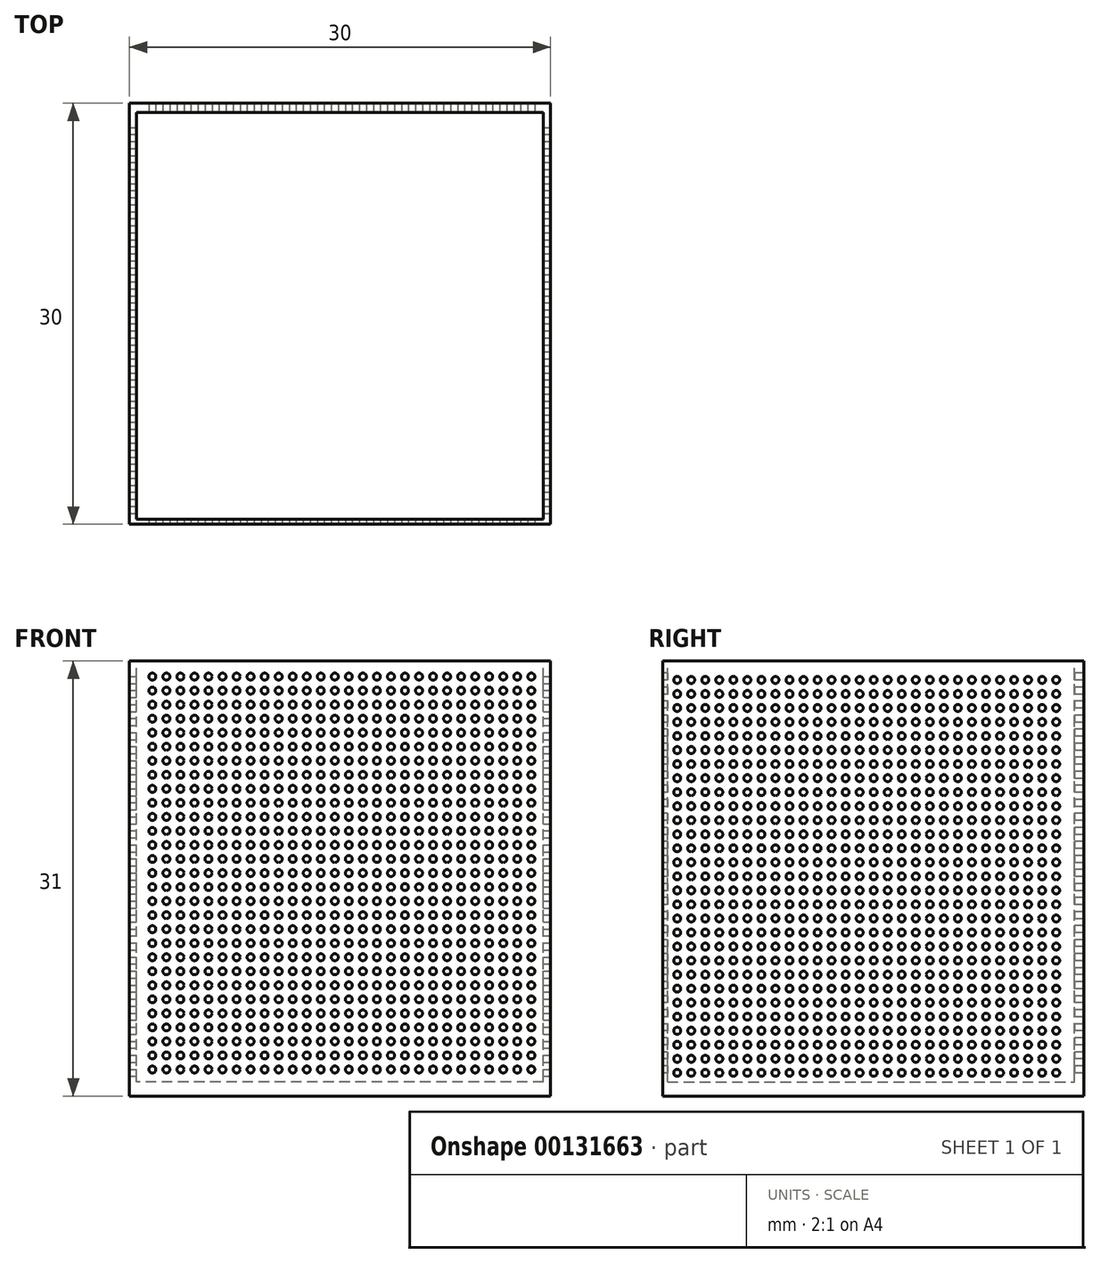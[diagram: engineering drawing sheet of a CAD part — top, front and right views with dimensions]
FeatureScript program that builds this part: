
annotation { "Feature Type Name" : "Feature", "Feature Type Description" : "" }
export const myFeature = defineFeature(function(context is Context, id is Id, definition is map)
    precondition{}
    {
        {
            var Q0;
            Q0=qCreatedBy(makeId("Top.planeOp"),FACE);
            var sketch = newSketch(context, id + "F0", { "sketchPlane" : qUnion([Q0])});
            skLineSegment(sketch, "E0.bottom", {"start": v(15, -14.84) * mm, "end": v(-15, -14.84) * mm});
            skLineSegment(sketch, "E0.top", {"start": v(15, 15.16) * mm, "end": v(-15, 15.16) * mm});
            skLineSegment(sketch, "E0.left", {"start": v(15, -14.84) * mm, "end": v(15, 15.16) * mm});
            skLineSegment(sketch, "E0.right", {"start": v(-15, -14.84) * mm, "end": v(-15, 15.16) * mm});
            skPoint(sketch, "E0.middle", {"position": v(0, 0.16) * mm});
            skSolve(sketch);
        }
        {
            var Q0;
            Q0 = qSketchRegion(id + "F0", true);
            extrude(context, id + "F1", {"entities" : qUnion([Q0]), "depth" : 31 * mm});
        }
        {
            var Q0;
            Q0=makeQuery(id+"F1.opExtrude","CAP_FACE",FACE,{"disambiguationData":[OSD([sQuery(id+"F0.wireOp",EDGE,"E0.bottom"),sQuery(id+"F0.wireOp",EDGE,"E0.top"),sQuery(id+"F0.wireOp",EDGE,"E0.left"),sQuery(id+"F0.wireOp",EDGE,"E0.right")])],"isStart":false});
            var sketch = newSketch(context, id + "F2", { "sketchPlane" : qUnion([Q0])});
            skLineSegment(sketch, "E1.bottom", {"start": v(14.5, -14.5) * mm, "end": v(-14.5, -14.5) * mm});
            skLineSegment(sketch, "E1.top", {"start": v(14.5, 14.5) * mm, "end": v(-14.5, 14.5) * mm});
            skLineSegment(sketch, "E1.left", {"start": v(14.5, -14.5) * mm, "end": v(14.5, 14.5) * mm});
            skLineSegment(sketch, "E1.right", {"start": v(-14.5, -14.5) * mm, "end": v(-14.5, 14.5) * mm});
            skPoint(sketch, "E1.middle", {"position": v(0, 0) * mm});
            skSolve(sketch);
        }
        {
            var Q0;
            Q0 = qSketchRegion(id + "F2", true);
            extrude(context, id + "F3", {"entities" : qUnion([Q0]), "operationType" : NewBodyOperationType.REMOVE, "oppositeDirection" : true, "depth" : 30 * mm});
        }
        {
            var Q0;
            Q0=makeQuery(id+"F1.opExtrude","SWEPT_FACE",FACE,{"disambiguationData":[OSD([sQuery(id+"F0.wireOp",EDGE,"E0.bottom")])]});
            var sketch = newSketch(context, id + "F4", { "sketchPlane" : qUnion([Q0])});
            skCircle(sketch, "E2", {"center": v(-13.37, 1.9) * mm, "radius": 0.25 * mm});
            skCircle(sketch, "E3.0.1.0", {"center": v(-13.37, 2.9) * mm, "radius": 0.25 * mm});
            skCircle(sketch, "E3.0.2.0", {"center": v(-13.37, 3.9) * mm, "radius": 0.25 * mm});
            skCircle(sketch, "E3.0.3.0", {"center": v(-13.37, 4.9) * mm, "radius": 0.25 * mm});
            skCircle(sketch, "E3.0.4.0", {"center": v(-13.37, 5.9) * mm, "radius": 0.25 * mm});
            skCircle(sketch, "E3.0.5.0", {"center": v(-13.37, 6.9) * mm, "radius": 0.25 * mm});
            skCircle(sketch, "E3.0.6.0", {"center": v(-13.37, 7.9) * mm, "radius": 0.25 * mm});
            skCircle(sketch, "E3.0.7.0", {"center": v(-13.37, 8.9) * mm, "radius": 0.25 * mm});
            skCircle(sketch, "E3.0.8.0", {"center": v(-13.37, 9.9) * mm, "radius": 0.25 * mm});
            skCircle(sketch, "E3.0.9.0", {"center": v(-13.37, 10.9) * mm, "radius": 0.25 * mm});
            skCircle(sketch, "E3.0.10.0", {"center": v(-13.37, 11.9) * mm, "radius": 0.25 * mm});
            skCircle(sketch, "E3.0.11.0", {"center": v(-13.37, 12.9) * mm, "radius": 0.25 * mm});
            skCircle(sketch, "E3.0.12.0", {"center": v(-13.37, 13.9) * mm, "radius": 0.25 * mm});
            skCircle(sketch, "E3.0.13.0", {"center": v(-13.37, 14.9) * mm, "radius": 0.25 * mm});
            skCircle(sketch, "E3.0.14.0", {"center": v(-13.37, 15.9) * mm, "radius": 0.25 * mm});
            skCircle(sketch, "E3.0.15.0", {"center": v(-13.37, 16.9) * mm, "radius": 0.25 * mm});
            skCircle(sketch, "E3.0.16.0", {"center": v(-13.37, 17.9) * mm, "radius": 0.25 * mm});
            skCircle(sketch, "E3.0.17.0", {"center": v(-13.37, 18.9) * mm, "radius": 0.25 * mm});
            skCircle(sketch, "E3.0.18.0", {"center": v(-13.37, 19.9) * mm, "radius": 0.25 * mm});
            skCircle(sketch, "E3.0.19.0", {"center": v(-13.37, 20.9) * mm, "radius": 0.25 * mm});
            skCircle(sketch, "E3.0.20.0", {"center": v(-13.37, 21.9) * mm, "radius": 0.25 * mm});
            skCircle(sketch, "E3.0.21.0", {"center": v(-13.37, 22.9) * mm, "radius": 0.25 * mm});
            skCircle(sketch, "E3.0.22.0", {"center": v(-13.37, 23.9) * mm, "radius": 0.25 * mm});
            skCircle(sketch, "E3.0.23.0", {"center": v(-13.37, 24.9) * mm, "radius": 0.25 * mm});
            skCircle(sketch, "E3.0.24.0", {"center": v(-13.37, 25.9) * mm, "radius": 0.25 * mm});
            skCircle(sketch, "E3.0.25.0", {"center": v(-13.37, 26.9) * mm, "radius": 0.25 * mm});
            skCircle(sketch, "E3.0.26.0", {"center": v(-13.37, 27.9) * mm, "radius": 0.25 * mm});
            skCircle(sketch, "E3.0.27.0", {"center": v(-13.37, 28.9) * mm, "radius": 0.25 * mm});
            skCircle(sketch, "E3.0.28.0", {"center": v(-13.37, 29.9) * mm, "radius": 0.25 * mm});
            skCircle(sketch, "E3.1.0.0", {"center": v(-12.37, 1.9) * mm, "radius": 0.25 * mm});
            skCircle(sketch, "E3.1.1.0", {"center": v(-12.37, 2.9) * mm, "radius": 0.25 * mm});
            skCircle(sketch, "E3.1.2.0", {"center": v(-12.37, 3.9) * mm, "radius": 0.25 * mm});
            skCircle(sketch, "E3.1.3.0", {"center": v(-12.37, 4.9) * mm, "radius": 0.25 * mm});
            skCircle(sketch, "E3.1.4.0", {"center": v(-12.37, 5.9) * mm, "radius": 0.25 * mm});
            skCircle(sketch, "E3.1.5.0", {"center": v(-12.37, 6.9) * mm, "radius": 0.25 * mm});
            skCircle(sketch, "E3.1.6.0", {"center": v(-12.37, 7.9) * mm, "radius": 0.25 * mm});
            skCircle(sketch, "E3.1.7.0", {"center": v(-12.37, 8.9) * mm, "radius": 0.25 * mm});
            skCircle(sketch, "E3.1.8.0", {"center": v(-12.37, 9.9) * mm, "radius": 0.25 * mm});
            skCircle(sketch, "E3.1.9.0", {"center": v(-12.37, 10.9) * mm, "radius": 0.25 * mm});
            skCircle(sketch, "E3.1.10.0", {"center": v(-12.37, 11.9) * mm, "radius": 0.25 * mm});
            skCircle(sketch, "E3.1.11.0", {"center": v(-12.37, 12.9) * mm, "radius": 0.25 * mm});
            skCircle(sketch, "E3.1.12.0", {"center": v(-12.37, 13.9) * mm, "radius": 0.25 * mm});
            skCircle(sketch, "E3.1.13.0", {"center": v(-12.37, 14.9) * mm, "radius": 0.25 * mm});
            skCircle(sketch, "E3.1.14.0", {"center": v(-12.37, 15.9) * mm, "radius": 0.25 * mm});
            skCircle(sketch, "E3.1.15.0", {"center": v(-12.37, 16.9) * mm, "radius": 0.25 * mm});
            skCircle(sketch, "E3.1.16.0", {"center": v(-12.37, 17.9) * mm, "radius": 0.25 * mm});
            skCircle(sketch, "E3.1.17.0", {"center": v(-12.37, 18.9) * mm, "radius": 0.25 * mm});
            skCircle(sketch, "E3.1.18.0", {"center": v(-12.37, 19.9) * mm, "radius": 0.25 * mm});
            skCircle(sketch, "E3.1.19.0", {"center": v(-12.37, 20.9) * mm, "radius": 0.25 * mm});
            skCircle(sketch, "E3.1.20.0", {"center": v(-12.37, 21.9) * mm, "radius": 0.25 * mm});
            skCircle(sketch, "E3.1.21.0", {"center": v(-12.37, 22.9) * mm, "radius": 0.25 * mm});
            skCircle(sketch, "E3.1.22.0", {"center": v(-12.37, 23.9) * mm, "radius": 0.25 * mm});
            skCircle(sketch, "E3.1.23.0", {"center": v(-12.37, 24.9) * mm, "radius": 0.25 * mm});
            skCircle(sketch, "E3.1.24.0", {"center": v(-12.37, 25.9) * mm, "radius": 0.25 * mm});
            skCircle(sketch, "E3.1.25.0", {"center": v(-12.37, 26.9) * mm, "radius": 0.25 * mm});
            skCircle(sketch, "E3.1.26.0", {"center": v(-12.37, 27.9) * mm, "radius": 0.25 * mm});
            skCircle(sketch, "E3.1.27.0", {"center": v(-12.37, 28.9) * mm, "radius": 0.25 * mm});
            skCircle(sketch, "E3.1.28.0", {"center": v(-12.37, 29.9) * mm, "radius": 0.25 * mm});
            skCircle(sketch, "E3.2.0.0", {"center": v(-11.37, 1.9) * mm, "radius": 0.25 * mm});
            skCircle(sketch, "E3.2.1.0", {"center": v(-11.37, 2.9) * mm, "radius": 0.25 * mm});
            skCircle(sketch, "E3.2.2.0", {"center": v(-11.37, 3.9) * mm, "radius": 0.25 * mm});
            skCircle(sketch, "E3.2.3.0", {"center": v(-11.37, 4.9) * mm, "radius": 0.25 * mm});
            skCircle(sketch, "E3.2.4.0", {"center": v(-11.37, 5.9) * mm, "radius": 0.25 * mm});
            skCircle(sketch, "E3.2.5.0", {"center": v(-11.37, 6.9) * mm, "radius": 0.25 * mm});
            skCircle(sketch, "E3.2.6.0", {"center": v(-11.37, 7.9) * mm, "radius": 0.25 * mm});
            skCircle(sketch, "E3.2.7.0", {"center": v(-11.37, 8.9) * mm, "radius": 0.25 * mm});
            skCircle(sketch, "E3.2.8.0", {"center": v(-11.37, 9.9) * mm, "radius": 0.25 * mm});
            skCircle(sketch, "E3.2.9.0", {"center": v(-11.37, 10.9) * mm, "radius": 0.25 * mm});
            skCircle(sketch, "E3.2.10.0", {"center": v(-11.37, 11.9) * mm, "radius": 0.25 * mm});
            skCircle(sketch, "E3.2.11.0", {"center": v(-11.37, 12.9) * mm, "radius": 0.25 * mm});
            skCircle(sketch, "E3.2.12.0", {"center": v(-11.37, 13.9) * mm, "radius": 0.25 * mm});
            skCircle(sketch, "E3.2.13.0", {"center": v(-11.37, 14.9) * mm, "radius": 0.25 * mm});
            skCircle(sketch, "E3.2.14.0", {"center": v(-11.37, 15.9) * mm, "radius": 0.25 * mm});
            skCircle(sketch, "E3.2.15.0", {"center": v(-11.37, 16.9) * mm, "radius": 0.25 * mm});
            skCircle(sketch, "E3.2.16.0", {"center": v(-11.37, 17.9) * mm, "radius": 0.25 * mm});
            skCircle(sketch, "E3.2.17.0", {"center": v(-11.37, 18.9) * mm, "radius": 0.25 * mm});
            skCircle(sketch, "E3.2.18.0", {"center": v(-11.37, 19.9) * mm, "radius": 0.25 * mm});
            skCircle(sketch, "E3.2.19.0", {"center": v(-11.37, 20.9) * mm, "radius": 0.25 * mm});
            skCircle(sketch, "E3.2.20.0", {"center": v(-11.37, 21.9) * mm, "radius": 0.25 * mm});
            skCircle(sketch, "E3.2.21.0", {"center": v(-11.37, 22.9) * mm, "radius": 0.25 * mm});
            skCircle(sketch, "E3.2.22.0", {"center": v(-11.37, 23.9) * mm, "radius": 0.25 * mm});
            skCircle(sketch, "E3.2.23.0", {"center": v(-11.37, 24.9) * mm, "radius": 0.25 * mm});
            skCircle(sketch, "E3.2.24.0", {"center": v(-11.37, 25.9) * mm, "radius": 0.25 * mm});
            skCircle(sketch, "E3.2.25.0", {"center": v(-11.37, 26.9) * mm, "radius": 0.25 * mm});
            skCircle(sketch, "E3.2.26.0", {"center": v(-11.37, 27.9) * mm, "radius": 0.25 * mm});
            skCircle(sketch, "E3.2.27.0", {"center": v(-11.37, 28.9) * mm, "radius": 0.25 * mm});
            skCircle(sketch, "E3.2.28.0", {"center": v(-11.37, 29.9) * mm, "radius": 0.25 * mm});
            skCircle(sketch, "E3.3.0.0", {"center": v(-10.37, 1.9) * mm, "radius": 0.25 * mm});
            skCircle(sketch, "E3.3.1.0", {"center": v(-10.37, 2.9) * mm, "radius": 0.25 * mm});
            skCircle(sketch, "E3.3.2.0", {"center": v(-10.37, 3.9) * mm, "radius": 0.25 * mm});
            skCircle(sketch, "E3.3.3.0", {"center": v(-10.37, 4.9) * mm, "radius": 0.25 * mm});
            skCircle(sketch, "E3.3.4.0", {"center": v(-10.37, 5.9) * mm, "radius": 0.25 * mm});
            skCircle(sketch, "E3.3.5.0", {"center": v(-10.37, 6.9) * mm, "radius": 0.25 * mm});
            skCircle(sketch, "E3.3.6.0", {"center": v(-10.37, 7.9) * mm, "radius": 0.25 * mm});
            skCircle(sketch, "E3.3.7.0", {"center": v(-10.37, 8.9) * mm, "radius": 0.25 * mm});
            skCircle(sketch, "E3.3.8.0", {"center": v(-10.37, 9.9) * mm, "radius": 0.25 * mm});
            skCircle(sketch, "E3.3.9.0", {"center": v(-10.37, 10.9) * mm, "radius": 0.25 * mm});
            skCircle(sketch, "E3.3.10.0", {"center": v(-10.37, 11.9) * mm, "radius": 0.25 * mm});
            skCircle(sketch, "E3.3.11.0", {"center": v(-10.37, 12.9) * mm, "radius": 0.25 * mm});
            skCircle(sketch, "E3.3.12.0", {"center": v(-10.37, 13.9) * mm, "radius": 0.25 * mm});
            skCircle(sketch, "E3.3.13.0", {"center": v(-10.37, 14.9) * mm, "radius": 0.25 * mm});
            skCircle(sketch, "E3.3.14.0", {"center": v(-10.37, 15.9) * mm, "radius": 0.25 * mm});
            skCircle(sketch, "E3.3.15.0", {"center": v(-10.37, 16.9) * mm, "radius": 0.25 * mm});
            skCircle(sketch, "E3.3.16.0", {"center": v(-10.37, 17.9) * mm, "radius": 0.25 * mm});
            skCircle(sketch, "E3.3.17.0", {"center": v(-10.37, 18.9) * mm, "radius": 0.25 * mm});
            skCircle(sketch, "E3.3.18.0", {"center": v(-10.37, 19.9) * mm, "radius": 0.25 * mm});
            skCircle(sketch, "E3.3.19.0", {"center": v(-10.37, 20.9) * mm, "radius": 0.25 * mm});
            skCircle(sketch, "E3.3.20.0", {"center": v(-10.37, 21.9) * mm, "radius": 0.25 * mm});
            skCircle(sketch, "E3.3.21.0", {"center": v(-10.37, 22.9) * mm, "radius": 0.25 * mm});
            skCircle(sketch, "E3.3.22.0", {"center": v(-10.37, 23.9) * mm, "radius": 0.25 * mm});
            skCircle(sketch, "E3.3.23.0", {"center": v(-10.37, 24.9) * mm, "radius": 0.25 * mm});
            skCircle(sketch, "E3.3.24.0", {"center": v(-10.37, 25.9) * mm, "radius": 0.25 * mm});
            skCircle(sketch, "E3.3.25.0", {"center": v(-10.37, 26.9) * mm, "radius": 0.25 * mm});
            skCircle(sketch, "E3.3.26.0", {"center": v(-10.37, 27.9) * mm, "radius": 0.25 * mm});
            skCircle(sketch, "E3.3.27.0", {"center": v(-10.37, 28.9) * mm, "radius": 0.25 * mm});
            skCircle(sketch, "E3.3.28.0", {"center": v(-10.37, 29.9) * mm, "radius": 0.25 * mm});
            skCircle(sketch, "E3.4.0.0", {"center": v(-9.37, 1.9) * mm, "radius": 0.25 * mm});
            skCircle(sketch, "E3.4.1.0", {"center": v(-9.37, 2.9) * mm, "radius": 0.25 * mm});
            skCircle(sketch, "E3.4.2.0", {"center": v(-9.37, 3.9) * mm, "radius": 0.25 * mm});
            skCircle(sketch, "E3.4.3.0", {"center": v(-9.37, 4.9) * mm, "radius": 0.25 * mm});
            skCircle(sketch, "E3.4.4.0", {"center": v(-9.37, 5.9) * mm, "radius": 0.25 * mm});
            skCircle(sketch, "E3.4.5.0", {"center": v(-9.37, 6.9) * mm, "radius": 0.25 * mm});
            skCircle(sketch, "E3.4.6.0", {"center": v(-9.37, 7.9) * mm, "radius": 0.25 * mm});
            skCircle(sketch, "E3.4.7.0", {"center": v(-9.37, 8.9) * mm, "radius": 0.25 * mm});
            skCircle(sketch, "E3.4.8.0", {"center": v(-9.37, 9.9) * mm, "radius": 0.25 * mm});
            skCircle(sketch, "E3.4.9.0", {"center": v(-9.37, 10.9) * mm, "radius": 0.25 * mm});
            skCircle(sketch, "E3.4.10.0", {"center": v(-9.37, 11.9) * mm, "radius": 0.25 * mm});
            skCircle(sketch, "E3.4.11.0", {"center": v(-9.37, 12.9) * mm, "radius": 0.25 * mm});
            skCircle(sketch, "E3.4.12.0", {"center": v(-9.37, 13.9) * mm, "radius": 0.25 * mm});
            skCircle(sketch, "E3.4.13.0", {"center": v(-9.37, 14.9) * mm, "radius": 0.25 * mm});
            skCircle(sketch, "E3.4.14.0", {"center": v(-9.37, 15.9) * mm, "radius": 0.25 * mm});
            skCircle(sketch, "E3.4.15.0", {"center": v(-9.37, 16.9) * mm, "radius": 0.25 * mm});
            skCircle(sketch, "E3.4.16.0", {"center": v(-9.37, 17.9) * mm, "radius": 0.25 * mm});
            skCircle(sketch, "E3.4.17.0", {"center": v(-9.37, 18.9) * mm, "radius": 0.25 * mm});
            skCircle(sketch, "E3.4.18.0", {"center": v(-9.37, 19.9) * mm, "radius": 0.25 * mm});
            skCircle(sketch, "E3.4.19.0", {"center": v(-9.37, 20.9) * mm, "radius": 0.25 * mm});
            skCircle(sketch, "E3.4.20.0", {"center": v(-9.37, 21.9) * mm, "radius": 0.25 * mm});
            skCircle(sketch, "E3.4.21.0", {"center": v(-9.37, 22.9) * mm, "radius": 0.25 * mm});
            skCircle(sketch, "E3.4.22.0", {"center": v(-9.37, 23.9) * mm, "radius": 0.25 * mm});
            skCircle(sketch, "E3.4.23.0", {"center": v(-9.37, 24.9) * mm, "radius": 0.25 * mm});
            skCircle(sketch, "E3.4.24.0", {"center": v(-9.37, 25.9) * mm, "radius": 0.25 * mm});
            skCircle(sketch, "E3.4.25.0", {"center": v(-9.37, 26.9) * mm, "radius": 0.25 * mm});
            skCircle(sketch, "E3.4.26.0", {"center": v(-9.37, 27.9) * mm, "radius": 0.25 * mm});
            skCircle(sketch, "E3.4.27.0", {"center": v(-9.37, 28.9) * mm, "radius": 0.25 * mm});
            skCircle(sketch, "E3.4.28.0", {"center": v(-9.37, 29.9) * mm, "radius": 0.25 * mm});
            skCircle(sketch, "E3.5.0.0", {"center": v(-8.37, 1.9) * mm, "radius": 0.25 * mm});
            skCircle(sketch, "E3.5.1.0", {"center": v(-8.37, 2.9) * mm, "radius": 0.25 * mm});
            skCircle(sketch, "E3.5.2.0", {"center": v(-8.37, 3.9) * mm, "radius": 0.25 * mm});
            skCircle(sketch, "E3.5.3.0", {"center": v(-8.37, 4.9) * mm, "radius": 0.25 * mm});
            skCircle(sketch, "E3.5.4.0", {"center": v(-8.37, 5.9) * mm, "radius": 0.25 * mm});
            skCircle(sketch, "E3.5.5.0", {"center": v(-8.37, 6.9) * mm, "radius": 0.25 * mm});
            skCircle(sketch, "E3.5.6.0", {"center": v(-8.37, 7.9) * mm, "radius": 0.25 * mm});
            skCircle(sketch, "E3.5.7.0", {"center": v(-8.37, 8.9) * mm, "radius": 0.25 * mm});
            skCircle(sketch, "E3.5.8.0", {"center": v(-8.37, 9.9) * mm, "radius": 0.25 * mm});
            skCircle(sketch, "E3.5.9.0", {"center": v(-8.37, 10.9) * mm, "radius": 0.25 * mm});
            skCircle(sketch, "E3.5.10.0", {"center": v(-8.37, 11.9) * mm, "radius": 0.25 * mm});
            skCircle(sketch, "E3.5.11.0", {"center": v(-8.37, 12.9) * mm, "radius": 0.25 * mm});
            skCircle(sketch, "E3.5.12.0", {"center": v(-8.37, 13.9) * mm, "radius": 0.25 * mm});
            skCircle(sketch, "E3.5.13.0", {"center": v(-8.37, 14.9) * mm, "radius": 0.25 * mm});
            skCircle(sketch, "E3.5.14.0", {"center": v(-8.37, 15.9) * mm, "radius": 0.25 * mm});
            skCircle(sketch, "E3.5.15.0", {"center": v(-8.37, 16.9) * mm, "radius": 0.25 * mm});
            skCircle(sketch, "E3.5.16.0", {"center": v(-8.37, 17.9) * mm, "radius": 0.25 * mm});
            skCircle(sketch, "E3.5.17.0", {"center": v(-8.37, 18.9) * mm, "radius": 0.25 * mm});
            skCircle(sketch, "E3.5.18.0", {"center": v(-8.37, 19.9) * mm, "radius": 0.25 * mm});
            skCircle(sketch, "E3.5.19.0", {"center": v(-8.37, 20.9) * mm, "radius": 0.25 * mm});
            skCircle(sketch, "E3.5.20.0", {"center": v(-8.37, 21.9) * mm, "radius": 0.25 * mm});
            skCircle(sketch, "E3.5.21.0", {"center": v(-8.37, 22.9) * mm, "radius": 0.25 * mm});
            skCircle(sketch, "E3.5.22.0", {"center": v(-8.37, 23.9) * mm, "radius": 0.25 * mm});
            skCircle(sketch, "E3.5.23.0", {"center": v(-8.37, 24.9) * mm, "radius": 0.25 * mm});
            skCircle(sketch, "E3.5.24.0", {"center": v(-8.37, 25.9) * mm, "radius": 0.25 * mm});
            skCircle(sketch, "E3.5.25.0", {"center": v(-8.37, 26.9) * mm, "radius": 0.25 * mm});
            skCircle(sketch, "E3.5.26.0", {"center": v(-8.37, 27.9) * mm, "radius": 0.25 * mm});
            skCircle(sketch, "E3.5.27.0", {"center": v(-8.37, 28.9) * mm, "radius": 0.25 * mm});
            skCircle(sketch, "E3.5.28.0", {"center": v(-8.37, 29.9) * mm, "radius": 0.25 * mm});
            skCircle(sketch, "E3.6.0.0", {"center": v(-7.37, 1.9) * mm, "radius": 0.25 * mm});
            skCircle(sketch, "E3.6.1.0", {"center": v(-7.37, 2.9) * mm, "radius": 0.25 * mm});
            skCircle(sketch, "E3.6.2.0", {"center": v(-7.37, 3.9) * mm, "radius": 0.25 * mm});
            skCircle(sketch, "E3.6.3.0", {"center": v(-7.37, 4.9) * mm, "radius": 0.25 * mm});
            skCircle(sketch, "E3.6.4.0", {"center": v(-7.37, 5.9) * mm, "radius": 0.25 * mm});
            skCircle(sketch, "E3.6.5.0", {"center": v(-7.37, 6.9) * mm, "radius": 0.25 * mm});
            skCircle(sketch, "E3.6.6.0", {"center": v(-7.37, 7.9) * mm, "radius": 0.25 * mm});
            skCircle(sketch, "E3.6.7.0", {"center": v(-7.37, 8.9) * mm, "radius": 0.25 * mm});
            skCircle(sketch, "E3.6.8.0", {"center": v(-7.37, 9.9) * mm, "radius": 0.25 * mm});
            skCircle(sketch, "E3.6.9.0", {"center": v(-7.37, 10.9) * mm, "radius": 0.25 * mm});
            skCircle(sketch, "E3.6.10.0", {"center": v(-7.37, 11.9) * mm, "radius": 0.25 * mm});
            skCircle(sketch, "E3.6.11.0", {"center": v(-7.37, 12.9) * mm, "radius": 0.25 * mm});
            skCircle(sketch, "E3.6.12.0", {"center": v(-7.37, 13.9) * mm, "radius": 0.25 * mm});
            skCircle(sketch, "E3.6.13.0", {"center": v(-7.37, 14.9) * mm, "radius": 0.25 * mm});
            skCircle(sketch, "E3.6.14.0", {"center": v(-7.37, 15.9) * mm, "radius": 0.25 * mm});
            skCircle(sketch, "E3.6.15.0", {"center": v(-7.37, 16.9) * mm, "radius": 0.25 * mm});
            skCircle(sketch, "E3.6.16.0", {"center": v(-7.37, 17.9) * mm, "radius": 0.25 * mm});
            skCircle(sketch, "E3.6.17.0", {"center": v(-7.37, 18.9) * mm, "radius": 0.25 * mm});
            skCircle(sketch, "E3.6.18.0", {"center": v(-7.37, 19.9) * mm, "radius": 0.25 * mm});
            skCircle(sketch, "E3.6.19.0", {"center": v(-7.37, 20.9) * mm, "radius": 0.25 * mm});
            skCircle(sketch, "E3.6.20.0", {"center": v(-7.37, 21.9) * mm, "radius": 0.25 * mm});
            skCircle(sketch, "E3.6.21.0", {"center": v(-7.37, 22.9) * mm, "radius": 0.25 * mm});
            skCircle(sketch, "E3.6.22.0", {"center": v(-7.37, 23.9) * mm, "radius": 0.25 * mm});
            skCircle(sketch, "E3.6.23.0", {"center": v(-7.37, 24.9) * mm, "radius": 0.25 * mm});
            skCircle(sketch, "E3.6.24.0", {"center": v(-7.37, 25.9) * mm, "radius": 0.25 * mm});
            skCircle(sketch, "E3.6.25.0", {"center": v(-7.37, 26.9) * mm, "radius": 0.25 * mm});
            skCircle(sketch, "E3.6.26.0", {"center": v(-7.37, 27.9) * mm, "radius": 0.25 * mm});
            skCircle(sketch, "E3.6.27.0", {"center": v(-7.37, 28.9) * mm, "radius": 0.25 * mm});
            skCircle(sketch, "E3.6.28.0", {"center": v(-7.37, 29.9) * mm, "radius": 0.25 * mm});
            skCircle(sketch, "E3.7.0.0", {"center": v(-6.37, 1.9) * mm, "radius": 0.25 * mm});
            skCircle(sketch, "E3.7.1.0", {"center": v(-6.37, 2.9) * mm, "radius": 0.25 * mm});
            skCircle(sketch, "E3.7.2.0", {"center": v(-6.37, 3.9) * mm, "radius": 0.25 * mm});
            skCircle(sketch, "E3.7.3.0", {"center": v(-6.37, 4.9) * mm, "radius": 0.25 * mm});
            skCircle(sketch, "E3.7.4.0", {"center": v(-6.37, 5.9) * mm, "radius": 0.25 * mm});
            skCircle(sketch, "E3.7.5.0", {"center": v(-6.37, 6.9) * mm, "radius": 0.25 * mm});
            skCircle(sketch, "E3.7.6.0", {"center": v(-6.37, 7.9) * mm, "radius": 0.25 * mm});
            skCircle(sketch, "E3.7.7.0", {"center": v(-6.37, 8.9) * mm, "radius": 0.25 * mm});
            skCircle(sketch, "E3.7.8.0", {"center": v(-6.37, 9.9) * mm, "radius": 0.25 * mm});
            skCircle(sketch, "E3.7.9.0", {"center": v(-6.37, 10.9) * mm, "radius": 0.25 * mm});
            skCircle(sketch, "E3.7.10.0", {"center": v(-6.37, 11.9) * mm, "radius": 0.25 * mm});
            skCircle(sketch, "E3.7.11.0", {"center": v(-6.37, 12.9) * mm, "radius": 0.25 * mm});
            skCircle(sketch, "E3.7.12.0", {"center": v(-6.37, 13.9) * mm, "radius": 0.25 * mm});
            skCircle(sketch, "E3.7.13.0", {"center": v(-6.37, 14.9) * mm, "radius": 0.25 * mm});
            skCircle(sketch, "E3.7.14.0", {"center": v(-6.37, 15.9) * mm, "radius": 0.25 * mm});
            skCircle(sketch, "E3.7.15.0", {"center": v(-6.37, 16.9) * mm, "radius": 0.25 * mm});
            skCircle(sketch, "E3.7.16.0", {"center": v(-6.37, 17.9) * mm, "radius": 0.25 * mm});
            skCircle(sketch, "E3.7.17.0", {"center": v(-6.37, 18.9) * mm, "radius": 0.25 * mm});
            skCircle(sketch, "E3.7.18.0", {"center": v(-6.37, 19.9) * mm, "radius": 0.25 * mm});
            skCircle(sketch, "E3.7.19.0", {"center": v(-6.37, 20.9) * mm, "radius": 0.25 * mm});
            skCircle(sketch, "E3.7.20.0", {"center": v(-6.37, 21.9) * mm, "radius": 0.25 * mm});
            skCircle(sketch, "E3.7.21.0", {"center": v(-6.37, 22.9) * mm, "radius": 0.25 * mm});
            skCircle(sketch, "E3.7.22.0", {"center": v(-6.37, 23.9) * mm, "radius": 0.25 * mm});
            skCircle(sketch, "E3.7.23.0", {"center": v(-6.37, 24.9) * mm, "radius": 0.25 * mm});
            skCircle(sketch, "E3.7.24.0", {"center": v(-6.37, 25.9) * mm, "radius": 0.25 * mm});
            skCircle(sketch, "E3.7.25.0", {"center": v(-6.37, 26.9) * mm, "radius": 0.25 * mm});
            skCircle(sketch, "E3.7.26.0", {"center": v(-6.37, 27.9) * mm, "radius": 0.25 * mm});
            skCircle(sketch, "E3.7.27.0", {"center": v(-6.37, 28.9) * mm, "radius": 0.25 * mm});
            skCircle(sketch, "E3.7.28.0", {"center": v(-6.37, 29.9) * mm, "radius": 0.25 * mm});
            skCircle(sketch, "E3.8.0.0", {"center": v(-5.37, 1.9) * mm, "radius": 0.25 * mm});
            skCircle(sketch, "E3.8.1.0", {"center": v(-5.37, 2.9) * mm, "radius": 0.25 * mm});
            skCircle(sketch, "E3.8.2.0", {"center": v(-5.37, 3.9) * mm, "radius": 0.25 * mm});
            skCircle(sketch, "E3.8.3.0", {"center": v(-5.37, 4.9) * mm, "radius": 0.25 * mm});
            skCircle(sketch, "E3.8.4.0", {"center": v(-5.37, 5.9) * mm, "radius": 0.25 * mm});
            skCircle(sketch, "E3.8.5.0", {"center": v(-5.37, 6.9) * mm, "radius": 0.25 * mm});
            skCircle(sketch, "E3.8.6.0", {"center": v(-5.37, 7.9) * mm, "radius": 0.25 * mm});
            skCircle(sketch, "E3.8.7.0", {"center": v(-5.37, 8.9) * mm, "radius": 0.25 * mm});
            skCircle(sketch, "E3.8.8.0", {"center": v(-5.37, 9.9) * mm, "radius": 0.25 * mm});
            skCircle(sketch, "E3.8.9.0", {"center": v(-5.37, 10.9) * mm, "radius": 0.25 * mm});
            skCircle(sketch, "E3.8.10.0", {"center": v(-5.37, 11.9) * mm, "radius": 0.25 * mm});
            skCircle(sketch, "E3.8.11.0", {"center": v(-5.37, 12.9) * mm, "radius": 0.25 * mm});
            skCircle(sketch, "E3.8.12.0", {"center": v(-5.37, 13.9) * mm, "radius": 0.25 * mm});
            skCircle(sketch, "E3.8.13.0", {"center": v(-5.37, 14.9) * mm, "radius": 0.25 * mm});
            skCircle(sketch, "E3.8.14.0", {"center": v(-5.37, 15.9) * mm, "radius": 0.25 * mm});
            skCircle(sketch, "E3.8.15.0", {"center": v(-5.37, 16.9) * mm, "radius": 0.25 * mm});
            skCircle(sketch, "E3.8.16.0", {"center": v(-5.37, 17.9) * mm, "radius": 0.25 * mm});
            skCircle(sketch, "E3.8.17.0", {"center": v(-5.37, 18.9) * mm, "radius": 0.25 * mm});
            skCircle(sketch, "E3.8.18.0", {"center": v(-5.37, 19.9) * mm, "radius": 0.25 * mm});
            skCircle(sketch, "E3.8.19.0", {"center": v(-5.37, 20.9) * mm, "radius": 0.25 * mm});
            skCircle(sketch, "E3.8.20.0", {"center": v(-5.37, 21.9) * mm, "radius": 0.25 * mm});
            skCircle(sketch, "E3.8.21.0", {"center": v(-5.37, 22.9) * mm, "radius": 0.25 * mm});
            skCircle(sketch, "E3.8.22.0", {"center": v(-5.37, 23.9) * mm, "radius": 0.25 * mm});
            skCircle(sketch, "E3.8.23.0", {"center": v(-5.37, 24.9) * mm, "radius": 0.25 * mm});
            skCircle(sketch, "E3.8.24.0", {"center": v(-5.37, 25.9) * mm, "radius": 0.25 * mm});
            skCircle(sketch, "E3.8.25.0", {"center": v(-5.37, 26.9) * mm, "radius": 0.25 * mm});
            skCircle(sketch, "E3.8.26.0", {"center": v(-5.37, 27.9) * mm, "radius": 0.25 * mm});
            skCircle(sketch, "E3.8.27.0", {"center": v(-5.37, 28.9) * mm, "radius": 0.25 * mm});
            skCircle(sketch, "E3.8.28.0", {"center": v(-5.37, 29.9) * mm, "radius": 0.25 * mm});
            skCircle(sketch, "E3.9.0.0", {"center": v(-4.37, 1.9) * mm, "radius": 0.25 * mm});
            skCircle(sketch, "E3.9.1.0", {"center": v(-4.37, 2.9) * mm, "radius": 0.25 * mm});
            skCircle(sketch, "E3.9.2.0", {"center": v(-4.37, 3.9) * mm, "radius": 0.25 * mm});
            skCircle(sketch, "E3.9.3.0", {"center": v(-4.37, 4.9) * mm, "radius": 0.25 * mm});
            skCircle(sketch, "E3.9.4.0", {"center": v(-4.37, 5.9) * mm, "radius": 0.25 * mm});
            skCircle(sketch, "E3.9.5.0", {"center": v(-4.37, 6.9) * mm, "radius": 0.25 * mm});
            skCircle(sketch, "E3.9.6.0", {"center": v(-4.37, 7.9) * mm, "radius": 0.25 * mm});
            skCircle(sketch, "E3.9.7.0", {"center": v(-4.37, 8.9) * mm, "radius": 0.25 * mm});
            skCircle(sketch, "E3.9.8.0", {"center": v(-4.37, 9.9) * mm, "radius": 0.25 * mm});
            skCircle(sketch, "E3.9.9.0", {"center": v(-4.37, 10.9) * mm, "radius": 0.25 * mm});
            skCircle(sketch, "E3.9.10.0", {"center": v(-4.37, 11.9) * mm, "radius": 0.25 * mm});
            skCircle(sketch, "E3.9.11.0", {"center": v(-4.37, 12.9) * mm, "radius": 0.25 * mm});
            skCircle(sketch, "E3.9.12.0", {"center": v(-4.37, 13.9) * mm, "radius": 0.25 * mm});
            skCircle(sketch, "E3.9.13.0", {"center": v(-4.37, 14.9) * mm, "radius": 0.25 * mm});
            skCircle(sketch, "E3.9.14.0", {"center": v(-4.37, 15.9) * mm, "radius": 0.25 * mm});
            skCircle(sketch, "E3.9.15.0", {"center": v(-4.37, 16.9) * mm, "radius": 0.25 * mm});
            skCircle(sketch, "E3.9.16.0", {"center": v(-4.37, 17.9) * mm, "radius": 0.25 * mm});
            skCircle(sketch, "E3.9.17.0", {"center": v(-4.37, 18.9) * mm, "radius": 0.25 * mm});
            skCircle(sketch, "E3.9.18.0", {"center": v(-4.37, 19.9) * mm, "radius": 0.25 * mm});
            skCircle(sketch, "E3.9.19.0", {"center": v(-4.37, 20.9) * mm, "radius": 0.25 * mm});
            skCircle(sketch, "E3.9.20.0", {"center": v(-4.37, 21.9) * mm, "radius": 0.25 * mm});
            skCircle(sketch, "E3.9.21.0", {"center": v(-4.37, 22.9) * mm, "radius": 0.25 * mm});
            skCircle(sketch, "E3.9.22.0", {"center": v(-4.37, 23.9) * mm, "radius": 0.25 * mm});
            skCircle(sketch, "E3.9.23.0", {"center": v(-4.37, 24.9) * mm, "radius": 0.25 * mm});
            skCircle(sketch, "E3.9.24.0", {"center": v(-4.37, 25.9) * mm, "radius": 0.25 * mm});
            skCircle(sketch, "E3.9.25.0", {"center": v(-4.37, 26.9) * mm, "radius": 0.25 * mm});
            skCircle(sketch, "E3.9.26.0", {"center": v(-4.37, 27.9) * mm, "radius": 0.25 * mm});
            skCircle(sketch, "E3.9.27.0", {"center": v(-4.37, 28.9) * mm, "radius": 0.25 * mm});
            skCircle(sketch, "E3.9.28.0", {"center": v(-4.37, 29.9) * mm, "radius": 0.25 * mm});
            skCircle(sketch, "E3.10.0.0", {"center": v(-3.37, 1.9) * mm, "radius": 0.25 * mm});
            skCircle(sketch, "E3.10.1.0", {"center": v(-3.37, 2.9) * mm, "radius": 0.25 * mm});
            skCircle(sketch, "E3.10.2.0", {"center": v(-3.37, 3.9) * mm, "radius": 0.25 * mm});
            skCircle(sketch, "E3.10.3.0", {"center": v(-3.37, 4.9) * mm, "radius": 0.25 * mm});
            skCircle(sketch, "E3.10.4.0", {"center": v(-3.37, 5.9) * mm, "radius": 0.25 * mm});
            skCircle(sketch, "E3.10.5.0", {"center": v(-3.37, 6.9) * mm, "radius": 0.25 * mm});
            skCircle(sketch, "E3.10.6.0", {"center": v(-3.37, 7.9) * mm, "radius": 0.25 * mm});
            skCircle(sketch, "E3.10.7.0", {"center": v(-3.37, 8.9) * mm, "radius": 0.25 * mm});
            skCircle(sketch, "E3.10.8.0", {"center": v(-3.37, 9.9) * mm, "radius": 0.25 * mm});
            skCircle(sketch, "E3.10.9.0", {"center": v(-3.37, 10.9) * mm, "radius": 0.25 * mm});
            skCircle(sketch, "E3.10.10.0", {"center": v(-3.37, 11.9) * mm, "radius": 0.25 * mm});
            skCircle(sketch, "E3.10.11.0", {"center": v(-3.37, 12.9) * mm, "radius": 0.25 * mm});
            skCircle(sketch, "E3.10.12.0", {"center": v(-3.37, 13.9) * mm, "radius": 0.25 * mm});
            skCircle(sketch, "E3.10.13.0", {"center": v(-3.37, 14.9) * mm, "radius": 0.25 * mm});
            skCircle(sketch, "E3.10.14.0", {"center": v(-3.37, 15.9) * mm, "radius": 0.25 * mm});
            skCircle(sketch, "E3.10.15.0", {"center": v(-3.37, 16.9) * mm, "radius": 0.25 * mm});
            skCircle(sketch, "E3.10.16.0", {"center": v(-3.37, 17.9) * mm, "radius": 0.25 * mm});
            skCircle(sketch, "E3.10.17.0", {"center": v(-3.37, 18.9) * mm, "radius": 0.25 * mm});
            skCircle(sketch, "E3.10.18.0", {"center": v(-3.37, 19.9) * mm, "radius": 0.25 * mm});
            skCircle(sketch, "E3.10.19.0", {"center": v(-3.37, 20.9) * mm, "radius": 0.25 * mm});
            skCircle(sketch, "E3.10.20.0", {"center": v(-3.37, 21.9) * mm, "radius": 0.25 * mm});
            skCircle(sketch, "E3.10.21.0", {"center": v(-3.37, 22.9) * mm, "radius": 0.25 * mm});
            skCircle(sketch, "E3.10.22.0", {"center": v(-3.37, 23.9) * mm, "radius": 0.25 * mm});
            skCircle(sketch, "E3.10.23.0", {"center": v(-3.37, 24.9) * mm, "radius": 0.25 * mm});
            skCircle(sketch, "E3.10.24.0", {"center": v(-3.37, 25.9) * mm, "radius": 0.25 * mm});
            skCircle(sketch, "E3.10.25.0", {"center": v(-3.37, 26.9) * mm, "radius": 0.25 * mm});
            skCircle(sketch, "E3.10.26.0", {"center": v(-3.37, 27.9) * mm, "radius": 0.25 * mm});
            skCircle(sketch, "E3.10.27.0", {"center": v(-3.37, 28.9) * mm, "radius": 0.25 * mm});
            skCircle(sketch, "E3.10.28.0", {"center": v(-3.37, 29.9) * mm, "radius": 0.25 * mm});
            skCircle(sketch, "E3.11.0.0", {"center": v(-2.37, 1.9) * mm, "radius": 0.25 * mm});
            skCircle(sketch, "E3.11.1.0", {"center": v(-2.37, 2.9) * mm, "radius": 0.25 * mm});
            skCircle(sketch, "E3.11.2.0", {"center": v(-2.37, 3.9) * mm, "radius": 0.25 * mm});
            skCircle(sketch, "E3.11.3.0", {"center": v(-2.37, 4.9) * mm, "radius": 0.25 * mm});
            skCircle(sketch, "E3.11.4.0", {"center": v(-2.37, 5.9) * mm, "radius": 0.25 * mm});
            skCircle(sketch, "E3.11.5.0", {"center": v(-2.37, 6.9) * mm, "radius": 0.25 * mm});
            skCircle(sketch, "E3.11.6.0", {"center": v(-2.37, 7.9) * mm, "radius": 0.25 * mm});
            skCircle(sketch, "E3.11.7.0", {"center": v(-2.37, 8.9) * mm, "radius": 0.25 * mm});
            skCircle(sketch, "E3.11.8.0", {"center": v(-2.37, 9.9) * mm, "radius": 0.25 * mm});
            skCircle(sketch, "E3.11.9.0", {"center": v(-2.37, 10.9) * mm, "radius": 0.25 * mm});
            skCircle(sketch, "E3.11.10.0", {"center": v(-2.37, 11.9) * mm, "radius": 0.25 * mm});
            skCircle(sketch, "E3.11.11.0", {"center": v(-2.37, 12.9) * mm, "radius": 0.25 * mm});
            skCircle(sketch, "E3.11.12.0", {"center": v(-2.37, 13.9) * mm, "radius": 0.25 * mm});
            skCircle(sketch, "E3.11.13.0", {"center": v(-2.37, 14.9) * mm, "radius": 0.25 * mm});
            skCircle(sketch, "E3.11.14.0", {"center": v(-2.37, 15.9) * mm, "radius": 0.25 * mm});
            skCircle(sketch, "E3.11.15.0", {"center": v(-2.37, 16.9) * mm, "radius": 0.25 * mm});
            skCircle(sketch, "E3.11.16.0", {"center": v(-2.37, 17.9) * mm, "radius": 0.25 * mm});
            skCircle(sketch, "E3.11.17.0", {"center": v(-2.37, 18.9) * mm, "radius": 0.25 * mm});
            skCircle(sketch, "E3.11.18.0", {"center": v(-2.37, 19.9) * mm, "radius": 0.25 * mm});
            skCircle(sketch, "E3.11.19.0", {"center": v(-2.37, 20.9) * mm, "radius": 0.25 * mm});
            skCircle(sketch, "E3.11.20.0", {"center": v(-2.37, 21.9) * mm, "radius": 0.25 * mm});
            skCircle(sketch, "E3.11.21.0", {"center": v(-2.37, 22.9) * mm, "radius": 0.25 * mm});
            skCircle(sketch, "E3.11.22.0", {"center": v(-2.37, 23.9) * mm, "radius": 0.25 * mm});
            skCircle(sketch, "E3.11.23.0", {"center": v(-2.37, 24.9) * mm, "radius": 0.25 * mm});
            skCircle(sketch, "E3.11.24.0", {"center": v(-2.37, 25.9) * mm, "radius": 0.25 * mm});
            skCircle(sketch, "E3.11.25.0", {"center": v(-2.37, 26.9) * mm, "radius": 0.25 * mm});
            skCircle(sketch, "E3.11.26.0", {"center": v(-2.37, 27.9) * mm, "radius": 0.25 * mm});
            skCircle(sketch, "E3.11.27.0", {"center": v(-2.37, 28.9) * mm, "radius": 0.25 * mm});
            skCircle(sketch, "E3.11.28.0", {"center": v(-2.37, 29.9) * mm, "radius": 0.25 * mm});
            skCircle(sketch, "E3.12.0.0", {"center": v(-1.37, 1.9) * mm, "radius": 0.25 * mm});
            skCircle(sketch, "E3.12.1.0", {"center": v(-1.37, 2.9) * mm, "radius": 0.25 * mm});
            skCircle(sketch, "E3.12.2.0", {"center": v(-1.37, 3.9) * mm, "radius": 0.25 * mm});
            skCircle(sketch, "E3.12.3.0", {"center": v(-1.37, 4.9) * mm, "radius": 0.25 * mm});
            skCircle(sketch, "E3.12.4.0", {"center": v(-1.37, 5.9) * mm, "radius": 0.25 * mm});
            skCircle(sketch, "E3.12.5.0", {"center": v(-1.37, 6.9) * mm, "radius": 0.25 * mm});
            skCircle(sketch, "E3.12.6.0", {"center": v(-1.37, 7.9) * mm, "radius": 0.25 * mm});
            skCircle(sketch, "E3.12.7.0", {"center": v(-1.37, 8.9) * mm, "radius": 0.25 * mm});
            skCircle(sketch, "E3.12.8.0", {"center": v(-1.37, 9.9) * mm, "radius": 0.25 * mm});
            skCircle(sketch, "E3.12.9.0", {"center": v(-1.37, 10.9) * mm, "radius": 0.25 * mm});
            skCircle(sketch, "E3.12.10.0", {"center": v(-1.37, 11.9) * mm, "radius": 0.25 * mm});
            skCircle(sketch, "E3.12.11.0", {"center": v(-1.37, 12.9) * mm, "radius": 0.25 * mm});
            skCircle(sketch, "E3.12.12.0", {"center": v(-1.37, 13.9) * mm, "radius": 0.25 * mm});
            skCircle(sketch, "E3.12.13.0", {"center": v(-1.37, 14.9) * mm, "radius": 0.25 * mm});
            skCircle(sketch, "E3.12.14.0", {"center": v(-1.37, 15.9) * mm, "radius": 0.25 * mm});
            skCircle(sketch, "E3.12.15.0", {"center": v(-1.37, 16.9) * mm, "radius": 0.25 * mm});
            skCircle(sketch, "E3.12.16.0", {"center": v(-1.37, 17.9) * mm, "radius": 0.25 * mm});
            skCircle(sketch, "E3.12.17.0", {"center": v(-1.37, 18.9) * mm, "radius": 0.25 * mm});
            skCircle(sketch, "E3.12.18.0", {"center": v(-1.37, 19.9) * mm, "radius": 0.25 * mm});
            skCircle(sketch, "E3.12.19.0", {"center": v(-1.37, 20.9) * mm, "radius": 0.25 * mm});
            skCircle(sketch, "E3.12.20.0", {"center": v(-1.37, 21.9) * mm, "radius": 0.25 * mm});
            skCircle(sketch, "E3.12.21.0", {"center": v(-1.37, 22.9) * mm, "radius": 0.25 * mm});
            skCircle(sketch, "E3.12.22.0", {"center": v(-1.37, 23.9) * mm, "radius": 0.25 * mm});
            skCircle(sketch, "E3.12.23.0", {"center": v(-1.37, 24.9) * mm, "radius": 0.25 * mm});
            skCircle(sketch, "E3.12.24.0", {"center": v(-1.37, 25.9) * mm, "radius": 0.25 * mm});
            skCircle(sketch, "E3.12.25.0", {"center": v(-1.37, 26.9) * mm, "radius": 0.25 * mm});
            skCircle(sketch, "E3.12.26.0", {"center": v(-1.37, 27.9) * mm, "radius": 0.25 * mm});
            skCircle(sketch, "E3.12.27.0", {"center": v(-1.37, 28.9) * mm, "radius": 0.25 * mm});
            skCircle(sketch, "E3.12.28.0", {"center": v(-1.37, 29.9) * mm, "radius": 0.25 * mm});
            skCircle(sketch, "E3.13.0.0", {"center": v(-0.37, 1.9) * mm, "radius": 0.25 * mm});
            skCircle(sketch, "E3.13.1.0", {"center": v(-0.37, 2.9) * mm, "radius": 0.25 * mm});
            skCircle(sketch, "E3.13.2.0", {"center": v(-0.37, 3.9) * mm, "radius": 0.25 * mm});
            skCircle(sketch, "E3.13.3.0", {"center": v(-0.37, 4.9) * mm, "radius": 0.25 * mm});
            skCircle(sketch, "E3.13.4.0", {"center": v(-0.37, 5.9) * mm, "radius": 0.25 * mm});
            skCircle(sketch, "E3.13.5.0", {"center": v(-0.37, 6.9) * mm, "radius": 0.25 * mm});
            skCircle(sketch, "E3.13.6.0", {"center": v(-0.37, 7.9) * mm, "radius": 0.25 * mm});
            skCircle(sketch, "E3.13.7.0", {"center": v(-0.37, 8.9) * mm, "radius": 0.25 * mm});
            skCircle(sketch, "E3.13.8.0", {"center": v(-0.37, 9.9) * mm, "radius": 0.25 * mm});
            skCircle(sketch, "E3.13.9.0", {"center": v(-0.37, 10.9) * mm, "radius": 0.25 * mm});
            skCircle(sketch, "E3.13.10.0", {"center": v(-0.37, 11.9) * mm, "radius": 0.25 * mm});
            skCircle(sketch, "E3.13.11.0", {"center": v(-0.37, 12.9) * mm, "radius": 0.25 * mm});
            skCircle(sketch, "E3.13.12.0", {"center": v(-0.37, 13.9) * mm, "radius": 0.25 * mm});
            skCircle(sketch, "E3.13.13.0", {"center": v(-0.37, 14.9) * mm, "radius": 0.25 * mm});
            skCircle(sketch, "E3.13.14.0", {"center": v(-0.37, 15.9) * mm, "radius": 0.25 * mm});
            skCircle(sketch, "E3.13.15.0", {"center": v(-0.37, 16.9) * mm, "radius": 0.25 * mm});
            skCircle(sketch, "E3.13.16.0", {"center": v(-0.37, 17.9) * mm, "radius": 0.25 * mm});
            skCircle(sketch, "E3.13.17.0", {"center": v(-0.37, 18.9) * mm, "radius": 0.25 * mm});
            skCircle(sketch, "E3.13.18.0", {"center": v(-0.37, 19.9) * mm, "radius": 0.25 * mm});
            skCircle(sketch, "E3.13.19.0", {"center": v(-0.37, 20.9) * mm, "radius": 0.25 * mm});
            skCircle(sketch, "E3.13.20.0", {"center": v(-0.37, 21.9) * mm, "radius": 0.25 * mm});
            skCircle(sketch, "E3.13.21.0", {"center": v(-0.37, 22.9) * mm, "radius": 0.25 * mm});
            skCircle(sketch, "E3.13.22.0", {"center": v(-0.37, 23.9) * mm, "radius": 0.25 * mm});
            skCircle(sketch, "E3.13.23.0", {"center": v(-0.37, 24.9) * mm, "radius": 0.25 * mm});
            skCircle(sketch, "E3.13.24.0", {"center": v(-0.37, 25.9) * mm, "radius": 0.25 * mm});
            skCircle(sketch, "E3.13.25.0", {"center": v(-0.37, 26.9) * mm, "radius": 0.25 * mm});
            skCircle(sketch, "E3.13.26.0", {"center": v(-0.37, 27.9) * mm, "radius": 0.25 * mm});
            skCircle(sketch, "E3.13.27.0", {"center": v(-0.37, 28.9) * mm, "radius": 0.25 * mm});
            skCircle(sketch, "E3.13.28.0", {"center": v(-0.37, 29.9) * mm, "radius": 0.25 * mm});
            skCircle(sketch, "E3.14.0.0", {"center": v(0.63, 1.9) * mm, "radius": 0.25 * mm});
            skCircle(sketch, "E3.14.1.0", {"center": v(0.63, 2.9) * mm, "radius": 0.25 * mm});
            skCircle(sketch, "E3.14.2.0", {"center": v(0.63, 3.9) * mm, "radius": 0.25 * mm});
            skCircle(sketch, "E3.14.3.0", {"center": v(0.63, 4.9) * mm, "radius": 0.25 * mm});
            skCircle(sketch, "E3.14.4.0", {"center": v(0.63, 5.9) * mm, "radius": 0.25 * mm});
            skCircle(sketch, "E3.14.5.0", {"center": v(0.63, 6.9) * mm, "radius": 0.25 * mm});
            skCircle(sketch, "E3.14.6.0", {"center": v(0.63, 7.9) * mm, "radius": 0.25 * mm});
            skCircle(sketch, "E3.14.7.0", {"center": v(0.63, 8.9) * mm, "radius": 0.25 * mm});
            skCircle(sketch, "E3.14.8.0", {"center": v(0.63, 9.9) * mm, "radius": 0.25 * mm});
            skCircle(sketch, "E3.14.9.0", {"center": v(0.63, 10.9) * mm, "radius": 0.25 * mm});
            skCircle(sketch, "E3.14.10.0", {"center": v(0.63, 11.9) * mm, "radius": 0.25 * mm});
            skCircle(sketch, "E3.14.11.0", {"center": v(0.63, 12.9) * mm, "radius": 0.25 * mm});
            skCircle(sketch, "E3.14.12.0", {"center": v(0.63, 13.9) * mm, "radius": 0.25 * mm});
            skCircle(sketch, "E3.14.13.0", {"center": v(0.63, 14.9) * mm, "radius": 0.25 * mm});
            skCircle(sketch, "E3.14.14.0", {"center": v(0.63, 15.9) * mm, "radius": 0.25 * mm});
            skCircle(sketch, "E3.14.15.0", {"center": v(0.63, 16.9) * mm, "radius": 0.25 * mm});
            skCircle(sketch, "E3.14.16.0", {"center": v(0.63, 17.9) * mm, "radius": 0.25 * mm});
            skCircle(sketch, "E3.14.17.0", {"center": v(0.63, 18.9) * mm, "radius": 0.25 * mm});
            skCircle(sketch, "E3.14.18.0", {"center": v(0.63, 19.9) * mm, "radius": 0.25 * mm});
            skCircle(sketch, "E3.14.19.0", {"center": v(0.63, 20.9) * mm, "radius": 0.25 * mm});
            skCircle(sketch, "E3.14.20.0", {"center": v(0.63, 21.9) * mm, "radius": 0.25 * mm});
            skCircle(sketch, "E3.14.21.0", {"center": v(0.63, 22.9) * mm, "radius": 0.25 * mm});
            skCircle(sketch, "E3.14.22.0", {"center": v(0.63, 23.9) * mm, "radius": 0.25 * mm});
            skCircle(sketch, "E3.14.23.0", {"center": v(0.63, 24.9) * mm, "radius": 0.25 * mm});
            skCircle(sketch, "E3.14.24.0", {"center": v(0.63, 25.9) * mm, "radius": 0.25 * mm});
            skCircle(sketch, "E3.14.25.0", {"center": v(0.63, 26.9) * mm, "radius": 0.25 * mm});
            skCircle(sketch, "E3.14.26.0", {"center": v(0.63, 27.9) * mm, "radius": 0.25 * mm});
            skCircle(sketch, "E3.14.27.0", {"center": v(0.63, 28.9) * mm, "radius": 0.25 * mm});
            skCircle(sketch, "E3.14.28.0", {"center": v(0.63, 29.9) * mm, "radius": 0.25 * mm});
            skCircle(sketch, "E3.15.0.0", {"center": v(1.63, 1.9) * mm, "radius": 0.25 * mm});
            skCircle(sketch, "E3.15.1.0", {"center": v(1.63, 2.9) * mm, "radius": 0.25 * mm});
            skCircle(sketch, "E3.15.2.0", {"center": v(1.63, 3.9) * mm, "radius": 0.25 * mm});
            skCircle(sketch, "E3.15.3.0", {"center": v(1.63, 4.9) * mm, "radius": 0.25 * mm});
            skCircle(sketch, "E3.15.4.0", {"center": v(1.63, 5.9) * mm, "radius": 0.25 * mm});
            skCircle(sketch, "E3.15.5.0", {"center": v(1.63, 6.9) * mm, "radius": 0.25 * mm});
            skCircle(sketch, "E3.15.6.0", {"center": v(1.63, 7.9) * mm, "radius": 0.25 * mm});
            skCircle(sketch, "E3.15.7.0", {"center": v(1.63, 8.9) * mm, "radius": 0.25 * mm});
            skCircle(sketch, "E3.15.8.0", {"center": v(1.63, 9.9) * mm, "radius": 0.25 * mm});
            skCircle(sketch, "E3.15.9.0", {"center": v(1.63, 10.9) * mm, "radius": 0.25 * mm});
            skCircle(sketch, "E3.15.10.0", {"center": v(1.63, 11.9) * mm, "radius": 0.25 * mm});
            skCircle(sketch, "E3.15.11.0", {"center": v(1.63, 12.9) * mm, "radius": 0.25 * mm});
            skCircle(sketch, "E3.15.12.0", {"center": v(1.63, 13.9) * mm, "radius": 0.25 * mm});
            skCircle(sketch, "E3.15.13.0", {"center": v(1.63, 14.9) * mm, "radius": 0.25 * mm});
            skCircle(sketch, "E3.15.14.0", {"center": v(1.63, 15.9) * mm, "radius": 0.25 * mm});
            skCircle(sketch, "E3.15.15.0", {"center": v(1.63, 16.9) * mm, "radius": 0.25 * mm});
            skCircle(sketch, "E3.15.16.0", {"center": v(1.63, 17.9) * mm, "radius": 0.25 * mm});
            skCircle(sketch, "E3.15.17.0", {"center": v(1.63, 18.9) * mm, "radius": 0.25 * mm});
            skCircle(sketch, "E3.15.18.0", {"center": v(1.63, 19.9) * mm, "radius": 0.25 * mm});
            skCircle(sketch, "E3.15.19.0", {"center": v(1.63, 20.9) * mm, "radius": 0.25 * mm});
            skCircle(sketch, "E3.15.20.0", {"center": v(1.63, 21.9) * mm, "radius": 0.25 * mm});
            skCircle(sketch, "E3.15.21.0", {"center": v(1.63, 22.9) * mm, "radius": 0.25 * mm});
            skCircle(sketch, "E3.15.22.0", {"center": v(1.63, 23.9) * mm, "radius": 0.25 * mm});
            skCircle(sketch, "E3.15.23.0", {"center": v(1.63, 24.9) * mm, "radius": 0.25 * mm});
            skCircle(sketch, "E3.15.24.0", {"center": v(1.63, 25.9) * mm, "radius": 0.25 * mm});
            skCircle(sketch, "E3.15.25.0", {"center": v(1.63, 26.9) * mm, "radius": 0.25 * mm});
            skCircle(sketch, "E3.15.26.0", {"center": v(1.63, 27.9) * mm, "radius": 0.25 * mm});
            skCircle(sketch, "E3.15.27.0", {"center": v(1.63, 28.9) * mm, "radius": 0.25 * mm});
            skCircle(sketch, "E3.15.28.0", {"center": v(1.63, 29.9) * mm, "radius": 0.25 * mm});
            skCircle(sketch, "E3.16.0.0", {"center": v(2.63, 1.9) * mm, "radius": 0.25 * mm});
            skCircle(sketch, "E3.16.1.0", {"center": v(2.63, 2.9) * mm, "radius": 0.25 * mm});
            skCircle(sketch, "E3.16.2.0", {"center": v(2.63, 3.9) * mm, "radius": 0.25 * mm});
            skCircle(sketch, "E3.16.3.0", {"center": v(2.63, 4.9) * mm, "radius": 0.25 * mm});
            skCircle(sketch, "E3.16.4.0", {"center": v(2.63, 5.9) * mm, "radius": 0.25 * mm});
            skCircle(sketch, "E3.16.5.0", {"center": v(2.63, 6.9) * mm, "radius": 0.25 * mm});
            skCircle(sketch, "E3.16.6.0", {"center": v(2.63, 7.9) * mm, "radius": 0.25 * mm});
            skCircle(sketch, "E3.16.7.0", {"center": v(2.63, 8.9) * mm, "radius": 0.25 * mm});
            skCircle(sketch, "E3.16.8.0", {"center": v(2.63, 9.9) * mm, "radius": 0.25 * mm});
            skCircle(sketch, "E3.16.9.0", {"center": v(2.63, 10.9) * mm, "radius": 0.25 * mm});
            skCircle(sketch, "E3.16.10.0", {"center": v(2.63, 11.9) * mm, "radius": 0.25 * mm});
            skCircle(sketch, "E3.16.11.0", {"center": v(2.63, 12.9) * mm, "radius": 0.25 * mm});
            skCircle(sketch, "E3.16.12.0", {"center": v(2.63, 13.9) * mm, "radius": 0.25 * mm});
            skCircle(sketch, "E3.16.13.0", {"center": v(2.63, 14.9) * mm, "radius": 0.25 * mm});
            skCircle(sketch, "E3.16.14.0", {"center": v(2.63, 15.9) * mm, "radius": 0.25 * mm});
            skCircle(sketch, "E3.16.15.0", {"center": v(2.63, 16.9) * mm, "radius": 0.25 * mm});
            skCircle(sketch, "E3.16.16.0", {"center": v(2.63, 17.9) * mm, "radius": 0.25 * mm});
            skCircle(sketch, "E3.16.17.0", {"center": v(2.63, 18.9) * mm, "radius": 0.25 * mm});
            skCircle(sketch, "E3.16.18.0", {"center": v(2.63, 19.9) * mm, "radius": 0.25 * mm});
            skCircle(sketch, "E3.16.19.0", {"center": v(2.63, 20.9) * mm, "radius": 0.25 * mm});
            skCircle(sketch, "E3.16.20.0", {"center": v(2.63, 21.9) * mm, "radius": 0.25 * mm});
            skCircle(sketch, "E3.16.21.0", {"center": v(2.63, 22.9) * mm, "radius": 0.25 * mm});
            skCircle(sketch, "E3.16.22.0", {"center": v(2.63, 23.9) * mm, "radius": 0.25 * mm});
            skCircle(sketch, "E3.16.23.0", {"center": v(2.63, 24.9) * mm, "radius": 0.25 * mm});
            skCircle(sketch, "E3.16.24.0", {"center": v(2.63, 25.9) * mm, "radius": 0.25 * mm});
            skCircle(sketch, "E3.16.25.0", {"center": v(2.63, 26.9) * mm, "radius": 0.25 * mm});
            skCircle(sketch, "E3.16.26.0", {"center": v(2.63, 27.9) * mm, "radius": 0.25 * mm});
            skCircle(sketch, "E3.16.27.0", {"center": v(2.63, 28.9) * mm, "radius": 0.25 * mm});
            skCircle(sketch, "E3.16.28.0", {"center": v(2.63, 29.9) * mm, "radius": 0.25 * mm});
            skCircle(sketch, "E3.17.0.0", {"center": v(3.63, 1.9) * mm, "radius": 0.25 * mm});
            skCircle(sketch, "E3.17.1.0", {"center": v(3.63, 2.9) * mm, "radius": 0.25 * mm});
            skCircle(sketch, "E3.17.2.0", {"center": v(3.63, 3.9) * mm, "radius": 0.25 * mm});
            skCircle(sketch, "E3.17.3.0", {"center": v(3.63, 4.9) * mm, "radius": 0.25 * mm});
            skCircle(sketch, "E3.17.4.0", {"center": v(3.63, 5.9) * mm, "radius": 0.25 * mm});
            skCircle(sketch, "E3.17.5.0", {"center": v(3.63, 6.9) * mm, "radius": 0.25 * mm});
            skCircle(sketch, "E3.17.6.0", {"center": v(3.63, 7.9) * mm, "radius": 0.25 * mm});
            skCircle(sketch, "E3.17.7.0", {"center": v(3.63, 8.9) * mm, "radius": 0.25 * mm});
            skCircle(sketch, "E3.17.8.0", {"center": v(3.63, 9.9) * mm, "radius": 0.25 * mm});
            skCircle(sketch, "E3.17.9.0", {"center": v(3.63, 10.9) * mm, "radius": 0.25 * mm});
            skCircle(sketch, "E3.17.10.0", {"center": v(3.63, 11.9) * mm, "radius": 0.25 * mm});
            skCircle(sketch, "E3.17.11.0", {"center": v(3.63, 12.9) * mm, "radius": 0.25 * mm});
            skCircle(sketch, "E3.17.12.0", {"center": v(3.63, 13.9) * mm, "radius": 0.25 * mm});
            skCircle(sketch, "E3.17.13.0", {"center": v(3.63, 14.9) * mm, "radius": 0.25 * mm});
            skCircle(sketch, "E3.17.14.0", {"center": v(3.63, 15.9) * mm, "radius": 0.25 * mm});
            skCircle(sketch, "E3.17.15.0", {"center": v(3.63, 16.9) * mm, "radius": 0.25 * mm});
            skCircle(sketch, "E3.17.16.0", {"center": v(3.63, 17.9) * mm, "radius": 0.25 * mm});
            skCircle(sketch, "E3.17.17.0", {"center": v(3.63, 18.9) * mm, "radius": 0.25 * mm});
            skCircle(sketch, "E3.17.18.0", {"center": v(3.63, 19.9) * mm, "radius": 0.25 * mm});
            skCircle(sketch, "E3.17.19.0", {"center": v(3.63, 20.9) * mm, "radius": 0.25 * mm});
            skCircle(sketch, "E3.17.20.0", {"center": v(3.63, 21.9) * mm, "radius": 0.25 * mm});
            skCircle(sketch, "E3.17.21.0", {"center": v(3.63, 22.9) * mm, "radius": 0.25 * mm});
            skCircle(sketch, "E3.17.22.0", {"center": v(3.63, 23.9) * mm, "radius": 0.25 * mm});
            skCircle(sketch, "E3.17.23.0", {"center": v(3.63, 24.9) * mm, "radius": 0.25 * mm});
            skCircle(sketch, "E3.17.24.0", {"center": v(3.63, 25.9) * mm, "radius": 0.25 * mm});
            skCircle(sketch, "E3.17.25.0", {"center": v(3.63, 26.9) * mm, "radius": 0.25 * mm});
            skCircle(sketch, "E3.17.26.0", {"center": v(3.63, 27.9) * mm, "radius": 0.25 * mm});
            skCircle(sketch, "E3.17.27.0", {"center": v(3.63, 28.9) * mm, "radius": 0.25 * mm});
            skCircle(sketch, "E3.17.28.0", {"center": v(3.63, 29.9) * mm, "radius": 0.25 * mm});
            skCircle(sketch, "E3.18.0.0", {"center": v(4.63, 1.9) * mm, "radius": 0.25 * mm});
            skCircle(sketch, "E3.18.1.0", {"center": v(4.63, 2.9) * mm, "radius": 0.25 * mm});
            skCircle(sketch, "E3.18.2.0", {"center": v(4.63, 3.9) * mm, "radius": 0.25 * mm});
            skCircle(sketch, "E3.18.3.0", {"center": v(4.63, 4.9) * mm, "radius": 0.25 * mm});
            skCircle(sketch, "E3.18.4.0", {"center": v(4.63, 5.9) * mm, "radius": 0.25 * mm});
            skCircle(sketch, "E3.18.5.0", {"center": v(4.63, 6.9) * mm, "radius": 0.25 * mm});
            skCircle(sketch, "E3.18.6.0", {"center": v(4.63, 7.9) * mm, "radius": 0.25 * mm});
            skCircle(sketch, "E3.18.7.0", {"center": v(4.63, 8.9) * mm, "radius": 0.25 * mm});
            skCircle(sketch, "E3.18.8.0", {"center": v(4.63, 9.9) * mm, "radius": 0.25 * mm});
            skCircle(sketch, "E3.18.9.0", {"center": v(4.63, 10.9) * mm, "radius": 0.25 * mm});
            skCircle(sketch, "E3.18.10.0", {"center": v(4.63, 11.9) * mm, "radius": 0.25 * mm});
            skCircle(sketch, "E3.18.11.0", {"center": v(4.63, 12.9) * mm, "radius": 0.25 * mm});
            skCircle(sketch, "E3.18.12.0", {"center": v(4.63, 13.9) * mm, "radius": 0.25 * mm});
            skCircle(sketch, "E3.18.13.0", {"center": v(4.63, 14.9) * mm, "radius": 0.25 * mm});
            skCircle(sketch, "E3.18.14.0", {"center": v(4.63, 15.9) * mm, "radius": 0.25 * mm});
            skCircle(sketch, "E3.18.15.0", {"center": v(4.63, 16.9) * mm, "radius": 0.25 * mm});
            skCircle(sketch, "E3.18.16.0", {"center": v(4.63, 17.9) * mm, "radius": 0.25 * mm});
            skCircle(sketch, "E3.18.17.0", {"center": v(4.63, 18.9) * mm, "radius": 0.25 * mm});
            skCircle(sketch, "E3.18.18.0", {"center": v(4.63, 19.9) * mm, "radius": 0.25 * mm});
            skCircle(sketch, "E3.18.19.0", {"center": v(4.63, 20.9) * mm, "radius": 0.25 * mm});
            skCircle(sketch, "E3.18.20.0", {"center": v(4.63, 21.9) * mm, "radius": 0.25 * mm});
            skCircle(sketch, "E3.18.21.0", {"center": v(4.63, 22.9) * mm, "radius": 0.25 * mm});
            skCircle(sketch, "E3.18.22.0", {"center": v(4.63, 23.9) * mm, "radius": 0.25 * mm});
            skCircle(sketch, "E3.18.23.0", {"center": v(4.63, 24.9) * mm, "radius": 0.25 * mm});
            skCircle(sketch, "E3.18.24.0", {"center": v(4.63, 25.9) * mm, "radius": 0.25 * mm});
            skCircle(sketch, "E3.18.25.0", {"center": v(4.63, 26.9) * mm, "radius": 0.25 * mm});
            skCircle(sketch, "E3.18.26.0", {"center": v(4.63, 27.9) * mm, "radius": 0.25 * mm});
            skCircle(sketch, "E3.18.27.0", {"center": v(4.63, 28.9) * mm, "radius": 0.25 * mm});
            skCircle(sketch, "E3.18.28.0", {"center": v(4.63, 29.9) * mm, "radius": 0.25 * mm});
            skCircle(sketch, "E3.19.0.0", {"center": v(5.63, 1.9) * mm, "radius": 0.25 * mm});
            skCircle(sketch, "E3.19.1.0", {"center": v(5.63, 2.9) * mm, "radius": 0.25 * mm});
            skCircle(sketch, "E3.19.2.0", {"center": v(5.63, 3.9) * mm, "radius": 0.25 * mm});
            skCircle(sketch, "E3.19.3.0", {"center": v(5.63, 4.9) * mm, "radius": 0.25 * mm});
            skCircle(sketch, "E3.19.4.0", {"center": v(5.63, 5.9) * mm, "radius": 0.25 * mm});
            skCircle(sketch, "E3.19.5.0", {"center": v(5.63, 6.9) * mm, "radius": 0.25 * mm});
            skCircle(sketch, "E3.19.6.0", {"center": v(5.63, 7.9) * mm, "radius": 0.25 * mm});
            skCircle(sketch, "E3.19.7.0", {"center": v(5.63, 8.9) * mm, "radius": 0.25 * mm});
            skCircle(sketch, "E3.19.8.0", {"center": v(5.63, 9.9) * mm, "radius": 0.25 * mm});
            skCircle(sketch, "E3.19.9.0", {"center": v(5.63, 10.9) * mm, "radius": 0.25 * mm});
            skCircle(sketch, "E3.19.10.0", {"center": v(5.63, 11.9) * mm, "radius": 0.25 * mm});
            skCircle(sketch, "E3.19.11.0", {"center": v(5.63, 12.9) * mm, "radius": 0.25 * mm});
            skCircle(sketch, "E3.19.12.0", {"center": v(5.63, 13.9) * mm, "radius": 0.25 * mm});
            skCircle(sketch, "E3.19.13.0", {"center": v(5.63, 14.9) * mm, "radius": 0.25 * mm});
            skCircle(sketch, "E3.19.14.0", {"center": v(5.63, 15.9) * mm, "radius": 0.25 * mm});
            skCircle(sketch, "E3.19.15.0", {"center": v(5.63, 16.9) * mm, "radius": 0.25 * mm});
            skCircle(sketch, "E3.19.16.0", {"center": v(5.63, 17.9) * mm, "radius": 0.25 * mm});
            skCircle(sketch, "E3.19.17.0", {"center": v(5.63, 18.9) * mm, "radius": 0.25 * mm});
            skCircle(sketch, "E3.19.18.0", {"center": v(5.63, 19.9) * mm, "radius": 0.25 * mm});
            skCircle(sketch, "E3.19.19.0", {"center": v(5.63, 20.9) * mm, "radius": 0.25 * mm});
            skCircle(sketch, "E3.19.20.0", {"center": v(5.63, 21.9) * mm, "radius": 0.25 * mm});
            skCircle(sketch, "E3.19.21.0", {"center": v(5.63, 22.9) * mm, "radius": 0.25 * mm});
            skCircle(sketch, "E3.19.22.0", {"center": v(5.63, 23.9) * mm, "radius": 0.25 * mm});
            skCircle(sketch, "E3.19.23.0", {"center": v(5.63, 24.9) * mm, "radius": 0.25 * mm});
            skCircle(sketch, "E3.19.24.0", {"center": v(5.63, 25.9) * mm, "radius": 0.25 * mm});
            skCircle(sketch, "E3.19.25.0", {"center": v(5.63, 26.9) * mm, "radius": 0.25 * mm});
            skCircle(sketch, "E3.19.26.0", {"center": v(5.63, 27.9) * mm, "radius": 0.25 * mm});
            skCircle(sketch, "E3.19.27.0", {"center": v(5.63, 28.9) * mm, "radius": 0.25 * mm});
            skCircle(sketch, "E3.19.28.0", {"center": v(5.63, 29.9) * mm, "radius": 0.25 * mm});
            skCircle(sketch, "E3.20.0.0", {"center": v(6.63, 1.9) * mm, "radius": 0.25 * mm});
            skCircle(sketch, "E3.20.1.0", {"center": v(6.63, 2.9) * mm, "radius": 0.25 * mm});
            skCircle(sketch, "E3.20.2.0", {"center": v(6.63, 3.9) * mm, "radius": 0.25 * mm});
            skCircle(sketch, "E3.20.3.0", {"center": v(6.63, 4.9) * mm, "radius": 0.25 * mm});
            skCircle(sketch, "E3.20.4.0", {"center": v(6.63, 5.9) * mm, "radius": 0.25 * mm});
            skCircle(sketch, "E3.20.5.0", {"center": v(6.63, 6.9) * mm, "radius": 0.25 * mm});
            skCircle(sketch, "E3.20.6.0", {"center": v(6.63, 7.9) * mm, "radius": 0.25 * mm});
            skCircle(sketch, "E3.20.7.0", {"center": v(6.63, 8.9) * mm, "radius": 0.25 * mm});
            skCircle(sketch, "E3.20.8.0", {"center": v(6.63, 9.9) * mm, "radius": 0.25 * mm});
            skCircle(sketch, "E3.20.9.0", {"center": v(6.63, 10.9) * mm, "radius": 0.25 * mm});
            skCircle(sketch, "E3.20.10.0", {"center": v(6.63, 11.9) * mm, "radius": 0.25 * mm});
            skCircle(sketch, "E3.20.11.0", {"center": v(6.63, 12.9) * mm, "radius": 0.25 * mm});
            skCircle(sketch, "E3.20.12.0", {"center": v(6.63, 13.9) * mm, "radius": 0.25 * mm});
            skCircle(sketch, "E3.20.13.0", {"center": v(6.63, 14.9) * mm, "radius": 0.25 * mm});
            skCircle(sketch, "E3.20.14.0", {"center": v(6.63, 15.9) * mm, "radius": 0.25 * mm});
            skCircle(sketch, "E3.20.15.0", {"center": v(6.63, 16.9) * mm, "radius": 0.25 * mm});
            skCircle(sketch, "E3.20.16.0", {"center": v(6.63, 17.9) * mm, "radius": 0.25 * mm});
            skCircle(sketch, "E3.20.17.0", {"center": v(6.63, 18.9) * mm, "radius": 0.25 * mm});
            skCircle(sketch, "E3.20.18.0", {"center": v(6.63, 19.9) * mm, "radius": 0.25 * mm});
            skCircle(sketch, "E3.20.19.0", {"center": v(6.63, 20.9) * mm, "radius": 0.25 * mm});
            skCircle(sketch, "E3.20.20.0", {"center": v(6.63, 21.9) * mm, "radius": 0.25 * mm});
            skCircle(sketch, "E3.20.21.0", {"center": v(6.63, 22.9) * mm, "radius": 0.25 * mm});
            skCircle(sketch, "E3.20.22.0", {"center": v(6.63, 23.9) * mm, "radius": 0.25 * mm});
            skCircle(sketch, "E3.20.23.0", {"center": v(6.63, 24.9) * mm, "radius": 0.25 * mm});
            skCircle(sketch, "E3.20.24.0", {"center": v(6.63, 25.9) * mm, "radius": 0.25 * mm});
            skCircle(sketch, "E3.20.25.0", {"center": v(6.63, 26.9) * mm, "radius": 0.25 * mm});
            skCircle(sketch, "E3.20.26.0", {"center": v(6.63, 27.9) * mm, "radius": 0.25 * mm});
            skCircle(sketch, "E3.20.27.0", {"center": v(6.63, 28.9) * mm, "radius": 0.25 * mm});
            skCircle(sketch, "E3.20.28.0", {"center": v(6.63, 29.9) * mm, "radius": 0.25 * mm});
            skCircle(sketch, "E3.21.0.0", {"center": v(7.63, 1.9) * mm, "radius": 0.25 * mm});
            skCircle(sketch, "E3.21.1.0", {"center": v(7.63, 2.9) * mm, "radius": 0.25 * mm});
            skCircle(sketch, "E3.21.2.0", {"center": v(7.63, 3.9) * mm, "radius": 0.25 * mm});
            skCircle(sketch, "E3.21.3.0", {"center": v(7.63, 4.9) * mm, "radius": 0.25 * mm});
            skCircle(sketch, "E3.21.4.0", {"center": v(7.63, 5.9) * mm, "radius": 0.25 * mm});
            skCircle(sketch, "E3.21.5.0", {"center": v(7.63, 6.9) * mm, "radius": 0.25 * mm});
            skCircle(sketch, "E3.21.6.0", {"center": v(7.63, 7.9) * mm, "radius": 0.25 * mm});
            skCircle(sketch, "E3.21.7.0", {"center": v(7.63, 8.9) * mm, "radius": 0.25 * mm});
            skCircle(sketch, "E3.21.8.0", {"center": v(7.63, 9.9) * mm, "radius": 0.25 * mm});
            skCircle(sketch, "E3.21.9.0", {"center": v(7.63, 10.9) * mm, "radius": 0.25 * mm});
            skCircle(sketch, "E3.21.10.0", {"center": v(7.63, 11.9) * mm, "radius": 0.25 * mm});
            skCircle(sketch, "E3.21.11.0", {"center": v(7.63, 12.9) * mm, "radius": 0.25 * mm});
            skCircle(sketch, "E3.21.12.0", {"center": v(7.63, 13.9) * mm, "radius": 0.25 * mm});
            skCircle(sketch, "E3.21.13.0", {"center": v(7.63, 14.9) * mm, "radius": 0.25 * mm});
            skCircle(sketch, "E3.21.14.0", {"center": v(7.63, 15.9) * mm, "radius": 0.25 * mm});
            skCircle(sketch, "E3.21.15.0", {"center": v(7.63, 16.9) * mm, "radius": 0.25 * mm});
            skCircle(sketch, "E3.21.16.0", {"center": v(7.63, 17.9) * mm, "radius": 0.25 * mm});
            skCircle(sketch, "E3.21.17.0", {"center": v(7.63, 18.9) * mm, "radius": 0.25 * mm});
            skCircle(sketch, "E3.21.18.0", {"center": v(7.63, 19.9) * mm, "radius": 0.25 * mm});
            skCircle(sketch, "E3.21.19.0", {"center": v(7.63, 20.9) * mm, "radius": 0.25 * mm});
            skCircle(sketch, "E3.21.20.0", {"center": v(7.63, 21.9) * mm, "radius": 0.25 * mm});
            skCircle(sketch, "E3.21.21.0", {"center": v(7.63, 22.9) * mm, "radius": 0.25 * mm});
            skCircle(sketch, "E3.21.22.0", {"center": v(7.63, 23.9) * mm, "radius": 0.25 * mm});
            skCircle(sketch, "E3.21.23.0", {"center": v(7.63, 24.9) * mm, "radius": 0.25 * mm});
            skCircle(sketch, "E3.21.24.0", {"center": v(7.63, 25.9) * mm, "radius": 0.25 * mm});
            skCircle(sketch, "E3.21.25.0", {"center": v(7.63, 26.9) * mm, "radius": 0.25 * mm});
            skCircle(sketch, "E3.21.26.0", {"center": v(7.63, 27.9) * mm, "radius": 0.25 * mm});
            skCircle(sketch, "E3.21.27.0", {"center": v(7.63, 28.9) * mm, "radius": 0.25 * mm});
            skCircle(sketch, "E3.21.28.0", {"center": v(7.63, 29.9) * mm, "radius": 0.25 * mm});
            skCircle(sketch, "E3.22.0.0", {"center": v(8.63, 1.9) * mm, "radius": 0.25 * mm});
            skCircle(sketch, "E3.22.1.0", {"center": v(8.63, 2.9) * mm, "radius": 0.25 * mm});
            skCircle(sketch, "E3.22.2.0", {"center": v(8.63, 3.9) * mm, "radius": 0.25 * mm});
            skCircle(sketch, "E3.22.3.0", {"center": v(8.63, 4.9) * mm, "radius": 0.25 * mm});
            skCircle(sketch, "E3.22.4.0", {"center": v(8.63, 5.9) * mm, "radius": 0.25 * mm});
            skCircle(sketch, "E3.22.5.0", {"center": v(8.63, 6.9) * mm, "radius": 0.25 * mm});
            skCircle(sketch, "E3.22.6.0", {"center": v(8.63, 7.9) * mm, "radius": 0.25 * mm});
            skCircle(sketch, "E3.22.7.0", {"center": v(8.63, 8.9) * mm, "radius": 0.25 * mm});
            skCircle(sketch, "E3.22.8.0", {"center": v(8.63, 9.9) * mm, "radius": 0.25 * mm});
            skCircle(sketch, "E3.22.9.0", {"center": v(8.63, 10.9) * mm, "radius": 0.25 * mm});
            skCircle(sketch, "E3.22.10.0", {"center": v(8.63, 11.9) * mm, "radius": 0.25 * mm});
            skCircle(sketch, "E3.22.11.0", {"center": v(8.63, 12.9) * mm, "radius": 0.25 * mm});
            skCircle(sketch, "E3.22.12.0", {"center": v(8.63, 13.9) * mm, "radius": 0.25 * mm});
            skCircle(sketch, "E3.22.13.0", {"center": v(8.63, 14.9) * mm, "radius": 0.25 * mm});
            skCircle(sketch, "E3.22.14.0", {"center": v(8.63, 15.9) * mm, "radius": 0.25 * mm});
            skCircle(sketch, "E3.22.15.0", {"center": v(8.63, 16.9) * mm, "radius": 0.25 * mm});
            skCircle(sketch, "E3.22.16.0", {"center": v(8.63, 17.9) * mm, "radius": 0.25 * mm});
            skCircle(sketch, "E3.22.17.0", {"center": v(8.63, 18.9) * mm, "radius": 0.25 * mm});
            skCircle(sketch, "E3.22.18.0", {"center": v(8.63, 19.9) * mm, "radius": 0.25 * mm});
            skCircle(sketch, "E3.22.19.0", {"center": v(8.63, 20.9) * mm, "radius": 0.25 * mm});
            skCircle(sketch, "E3.22.20.0", {"center": v(8.63, 21.9) * mm, "radius": 0.25 * mm});
            skCircle(sketch, "E3.22.21.0", {"center": v(8.63, 22.9) * mm, "radius": 0.25 * mm});
            skCircle(sketch, "E3.22.22.0", {"center": v(8.63, 23.9) * mm, "radius": 0.25 * mm});
            skCircle(sketch, "E3.22.23.0", {"center": v(8.63, 24.9) * mm, "radius": 0.25 * mm});
            skCircle(sketch, "E3.22.24.0", {"center": v(8.63, 25.9) * mm, "radius": 0.25 * mm});
            skCircle(sketch, "E3.22.25.0", {"center": v(8.63, 26.9) * mm, "radius": 0.25 * mm});
            skCircle(sketch, "E3.22.26.0", {"center": v(8.63, 27.9) * mm, "radius": 0.25 * mm});
            skCircle(sketch, "E3.22.27.0", {"center": v(8.63, 28.9) * mm, "radius": 0.25 * mm});
            skCircle(sketch, "E3.22.28.0", {"center": v(8.63, 29.9) * mm, "radius": 0.25 * mm});
            skCircle(sketch, "E3.23.0.0", {"center": v(9.63, 1.9) * mm, "radius": 0.25 * mm});
            skCircle(sketch, "E3.23.1.0", {"center": v(9.63, 2.9) * mm, "radius": 0.25 * mm});
            skCircle(sketch, "E3.23.2.0", {"center": v(9.63, 3.9) * mm, "radius": 0.25 * mm});
            skCircle(sketch, "E3.23.3.0", {"center": v(9.63, 4.9) * mm, "radius": 0.25 * mm});
            skCircle(sketch, "E3.23.4.0", {"center": v(9.63, 5.9) * mm, "radius": 0.25 * mm});
            skCircle(sketch, "E3.23.5.0", {"center": v(9.63, 6.9) * mm, "radius": 0.25 * mm});
            skCircle(sketch, "E3.23.6.0", {"center": v(9.63, 7.9) * mm, "radius": 0.25 * mm});
            skCircle(sketch, "E3.23.7.0", {"center": v(9.63, 8.9) * mm, "radius": 0.25 * mm});
            skCircle(sketch, "E3.23.8.0", {"center": v(9.63, 9.9) * mm, "radius": 0.25 * mm});
            skCircle(sketch, "E3.23.9.0", {"center": v(9.63, 10.9) * mm, "radius": 0.25 * mm});
            skCircle(sketch, "E3.23.10.0", {"center": v(9.63, 11.9) * mm, "radius": 0.25 * mm});
            skCircle(sketch, "E3.23.11.0", {"center": v(9.63, 12.9) * mm, "radius": 0.25 * mm});
            skCircle(sketch, "E3.23.12.0", {"center": v(9.63, 13.9) * mm, "radius": 0.25 * mm});
            skCircle(sketch, "E3.23.13.0", {"center": v(9.63, 14.9) * mm, "radius": 0.25 * mm});
            skCircle(sketch, "E3.23.14.0", {"center": v(9.63, 15.9) * mm, "radius": 0.25 * mm});
            skCircle(sketch, "E3.23.15.0", {"center": v(9.63, 16.9) * mm, "radius": 0.25 * mm});
            skCircle(sketch, "E3.23.16.0", {"center": v(9.63, 17.9) * mm, "radius": 0.25 * mm});
            skCircle(sketch, "E3.23.17.0", {"center": v(9.63, 18.9) * mm, "radius": 0.25 * mm});
            skCircle(sketch, "E3.23.18.0", {"center": v(9.63, 19.9) * mm, "radius": 0.25 * mm});
            skCircle(sketch, "E3.23.19.0", {"center": v(9.63, 20.9) * mm, "radius": 0.25 * mm});
            skCircle(sketch, "E3.23.20.0", {"center": v(9.63, 21.9) * mm, "radius": 0.25 * mm});
            skCircle(sketch, "E3.23.21.0", {"center": v(9.63, 22.9) * mm, "radius": 0.25 * mm});
            skCircle(sketch, "E3.23.22.0", {"center": v(9.63, 23.9) * mm, "radius": 0.25 * mm});
            skCircle(sketch, "E3.23.23.0", {"center": v(9.63, 24.9) * mm, "radius": 0.25 * mm});
            skCircle(sketch, "E3.23.24.0", {"center": v(9.63, 25.9) * mm, "radius": 0.25 * mm});
            skCircle(sketch, "E3.23.25.0", {"center": v(9.63, 26.9) * mm, "radius": 0.25 * mm});
            skCircle(sketch, "E3.23.26.0", {"center": v(9.63, 27.9) * mm, "radius": 0.25 * mm});
            skCircle(sketch, "E3.23.27.0", {"center": v(9.63, 28.9) * mm, "radius": 0.25 * mm});
            skCircle(sketch, "E3.23.28.0", {"center": v(9.63, 29.9) * mm, "radius": 0.25 * mm});
            skCircle(sketch, "E3.24.0.0", {"center": v(10.63, 1.9) * mm, "radius": 0.25 * mm});
            skCircle(sketch, "E3.24.1.0", {"center": v(10.63, 2.9) * mm, "radius": 0.25 * mm});
            skCircle(sketch, "E3.24.2.0", {"center": v(10.63, 3.9) * mm, "radius": 0.25 * mm});
            skCircle(sketch, "E3.24.3.0", {"center": v(10.63, 4.9) * mm, "radius": 0.25 * mm});
            skCircle(sketch, "E3.24.4.0", {"center": v(10.63, 5.9) * mm, "radius": 0.25 * mm});
            skCircle(sketch, "E3.24.5.0", {"center": v(10.63, 6.9) * mm, "radius": 0.25 * mm});
            skCircle(sketch, "E3.24.6.0", {"center": v(10.63, 7.9) * mm, "radius": 0.25 * mm});
            skCircle(sketch, "E3.24.7.0", {"center": v(10.63, 8.9) * mm, "radius": 0.25 * mm});
            skCircle(sketch, "E3.24.8.0", {"center": v(10.63, 9.9) * mm, "radius": 0.25 * mm});
            skCircle(sketch, "E3.24.9.0", {"center": v(10.63, 10.9) * mm, "radius": 0.25 * mm});
            skCircle(sketch, "E3.24.10.0", {"center": v(10.63, 11.9) * mm, "radius": 0.25 * mm});
            skCircle(sketch, "E3.24.11.0", {"center": v(10.63, 12.9) * mm, "radius": 0.25 * mm});
            skCircle(sketch, "E3.24.12.0", {"center": v(10.63, 13.9) * mm, "radius": 0.25 * mm});
            skCircle(sketch, "E3.24.13.0", {"center": v(10.63, 14.9) * mm, "radius": 0.25 * mm});
            skCircle(sketch, "E3.24.14.0", {"center": v(10.63, 15.9) * mm, "radius": 0.25 * mm});
            skCircle(sketch, "E3.24.15.0", {"center": v(10.63, 16.9) * mm, "radius": 0.25 * mm});
            skCircle(sketch, "E3.24.16.0", {"center": v(10.63, 17.9) * mm, "radius": 0.25 * mm});
            skCircle(sketch, "E3.24.17.0", {"center": v(10.63, 18.9) * mm, "radius": 0.25 * mm});
            skCircle(sketch, "E3.24.18.0", {"center": v(10.63, 19.9) * mm, "radius": 0.25 * mm});
            skCircle(sketch, "E3.24.19.0", {"center": v(10.63, 20.9) * mm, "radius": 0.25 * mm});
            skCircle(sketch, "E3.24.20.0", {"center": v(10.63, 21.9) * mm, "radius": 0.25 * mm});
            skCircle(sketch, "E3.24.21.0", {"center": v(10.63, 22.9) * mm, "radius": 0.25 * mm});
            skCircle(sketch, "E3.24.22.0", {"center": v(10.63, 23.9) * mm, "radius": 0.25 * mm});
            skCircle(sketch, "E3.24.23.0", {"center": v(10.63, 24.9) * mm, "radius": 0.25 * mm});
            skCircle(sketch, "E3.24.24.0", {"center": v(10.63, 25.9) * mm, "radius": 0.25 * mm});
            skCircle(sketch, "E3.24.25.0", {"center": v(10.63, 26.9) * mm, "radius": 0.25 * mm});
            skCircle(sketch, "E3.24.26.0", {"center": v(10.63, 27.9) * mm, "radius": 0.25 * mm});
            skCircle(sketch, "E3.24.27.0", {"center": v(10.63, 28.9) * mm, "radius": 0.25 * mm});
            skCircle(sketch, "E3.24.28.0", {"center": v(10.63, 29.9) * mm, "radius": 0.25 * mm});
            skCircle(sketch, "E3.25.0.0", {"center": v(11.63, 1.9) * mm, "radius": 0.25 * mm});
            skCircle(sketch, "E3.25.1.0", {"center": v(11.63, 2.9) * mm, "radius": 0.25 * mm});
            skCircle(sketch, "E3.25.2.0", {"center": v(11.63, 3.9) * mm, "radius": 0.25 * mm});
            skCircle(sketch, "E3.25.3.0", {"center": v(11.63, 4.9) * mm, "radius": 0.25 * mm});
            skCircle(sketch, "E3.25.4.0", {"center": v(11.63, 5.9) * mm, "radius": 0.25 * mm});
            skCircle(sketch, "E3.25.5.0", {"center": v(11.63, 6.9) * mm, "radius": 0.25 * mm});
            skCircle(sketch, "E3.25.6.0", {"center": v(11.63, 7.9) * mm, "radius": 0.25 * mm});
            skCircle(sketch, "E3.25.7.0", {"center": v(11.63, 8.9) * mm, "radius": 0.25 * mm});
            skCircle(sketch, "E3.25.8.0", {"center": v(11.63, 9.9) * mm, "radius": 0.25 * mm});
            skCircle(sketch, "E3.25.9.0", {"center": v(11.63, 10.9) * mm, "radius": 0.25 * mm});
            skCircle(sketch, "E3.25.10.0", {"center": v(11.63, 11.9) * mm, "radius": 0.25 * mm});
            skCircle(sketch, "E3.25.11.0", {"center": v(11.63, 12.9) * mm, "radius": 0.25 * mm});
            skCircle(sketch, "E3.25.12.0", {"center": v(11.63, 13.9) * mm, "radius": 0.25 * mm});
            skCircle(sketch, "E3.25.13.0", {"center": v(11.63, 14.9) * mm, "radius": 0.25 * mm});
            skCircle(sketch, "E3.25.14.0", {"center": v(11.63, 15.9) * mm, "radius": 0.25 * mm});
            skCircle(sketch, "E3.25.15.0", {"center": v(11.63, 16.9) * mm, "radius": 0.25 * mm});
            skCircle(sketch, "E3.25.16.0", {"center": v(11.63, 17.9) * mm, "radius": 0.25 * mm});
            skCircle(sketch, "E3.25.17.0", {"center": v(11.63, 18.9) * mm, "radius": 0.25 * mm});
            skCircle(sketch, "E3.25.18.0", {"center": v(11.63, 19.9) * mm, "radius": 0.25 * mm});
            skCircle(sketch, "E3.25.19.0", {"center": v(11.63, 20.9) * mm, "radius": 0.25 * mm});
            skCircle(sketch, "E3.25.20.0", {"center": v(11.63, 21.9) * mm, "radius": 0.25 * mm});
            skCircle(sketch, "E3.25.21.0", {"center": v(11.63, 22.9) * mm, "radius": 0.25 * mm});
            skCircle(sketch, "E3.25.22.0", {"center": v(11.63, 23.9) * mm, "radius": 0.25 * mm});
            skCircle(sketch, "E3.25.23.0", {"center": v(11.63, 24.9) * mm, "radius": 0.25 * mm});
            skCircle(sketch, "E3.25.24.0", {"center": v(11.63, 25.9) * mm, "radius": 0.25 * mm});
            skCircle(sketch, "E3.25.25.0", {"center": v(11.63, 26.9) * mm, "radius": 0.25 * mm});
            skCircle(sketch, "E3.25.26.0", {"center": v(11.63, 27.9) * mm, "radius": 0.25 * mm});
            skCircle(sketch, "E3.25.27.0", {"center": v(11.63, 28.9) * mm, "radius": 0.25 * mm});
            skCircle(sketch, "E3.25.28.0", {"center": v(11.63, 29.9) * mm, "radius": 0.25 * mm});
            skCircle(sketch, "E3.26.0.0", {"center": v(12.63, 1.9) * mm, "radius": 0.25 * mm});
            skCircle(sketch, "E3.26.1.0", {"center": v(12.63, 2.9) * mm, "radius": 0.25 * mm});
            skCircle(sketch, "E3.26.2.0", {"center": v(12.63, 3.9) * mm, "radius": 0.25 * mm});
            skCircle(sketch, "E3.26.3.0", {"center": v(12.63, 4.9) * mm, "radius": 0.25 * mm});
            skCircle(sketch, "E3.26.4.0", {"center": v(12.63, 5.9) * mm, "radius": 0.25 * mm});
            skCircle(sketch, "E3.26.5.0", {"center": v(12.63, 6.9) * mm, "radius": 0.25 * mm});
            skCircle(sketch, "E3.26.6.0", {"center": v(12.63, 7.9) * mm, "radius": 0.25 * mm});
            skCircle(sketch, "E3.26.7.0", {"center": v(12.63, 8.9) * mm, "radius": 0.25 * mm});
            skCircle(sketch, "E3.26.8.0", {"center": v(12.63, 9.9) * mm, "radius": 0.25 * mm});
            skCircle(sketch, "E3.26.9.0", {"center": v(12.63, 10.9) * mm, "radius": 0.25 * mm});
            skCircle(sketch, "E3.26.10.0", {"center": v(12.63, 11.9) * mm, "radius": 0.25 * mm});
            skCircle(sketch, "E3.26.11.0", {"center": v(12.63, 12.9) * mm, "radius": 0.25 * mm});
            skCircle(sketch, "E3.26.12.0", {"center": v(12.63, 13.9) * mm, "radius": 0.25 * mm});
            skCircle(sketch, "E3.26.13.0", {"center": v(12.63, 14.9) * mm, "radius": 0.25 * mm});
            skCircle(sketch, "E3.26.14.0", {"center": v(12.63, 15.9) * mm, "radius": 0.25 * mm});
            skCircle(sketch, "E3.26.15.0", {"center": v(12.63, 16.9) * mm, "radius": 0.25 * mm});
            skCircle(sketch, "E3.26.16.0", {"center": v(12.63, 17.9) * mm, "radius": 0.25 * mm});
            skCircle(sketch, "E3.26.17.0", {"center": v(12.63, 18.9) * mm, "radius": 0.25 * mm});
            skCircle(sketch, "E3.26.18.0", {"center": v(12.63, 19.9) * mm, "radius": 0.25 * mm});
            skCircle(sketch, "E3.26.19.0", {"center": v(12.63, 20.9) * mm, "radius": 0.25 * mm});
            skCircle(sketch, "E3.26.20.0", {"center": v(12.63, 21.9) * mm, "radius": 0.25 * mm});
            skCircle(sketch, "E3.26.21.0", {"center": v(12.63, 22.9) * mm, "radius": 0.25 * mm});
            skCircle(sketch, "E3.26.22.0", {"center": v(12.63, 23.9) * mm, "radius": 0.25 * mm});
            skCircle(sketch, "E3.26.23.0", {"center": v(12.63, 24.9) * mm, "radius": 0.25 * mm});
            skCircle(sketch, "E3.26.24.0", {"center": v(12.63, 25.9) * mm, "radius": 0.25 * mm});
            skCircle(sketch, "E3.26.25.0", {"center": v(12.63, 26.9) * mm, "radius": 0.25 * mm});
            skCircle(sketch, "E3.26.26.0", {"center": v(12.63, 27.9) * mm, "radius": 0.25 * mm});
            skCircle(sketch, "E3.26.27.0", {"center": v(12.63, 28.9) * mm, "radius": 0.25 * mm});
            skCircle(sketch, "E3.26.28.0", {"center": v(12.63, 29.9) * mm, "radius": 0.25 * mm});
            skCircle(sketch, "E3.27.0.0", {"center": v(13.63, 1.9) * mm, "radius": 0.25 * mm});
            skCircle(sketch, "E3.27.1.0", {"center": v(13.63, 2.9) * mm, "radius": 0.25 * mm});
            skCircle(sketch, "E3.27.2.0", {"center": v(13.63, 3.9) * mm, "radius": 0.25 * mm});
            skCircle(sketch, "E3.27.3.0", {"center": v(13.63, 4.9) * mm, "radius": 0.25 * mm});
            skCircle(sketch, "E3.27.4.0", {"center": v(13.63, 5.9) * mm, "radius": 0.25 * mm});
            skCircle(sketch, "E3.27.5.0", {"center": v(13.63, 6.9) * mm, "radius": 0.25 * mm});
            skCircle(sketch, "E3.27.6.0", {"center": v(13.63, 7.9) * mm, "radius": 0.25 * mm});
            skCircle(sketch, "E3.27.7.0", {"center": v(13.63, 8.9) * mm, "radius": 0.25 * mm});
            skCircle(sketch, "E3.27.8.0", {"center": v(13.63, 9.9) * mm, "radius": 0.25 * mm});
            skCircle(sketch, "E3.27.9.0", {"center": v(13.63, 10.9) * mm, "radius": 0.25 * mm});
            skCircle(sketch, "E3.27.10.0", {"center": v(13.63, 11.9) * mm, "radius": 0.25 * mm});
            skCircle(sketch, "E3.27.11.0", {"center": v(13.63, 12.9) * mm, "radius": 0.25 * mm});
            skCircle(sketch, "E3.27.12.0", {"center": v(13.63, 13.9) * mm, "radius": 0.25 * mm});
            skCircle(sketch, "E3.27.13.0", {"center": v(13.63, 14.9) * mm, "radius": 0.25 * mm});
            skCircle(sketch, "E3.27.14.0", {"center": v(13.63, 15.9) * mm, "radius": 0.25 * mm});
            skCircle(sketch, "E3.27.15.0", {"center": v(13.63, 16.9) * mm, "radius": 0.25 * mm});
            skCircle(sketch, "E3.27.16.0", {"center": v(13.63, 17.9) * mm, "radius": 0.25 * mm});
            skCircle(sketch, "E3.27.17.0", {"center": v(13.63, 18.9) * mm, "radius": 0.25 * mm});
            skCircle(sketch, "E3.27.18.0", {"center": v(13.63, 19.9) * mm, "radius": 0.25 * mm});
            skCircle(sketch, "E3.27.19.0", {"center": v(13.63, 20.9) * mm, "radius": 0.25 * mm});
            skCircle(sketch, "E3.27.20.0", {"center": v(13.63, 21.9) * mm, "radius": 0.25 * mm});
            skCircle(sketch, "E3.27.21.0", {"center": v(13.63, 22.9) * mm, "radius": 0.25 * mm});
            skCircle(sketch, "E3.27.22.0", {"center": v(13.63, 23.9) * mm, "radius": 0.25 * mm});
            skCircle(sketch, "E3.27.23.0", {"center": v(13.63, 24.9) * mm, "radius": 0.25 * mm});
            skCircle(sketch, "E3.27.24.0", {"center": v(13.63, 25.9) * mm, "radius": 0.25 * mm});
            skCircle(sketch, "E3.27.25.0", {"center": v(13.63, 26.9) * mm, "radius": 0.25 * mm});
            skCircle(sketch, "E3.27.26.0", {"center": v(13.63, 27.9) * mm, "radius": 0.25 * mm});
            skCircle(sketch, "E3.27.27.0", {"center": v(13.63, 28.9) * mm, "radius": 0.25 * mm});
            skCircle(sketch, "E3.27.28.0", {"center": v(13.63, 29.9) * mm, "radius": 0.25 * mm});
            skLineSegment(sketch, "E3.direction1", {"start": v(-13.37, 1.9) * mm, "end": v(-12.37, 1.9) * mm, "construction": true});
            skLineSegment(sketch, "E3.direction2", {"start": v(-13.37, 1.9) * mm, "end": v(-13.37, 2.9) * mm, "construction": true});
            skSolve(sketch);
        }
        {
            var Q0;
            Q0 = qSketchRegion(id + "F4", true);
            var Q1;
            Q1=makeQuery(id+"F1.opExtrude","SWEPT_FACE",FACE,{"disambiguationData":[OSD([sQuery(id+"F0.wireOp",EDGE,"E0.top")])]});
            extrude(context, id + "F5", {"entities" : qUnion([Q0, Q1]), "operationType" : NewBodyOperationType.REMOVE, "oppositeDirection" : true, "depth" : 40 * mm});
        }
        {
            var Q0;
            Q0=makeQuery(id+"F1.opExtrude","SWEPT_FACE",FACE,{"disambiguationData":[OSD([sQuery(id+"F0.wireOp",EDGE,"E0.left")])]});
            var sketch = newSketch(context, id + "F6", { "sketchPlane" : qUnion([Q0])});
            skCircle(sketch, "E4", {"center": v(-13.81, 1.65) * mm, "radius": 0.25 * mm});
            skCircle(sketch, "E5.0.1.0", {"center": v(-13.81, 2.65) * mm, "radius": 0.25 * mm});
            skCircle(sketch, "E5.0.2.0", {"center": v(-13.81, 3.65) * mm, "radius": 0.25 * mm});
            skCircle(sketch, "E5.0.3.0", {"center": v(-13.81, 4.65) * mm, "radius": 0.25 * mm});
            skCircle(sketch, "E5.0.4.0", {"center": v(-13.81, 5.65) * mm, "radius": 0.25 * mm});
            skCircle(sketch, "E5.0.5.0", {"center": v(-13.81, 6.65) * mm, "radius": 0.25 * mm});
            skCircle(sketch, "E5.0.6.0", {"center": v(-13.81, 7.65) * mm, "radius": 0.25 * mm});
            skCircle(sketch, "E5.0.7.0", {"center": v(-13.81, 8.65) * mm, "radius": 0.25 * mm});
            skCircle(sketch, "E5.0.8.0", {"center": v(-13.81, 9.65) * mm, "radius": 0.25 * mm});
            skCircle(sketch, "E5.0.9.0", {"center": v(-13.81, 10.65) * mm, "radius": 0.25 * mm});
            skCircle(sketch, "E5.0.10.0", {"center": v(-13.81, 11.65) * mm, "radius": 0.25 * mm});
            skCircle(sketch, "E5.0.11.0", {"center": v(-13.81, 12.65) * mm, "radius": 0.25 * mm});
            skCircle(sketch, "E5.0.12.0", {"center": v(-13.81, 13.65) * mm, "radius": 0.25 * mm});
            skCircle(sketch, "E5.0.13.0", {"center": v(-13.81, 14.65) * mm, "radius": 0.25 * mm});
            skCircle(sketch, "E5.0.14.0", {"center": v(-13.81, 15.65) * mm, "radius": 0.25 * mm});
            skCircle(sketch, "E5.0.15.0", {"center": v(-13.81, 16.65) * mm, "radius": 0.25 * mm});
            skCircle(sketch, "E5.0.16.0", {"center": v(-13.81, 17.65) * mm, "radius": 0.25 * mm});
            skCircle(sketch, "E5.0.17.0", {"center": v(-13.81, 18.65) * mm, "radius": 0.25 * mm});
            skCircle(sketch, "E5.0.18.0", {"center": v(-13.81, 19.65) * mm, "radius": 0.25 * mm});
            skCircle(sketch, "E5.0.19.0", {"center": v(-13.81, 20.65) * mm, "radius": 0.25 * mm});
            skCircle(sketch, "E5.0.20.0", {"center": v(-13.81, 21.65) * mm, "radius": 0.25 * mm});
            skCircle(sketch, "E5.0.21.0", {"center": v(-13.81, 22.65) * mm, "radius": 0.25 * mm});
            skCircle(sketch, "E5.0.22.0", {"center": v(-13.81, 23.65) * mm, "radius": 0.25 * mm});
            skCircle(sketch, "E5.0.23.0", {"center": v(-13.81, 24.65) * mm, "radius": 0.25 * mm});
            skCircle(sketch, "E5.0.24.0", {"center": v(-13.81, 25.65) * mm, "radius": 0.25 * mm});
            skCircle(sketch, "E5.0.25.0", {"center": v(-13.81, 26.65) * mm, "radius": 0.25 * mm});
            skCircle(sketch, "E5.0.26.0", {"center": v(-13.81, 27.65) * mm, "radius": 0.25 * mm});
            skCircle(sketch, "E5.0.27.0", {"center": v(-13.81, 28.65) * mm, "radius": 0.25 * mm});
            skCircle(sketch, "E5.0.28.0", {"center": v(-13.81, 29.65) * mm, "radius": 0.25 * mm});
            skCircle(sketch, "E5.1.0.0", {"center": v(-12.81, 1.65) * mm, "radius": 0.25 * mm});
            skCircle(sketch, "E5.1.1.0", {"center": v(-12.81, 2.65) * mm, "radius": 0.25 * mm});
            skCircle(sketch, "E5.1.2.0", {"center": v(-12.81, 3.65) * mm, "radius": 0.25 * mm});
            skCircle(sketch, "E5.1.3.0", {"center": v(-12.81, 4.65) * mm, "radius": 0.25 * mm});
            skCircle(sketch, "E5.1.4.0", {"center": v(-12.81, 5.65) * mm, "radius": 0.25 * mm});
            skCircle(sketch, "E5.1.5.0", {"center": v(-12.81, 6.65) * mm, "radius": 0.25 * mm});
            skCircle(sketch, "E5.1.6.0", {"center": v(-12.81, 7.65) * mm, "radius": 0.25 * mm});
            skCircle(sketch, "E5.1.7.0", {"center": v(-12.81, 8.65) * mm, "radius": 0.25 * mm});
            skCircle(sketch, "E5.1.8.0", {"center": v(-12.81, 9.65) * mm, "radius": 0.25 * mm});
            skCircle(sketch, "E5.1.9.0", {"center": v(-12.81, 10.65) * mm, "radius": 0.25 * mm});
            skCircle(sketch, "E5.1.10.0", {"center": v(-12.81, 11.65) * mm, "radius": 0.25 * mm});
            skCircle(sketch, "E5.1.11.0", {"center": v(-12.81, 12.65) * mm, "radius": 0.25 * mm});
            skCircle(sketch, "E5.1.12.0", {"center": v(-12.81, 13.65) * mm, "radius": 0.25 * mm});
            skCircle(sketch, "E5.1.13.0", {"center": v(-12.81, 14.65) * mm, "radius": 0.25 * mm});
            skCircle(sketch, "E5.1.14.0", {"center": v(-12.81, 15.65) * mm, "radius": 0.25 * mm});
            skCircle(sketch, "E5.1.15.0", {"center": v(-12.81, 16.65) * mm, "radius": 0.25 * mm});
            skCircle(sketch, "E5.1.16.0", {"center": v(-12.81, 17.65) * mm, "radius": 0.25 * mm});
            skCircle(sketch, "E5.1.17.0", {"center": v(-12.81, 18.65) * mm, "radius": 0.25 * mm});
            skCircle(sketch, "E5.1.18.0", {"center": v(-12.81, 19.65) * mm, "radius": 0.25 * mm});
            skCircle(sketch, "E5.1.19.0", {"center": v(-12.81, 20.65) * mm, "radius": 0.25 * mm});
            skCircle(sketch, "E5.1.20.0", {"center": v(-12.81, 21.65) * mm, "radius": 0.25 * mm});
            skCircle(sketch, "E5.1.21.0", {"center": v(-12.81, 22.65) * mm, "radius": 0.25 * mm});
            skCircle(sketch, "E5.1.22.0", {"center": v(-12.81, 23.65) * mm, "radius": 0.25 * mm});
            skCircle(sketch, "E5.1.23.0", {"center": v(-12.81, 24.65) * mm, "radius": 0.25 * mm});
            skCircle(sketch, "E5.1.24.0", {"center": v(-12.81, 25.65) * mm, "radius": 0.25 * mm});
            skCircle(sketch, "E5.1.25.0", {"center": v(-12.81, 26.65) * mm, "radius": 0.25 * mm});
            skCircle(sketch, "E5.1.26.0", {"center": v(-12.81, 27.65) * mm, "radius": 0.25 * mm});
            skCircle(sketch, "E5.1.27.0", {"center": v(-12.81, 28.65) * mm, "radius": 0.25 * mm});
            skCircle(sketch, "E5.1.28.0", {"center": v(-12.81, 29.65) * mm, "radius": 0.25 * mm});
            skCircle(sketch, "E5.2.0.0", {"center": v(-11.81, 1.65) * mm, "radius": 0.25 * mm});
            skCircle(sketch, "E5.2.1.0", {"center": v(-11.81, 2.65) * mm, "radius": 0.25 * mm});
            skCircle(sketch, "E5.2.2.0", {"center": v(-11.81, 3.65) * mm, "radius": 0.25 * mm});
            skCircle(sketch, "E5.2.3.0", {"center": v(-11.81, 4.65) * mm, "radius": 0.25 * mm});
            skCircle(sketch, "E5.2.4.0", {"center": v(-11.81, 5.65) * mm, "radius": 0.25 * mm});
            skCircle(sketch, "E5.2.5.0", {"center": v(-11.81, 6.65) * mm, "radius": 0.25 * mm});
            skCircle(sketch, "E5.2.6.0", {"center": v(-11.81, 7.65) * mm, "radius": 0.25 * mm});
            skCircle(sketch, "E5.2.7.0", {"center": v(-11.81, 8.65) * mm, "radius": 0.25 * mm});
            skCircle(sketch, "E5.2.8.0", {"center": v(-11.81, 9.65) * mm, "radius": 0.25 * mm});
            skCircle(sketch, "E5.2.9.0", {"center": v(-11.81, 10.65) * mm, "radius": 0.25 * mm});
            skCircle(sketch, "E5.2.10.0", {"center": v(-11.81, 11.65) * mm, "radius": 0.25 * mm});
            skCircle(sketch, "E5.2.11.0", {"center": v(-11.81, 12.65) * mm, "radius": 0.25 * mm});
            skCircle(sketch, "E5.2.12.0", {"center": v(-11.81, 13.65) * mm, "radius": 0.25 * mm});
            skCircle(sketch, "E5.2.13.0", {"center": v(-11.81, 14.65) * mm, "radius": 0.25 * mm});
            skCircle(sketch, "E5.2.14.0", {"center": v(-11.81, 15.65) * mm, "radius": 0.25 * mm});
            skCircle(sketch, "E5.2.15.0", {"center": v(-11.81, 16.65) * mm, "radius": 0.25 * mm});
            skCircle(sketch, "E5.2.16.0", {"center": v(-11.81, 17.65) * mm, "radius": 0.25 * mm});
            skCircle(sketch, "E5.2.17.0", {"center": v(-11.81, 18.65) * mm, "radius": 0.25 * mm});
            skCircle(sketch, "E5.2.18.0", {"center": v(-11.81, 19.65) * mm, "radius": 0.25 * mm});
            skCircle(sketch, "E5.2.19.0", {"center": v(-11.81, 20.65) * mm, "radius": 0.25 * mm});
            skCircle(sketch, "E5.2.20.0", {"center": v(-11.81, 21.65) * mm, "radius": 0.25 * mm});
            skCircle(sketch, "E5.2.21.0", {"center": v(-11.81, 22.65) * mm, "radius": 0.25 * mm});
            skCircle(sketch, "E5.2.22.0", {"center": v(-11.81, 23.65) * mm, "radius": 0.25 * mm});
            skCircle(sketch, "E5.2.23.0", {"center": v(-11.81, 24.65) * mm, "radius": 0.25 * mm});
            skCircle(sketch, "E5.2.24.0", {"center": v(-11.81, 25.65) * mm, "radius": 0.25 * mm});
            skCircle(sketch, "E5.2.25.0", {"center": v(-11.81, 26.65) * mm, "radius": 0.25 * mm});
            skCircle(sketch, "E5.2.26.0", {"center": v(-11.81, 27.65) * mm, "radius": 0.25 * mm});
            skCircle(sketch, "E5.2.27.0", {"center": v(-11.81, 28.65) * mm, "radius": 0.25 * mm});
            skCircle(sketch, "E5.2.28.0", {"center": v(-11.81, 29.65) * mm, "radius": 0.25 * mm});
            skCircle(sketch, "E5.3.0.0", {"center": v(-10.81, 1.65) * mm, "radius": 0.25 * mm});
            skCircle(sketch, "E5.3.1.0", {"center": v(-10.81, 2.65) * mm, "radius": 0.25 * mm});
            skCircle(sketch, "E5.3.2.0", {"center": v(-10.81, 3.65) * mm, "radius": 0.25 * mm});
            skCircle(sketch, "E5.3.3.0", {"center": v(-10.81, 4.65) * mm, "radius": 0.25 * mm});
            skCircle(sketch, "E5.3.4.0", {"center": v(-10.81, 5.65) * mm, "radius": 0.25 * mm});
            skCircle(sketch, "E5.3.5.0", {"center": v(-10.81, 6.65) * mm, "radius": 0.25 * mm});
            skCircle(sketch, "E5.3.6.0", {"center": v(-10.81, 7.65) * mm, "radius": 0.25 * mm});
            skCircle(sketch, "E5.3.7.0", {"center": v(-10.81, 8.65) * mm, "radius": 0.25 * mm});
            skCircle(sketch, "E5.3.8.0", {"center": v(-10.81, 9.65) * mm, "radius": 0.25 * mm});
            skCircle(sketch, "E5.3.9.0", {"center": v(-10.81, 10.65) * mm, "radius": 0.25 * mm});
            skCircle(sketch, "E5.3.10.0", {"center": v(-10.81, 11.65) * mm, "radius": 0.25 * mm});
            skCircle(sketch, "E5.3.11.0", {"center": v(-10.81, 12.65) * mm, "radius": 0.25 * mm});
            skCircle(sketch, "E5.3.12.0", {"center": v(-10.81, 13.65) * mm, "radius": 0.25 * mm});
            skCircle(sketch, "E5.3.13.0", {"center": v(-10.81, 14.65) * mm, "radius": 0.25 * mm});
            skCircle(sketch, "E5.3.14.0", {"center": v(-10.81, 15.65) * mm, "radius": 0.25 * mm});
            skCircle(sketch, "E5.3.15.0", {"center": v(-10.81, 16.65) * mm, "radius": 0.25 * mm});
            skCircle(sketch, "E5.3.16.0", {"center": v(-10.81, 17.65) * mm, "radius": 0.25 * mm});
            skCircle(sketch, "E5.3.17.0", {"center": v(-10.81, 18.65) * mm, "radius": 0.25 * mm});
            skCircle(sketch, "E5.3.18.0", {"center": v(-10.81, 19.65) * mm, "radius": 0.25 * mm});
            skCircle(sketch, "E5.3.19.0", {"center": v(-10.81, 20.65) * mm, "radius": 0.25 * mm});
            skCircle(sketch, "E5.3.20.0", {"center": v(-10.81, 21.65) * mm, "radius": 0.25 * mm});
            skCircle(sketch, "E5.3.21.0", {"center": v(-10.81, 22.65) * mm, "radius": 0.25 * mm});
            skCircle(sketch, "E5.3.22.0", {"center": v(-10.81, 23.65) * mm, "radius": 0.25 * mm});
            skCircle(sketch, "E5.3.23.0", {"center": v(-10.81, 24.65) * mm, "radius": 0.25 * mm});
            skCircle(sketch, "E5.3.24.0", {"center": v(-10.81, 25.65) * mm, "radius": 0.25 * mm});
            skCircle(sketch, "E5.3.25.0", {"center": v(-10.81, 26.65) * mm, "radius": 0.25 * mm});
            skCircle(sketch, "E5.3.26.0", {"center": v(-10.81, 27.65) * mm, "radius": 0.25 * mm});
            skCircle(sketch, "E5.3.27.0", {"center": v(-10.81, 28.65) * mm, "radius": 0.25 * mm});
            skCircle(sketch, "E5.3.28.0", {"center": v(-10.81, 29.65) * mm, "radius": 0.25 * mm});
            skCircle(sketch, "E5.4.0.0", {"center": v(-9.81, 1.65) * mm, "radius": 0.25 * mm});
            skCircle(sketch, "E5.4.1.0", {"center": v(-9.81, 2.65) * mm, "radius": 0.25 * mm});
            skCircle(sketch, "E5.4.2.0", {"center": v(-9.81, 3.65) * mm, "radius": 0.25 * mm});
            skCircle(sketch, "E5.4.3.0", {"center": v(-9.81, 4.65) * mm, "radius": 0.25 * mm});
            skCircle(sketch, "E5.4.4.0", {"center": v(-9.81, 5.65) * mm, "radius": 0.25 * mm});
            skCircle(sketch, "E5.4.5.0", {"center": v(-9.81, 6.65) * mm, "radius": 0.25 * mm});
            skCircle(sketch, "E5.4.6.0", {"center": v(-9.81, 7.65) * mm, "radius": 0.25 * mm});
            skCircle(sketch, "E5.4.7.0", {"center": v(-9.81, 8.65) * mm, "radius": 0.25 * mm});
            skCircle(sketch, "E5.4.8.0", {"center": v(-9.81, 9.65) * mm, "radius": 0.25 * mm});
            skCircle(sketch, "E5.4.9.0", {"center": v(-9.81, 10.65) * mm, "radius": 0.25 * mm});
            skCircle(sketch, "E5.4.10.0", {"center": v(-9.81, 11.65) * mm, "radius": 0.25 * mm});
            skCircle(sketch, "E5.4.11.0", {"center": v(-9.81, 12.65) * mm, "radius": 0.25 * mm});
            skCircle(sketch, "E5.4.12.0", {"center": v(-9.81, 13.65) * mm, "radius": 0.25 * mm});
            skCircle(sketch, "E5.4.13.0", {"center": v(-9.81, 14.65) * mm, "radius": 0.25 * mm});
            skCircle(sketch, "E5.4.14.0", {"center": v(-9.81, 15.65) * mm, "radius": 0.25 * mm});
            skCircle(sketch, "E5.4.15.0", {"center": v(-9.81, 16.65) * mm, "radius": 0.25 * mm});
            skCircle(sketch, "E5.4.16.0", {"center": v(-9.81, 17.65) * mm, "radius": 0.25 * mm});
            skCircle(sketch, "E5.4.17.0", {"center": v(-9.81, 18.65) * mm, "radius": 0.25 * mm});
            skCircle(sketch, "E5.4.18.0", {"center": v(-9.81, 19.65) * mm, "radius": 0.25 * mm});
            skCircle(sketch, "E5.4.19.0", {"center": v(-9.81, 20.65) * mm, "radius": 0.25 * mm});
            skCircle(sketch, "E5.4.20.0", {"center": v(-9.81, 21.65) * mm, "radius": 0.25 * mm});
            skCircle(sketch, "E5.4.21.0", {"center": v(-9.81, 22.65) * mm, "radius": 0.25 * mm});
            skCircle(sketch, "E5.4.22.0", {"center": v(-9.81, 23.65) * mm, "radius": 0.25 * mm});
            skCircle(sketch, "E5.4.23.0", {"center": v(-9.81, 24.65) * mm, "radius": 0.25 * mm});
            skCircle(sketch, "E5.4.24.0", {"center": v(-9.81, 25.65) * mm, "radius": 0.25 * mm});
            skCircle(sketch, "E5.4.25.0", {"center": v(-9.81, 26.65) * mm, "radius": 0.25 * mm});
            skCircle(sketch, "E5.4.26.0", {"center": v(-9.81, 27.65) * mm, "radius": 0.25 * mm});
            skCircle(sketch, "E5.4.27.0", {"center": v(-9.81, 28.65) * mm, "radius": 0.25 * mm});
            skCircle(sketch, "E5.4.28.0", {"center": v(-9.81, 29.65) * mm, "radius": 0.25 * mm});
            skCircle(sketch, "E5.5.0.0", {"center": v(-8.81, 1.65) * mm, "radius": 0.25 * mm});
            skCircle(sketch, "E5.5.1.0", {"center": v(-8.81, 2.65) * mm, "radius": 0.25 * mm});
            skCircle(sketch, "E5.5.2.0", {"center": v(-8.81, 3.65) * mm, "radius": 0.25 * mm});
            skCircle(sketch, "E5.5.3.0", {"center": v(-8.81, 4.65) * mm, "radius": 0.25 * mm});
            skCircle(sketch, "E5.5.4.0", {"center": v(-8.81, 5.65) * mm, "radius": 0.25 * mm});
            skCircle(sketch, "E5.5.5.0", {"center": v(-8.81, 6.65) * mm, "radius": 0.25 * mm});
            skCircle(sketch, "E5.5.6.0", {"center": v(-8.81, 7.65) * mm, "radius": 0.25 * mm});
            skCircle(sketch, "E5.5.7.0", {"center": v(-8.81, 8.65) * mm, "radius": 0.25 * mm});
            skCircle(sketch, "E5.5.8.0", {"center": v(-8.81, 9.65) * mm, "radius": 0.25 * mm});
            skCircle(sketch, "E5.5.9.0", {"center": v(-8.81, 10.65) * mm, "radius": 0.25 * mm});
            skCircle(sketch, "E5.5.10.0", {"center": v(-8.81, 11.65) * mm, "radius": 0.25 * mm});
            skCircle(sketch, "E5.5.11.0", {"center": v(-8.81, 12.65) * mm, "radius": 0.25 * mm});
            skCircle(sketch, "E5.5.12.0", {"center": v(-8.81, 13.65) * mm, "radius": 0.25 * mm});
            skCircle(sketch, "E5.5.13.0", {"center": v(-8.81, 14.65) * mm, "radius": 0.25 * mm});
            skCircle(sketch, "E5.5.14.0", {"center": v(-8.81, 15.65) * mm, "radius": 0.25 * mm});
            skCircle(sketch, "E5.5.15.0", {"center": v(-8.81, 16.65) * mm, "radius": 0.25 * mm});
            skCircle(sketch, "E5.5.16.0", {"center": v(-8.81, 17.65) * mm, "radius": 0.25 * mm});
            skCircle(sketch, "E5.5.17.0", {"center": v(-8.81, 18.65) * mm, "radius": 0.25 * mm});
            skCircle(sketch, "E5.5.18.0", {"center": v(-8.81, 19.65) * mm, "radius": 0.25 * mm});
            skCircle(sketch, "E5.5.19.0", {"center": v(-8.81, 20.65) * mm, "radius": 0.25 * mm});
            skCircle(sketch, "E5.5.20.0", {"center": v(-8.81, 21.65) * mm, "radius": 0.25 * mm});
            skCircle(sketch, "E5.5.21.0", {"center": v(-8.81, 22.65) * mm, "radius": 0.25 * mm});
            skCircle(sketch, "E5.5.22.0", {"center": v(-8.81, 23.65) * mm, "radius": 0.25 * mm});
            skCircle(sketch, "E5.5.23.0", {"center": v(-8.81, 24.65) * mm, "radius": 0.25 * mm});
            skCircle(sketch, "E5.5.24.0", {"center": v(-8.81, 25.65) * mm, "radius": 0.25 * mm});
            skCircle(sketch, "E5.5.25.0", {"center": v(-8.81, 26.65) * mm, "radius": 0.25 * mm});
            skCircle(sketch, "E5.5.26.0", {"center": v(-8.81, 27.65) * mm, "radius": 0.25 * mm});
            skCircle(sketch, "E5.5.27.0", {"center": v(-8.81, 28.65) * mm, "radius": 0.25 * mm});
            skCircle(sketch, "E5.5.28.0", {"center": v(-8.81, 29.65) * mm, "radius": 0.25 * mm});
            skCircle(sketch, "E5.6.0.0", {"center": v(-7.81, 1.65) * mm, "radius": 0.25 * mm});
            skCircle(sketch, "E5.6.1.0", {"center": v(-7.81, 2.65) * mm, "radius": 0.25 * mm});
            skCircle(sketch, "E5.6.2.0", {"center": v(-7.81, 3.65) * mm, "radius": 0.25 * mm});
            skCircle(sketch, "E5.6.3.0", {"center": v(-7.81, 4.65) * mm, "radius": 0.25 * mm});
            skCircle(sketch, "E5.6.4.0", {"center": v(-7.81, 5.65) * mm, "radius": 0.25 * mm});
            skCircle(sketch, "E5.6.5.0", {"center": v(-7.81, 6.65) * mm, "radius": 0.25 * mm});
            skCircle(sketch, "E5.6.6.0", {"center": v(-7.81, 7.65) * mm, "radius": 0.25 * mm});
            skCircle(sketch, "E5.6.7.0", {"center": v(-7.81, 8.65) * mm, "radius": 0.25 * mm});
            skCircle(sketch, "E5.6.8.0", {"center": v(-7.81, 9.65) * mm, "radius": 0.25 * mm});
            skCircle(sketch, "E5.6.9.0", {"center": v(-7.81, 10.65) * mm, "radius": 0.25 * mm});
            skCircle(sketch, "E5.6.10.0", {"center": v(-7.81, 11.65) * mm, "radius": 0.25 * mm});
            skCircle(sketch, "E5.6.11.0", {"center": v(-7.81, 12.65) * mm, "radius": 0.25 * mm});
            skCircle(sketch, "E5.6.12.0", {"center": v(-7.81, 13.65) * mm, "radius": 0.25 * mm});
            skCircle(sketch, "E5.6.13.0", {"center": v(-7.81, 14.65) * mm, "radius": 0.25 * mm});
            skCircle(sketch, "E5.6.14.0", {"center": v(-7.81, 15.65) * mm, "radius": 0.25 * mm});
            skCircle(sketch, "E5.6.15.0", {"center": v(-7.81, 16.65) * mm, "radius": 0.25 * mm});
            skCircle(sketch, "E5.6.16.0", {"center": v(-7.81, 17.65) * mm, "radius": 0.25 * mm});
            skCircle(sketch, "E5.6.17.0", {"center": v(-7.81, 18.65) * mm, "radius": 0.25 * mm});
            skCircle(sketch, "E5.6.18.0", {"center": v(-7.81, 19.65) * mm, "radius": 0.25 * mm});
            skCircle(sketch, "E5.6.19.0", {"center": v(-7.81, 20.65) * mm, "radius": 0.25 * mm});
            skCircle(sketch, "E5.6.20.0", {"center": v(-7.81, 21.65) * mm, "radius": 0.25 * mm});
            skCircle(sketch, "E5.6.21.0", {"center": v(-7.81, 22.65) * mm, "radius": 0.25 * mm});
            skCircle(sketch, "E5.6.22.0", {"center": v(-7.81, 23.65) * mm, "radius": 0.25 * mm});
            skCircle(sketch, "E5.6.23.0", {"center": v(-7.81, 24.65) * mm, "radius": 0.25 * mm});
            skCircle(sketch, "E5.6.24.0", {"center": v(-7.81, 25.65) * mm, "radius": 0.25 * mm});
            skCircle(sketch, "E5.6.25.0", {"center": v(-7.81, 26.65) * mm, "radius": 0.25 * mm});
            skCircle(sketch, "E5.6.26.0", {"center": v(-7.81, 27.65) * mm, "radius": 0.25 * mm});
            skCircle(sketch, "E5.6.27.0", {"center": v(-7.81, 28.65) * mm, "radius": 0.25 * mm});
            skCircle(sketch, "E5.6.28.0", {"center": v(-7.81, 29.65) * mm, "radius": 0.25 * mm});
            skCircle(sketch, "E5.7.0.0", {"center": v(-6.81, 1.65) * mm, "radius": 0.25 * mm});
            skCircle(sketch, "E5.7.1.0", {"center": v(-6.81, 2.65) * mm, "radius": 0.25 * mm});
            skCircle(sketch, "E5.7.2.0", {"center": v(-6.81, 3.65) * mm, "radius": 0.25 * mm});
            skCircle(sketch, "E5.7.3.0", {"center": v(-6.81, 4.65) * mm, "radius": 0.25 * mm});
            skCircle(sketch, "E5.7.4.0", {"center": v(-6.81, 5.65) * mm, "radius": 0.25 * mm});
            skCircle(sketch, "E5.7.5.0", {"center": v(-6.81, 6.65) * mm, "radius": 0.25 * mm});
            skCircle(sketch, "E5.7.6.0", {"center": v(-6.81, 7.65) * mm, "radius": 0.25 * mm});
            skCircle(sketch, "E5.7.7.0", {"center": v(-6.81, 8.65) * mm, "radius": 0.25 * mm});
            skCircle(sketch, "E5.7.8.0", {"center": v(-6.81, 9.65) * mm, "radius": 0.25 * mm});
            skCircle(sketch, "E5.7.9.0", {"center": v(-6.81, 10.65) * mm, "radius": 0.25 * mm});
            skCircle(sketch, "E5.7.10.0", {"center": v(-6.81, 11.65) * mm, "radius": 0.25 * mm});
            skCircle(sketch, "E5.7.11.0", {"center": v(-6.81, 12.65) * mm, "radius": 0.25 * mm});
            skCircle(sketch, "E5.7.12.0", {"center": v(-6.81, 13.65) * mm, "radius": 0.25 * mm});
            skCircle(sketch, "E5.7.13.0", {"center": v(-6.81, 14.65) * mm, "radius": 0.25 * mm});
            skCircle(sketch, "E5.7.14.0", {"center": v(-6.81, 15.65) * mm, "radius": 0.25 * mm});
            skCircle(sketch, "E5.7.15.0", {"center": v(-6.81, 16.65) * mm, "radius": 0.25 * mm});
            skCircle(sketch, "E5.7.16.0", {"center": v(-6.81, 17.65) * mm, "radius": 0.25 * mm});
            skCircle(sketch, "E5.7.17.0", {"center": v(-6.81, 18.65) * mm, "radius": 0.25 * mm});
            skCircle(sketch, "E5.7.18.0", {"center": v(-6.81, 19.65) * mm, "radius": 0.25 * mm});
            skCircle(sketch, "E5.7.19.0", {"center": v(-6.81, 20.65) * mm, "radius": 0.25 * mm});
            skCircle(sketch, "E5.7.20.0", {"center": v(-6.81, 21.65) * mm, "radius": 0.25 * mm});
            skCircle(sketch, "E5.7.21.0", {"center": v(-6.81, 22.65) * mm, "radius": 0.25 * mm});
            skCircle(sketch, "E5.7.22.0", {"center": v(-6.81, 23.65) * mm, "radius": 0.25 * mm});
            skCircle(sketch, "E5.7.23.0", {"center": v(-6.81, 24.65) * mm, "radius": 0.25 * mm});
            skCircle(sketch, "E5.7.24.0", {"center": v(-6.81, 25.65) * mm, "radius": 0.25 * mm});
            skCircle(sketch, "E5.7.25.0", {"center": v(-6.81, 26.65) * mm, "radius": 0.25 * mm});
            skCircle(sketch, "E5.7.26.0", {"center": v(-6.81, 27.65) * mm, "radius": 0.25 * mm});
            skCircle(sketch, "E5.7.27.0", {"center": v(-6.81, 28.65) * mm, "radius": 0.25 * mm});
            skCircle(sketch, "E5.7.28.0", {"center": v(-6.81, 29.65) * mm, "radius": 0.25 * mm});
            skCircle(sketch, "E5.8.0.0", {"center": v(-5.81, 1.65) * mm, "radius": 0.25 * mm});
            skCircle(sketch, "E5.8.1.0", {"center": v(-5.81, 2.65) * mm, "radius": 0.25 * mm});
            skCircle(sketch, "E5.8.2.0", {"center": v(-5.81, 3.65) * mm, "radius": 0.25 * mm});
            skCircle(sketch, "E5.8.3.0", {"center": v(-5.81, 4.65) * mm, "radius": 0.25 * mm});
            skCircle(sketch, "E5.8.4.0", {"center": v(-5.81, 5.65) * mm, "radius": 0.25 * mm});
            skCircle(sketch, "E5.8.5.0", {"center": v(-5.81, 6.65) * mm, "radius": 0.25 * mm});
            skCircle(sketch, "E5.8.6.0", {"center": v(-5.81, 7.65) * mm, "radius": 0.25 * mm});
            skCircle(sketch, "E5.8.7.0", {"center": v(-5.81, 8.65) * mm, "radius": 0.25 * mm});
            skCircle(sketch, "E5.8.8.0", {"center": v(-5.81, 9.65) * mm, "radius": 0.25 * mm});
            skCircle(sketch, "E5.8.9.0", {"center": v(-5.81, 10.65) * mm, "radius": 0.25 * mm});
            skCircle(sketch, "E5.8.10.0", {"center": v(-5.81, 11.65) * mm, "radius": 0.25 * mm});
            skCircle(sketch, "E5.8.11.0", {"center": v(-5.81, 12.65) * mm, "radius": 0.25 * mm});
            skCircle(sketch, "E5.8.12.0", {"center": v(-5.81, 13.65) * mm, "radius": 0.25 * mm});
            skCircle(sketch, "E5.8.13.0", {"center": v(-5.81, 14.65) * mm, "radius": 0.25 * mm});
            skCircle(sketch, "E5.8.14.0", {"center": v(-5.81, 15.65) * mm, "radius": 0.25 * mm});
            skCircle(sketch, "E5.8.15.0", {"center": v(-5.81, 16.65) * mm, "radius": 0.25 * mm});
            skCircle(sketch, "E5.8.16.0", {"center": v(-5.81, 17.65) * mm, "radius": 0.25 * mm});
            skCircle(sketch, "E5.8.17.0", {"center": v(-5.81, 18.65) * mm, "radius": 0.25 * mm});
            skCircle(sketch, "E5.8.18.0", {"center": v(-5.81, 19.65) * mm, "radius": 0.25 * mm});
            skCircle(sketch, "E5.8.19.0", {"center": v(-5.81, 20.65) * mm, "radius": 0.25 * mm});
            skCircle(sketch, "E5.8.20.0", {"center": v(-5.81, 21.65) * mm, "radius": 0.25 * mm});
            skCircle(sketch, "E5.8.21.0", {"center": v(-5.81, 22.65) * mm, "radius": 0.25 * mm});
            skCircle(sketch, "E5.8.22.0", {"center": v(-5.81, 23.65) * mm, "radius": 0.25 * mm});
            skCircle(sketch, "E5.8.23.0", {"center": v(-5.81, 24.65) * mm, "radius": 0.25 * mm});
            skCircle(sketch, "E5.8.24.0", {"center": v(-5.81, 25.65) * mm, "radius": 0.25 * mm});
            skCircle(sketch, "E5.8.25.0", {"center": v(-5.81, 26.65) * mm, "radius": 0.25 * mm});
            skCircle(sketch, "E5.8.26.0", {"center": v(-5.81, 27.65) * mm, "radius": 0.25 * mm});
            skCircle(sketch, "E5.8.27.0", {"center": v(-5.81, 28.65) * mm, "radius": 0.25 * mm});
            skCircle(sketch, "E5.8.28.0", {"center": v(-5.81, 29.65) * mm, "radius": 0.25 * mm});
            skCircle(sketch, "E5.9.0.0", {"center": v(-4.81, 1.65) * mm, "radius": 0.25 * mm});
            skCircle(sketch, "E5.9.1.0", {"center": v(-4.81, 2.65) * mm, "radius": 0.25 * mm});
            skCircle(sketch, "E5.9.2.0", {"center": v(-4.81, 3.65) * mm, "radius": 0.25 * mm});
            skCircle(sketch, "E5.9.3.0", {"center": v(-4.81, 4.65) * mm, "radius": 0.25 * mm});
            skCircle(sketch, "E5.9.4.0", {"center": v(-4.81, 5.65) * mm, "radius": 0.25 * mm});
            skCircle(sketch, "E5.9.5.0", {"center": v(-4.81, 6.65) * mm, "radius": 0.25 * mm});
            skCircle(sketch, "E5.9.6.0", {"center": v(-4.81, 7.65) * mm, "radius": 0.25 * mm});
            skCircle(sketch, "E5.9.7.0", {"center": v(-4.81, 8.65) * mm, "radius": 0.25 * mm});
            skCircle(sketch, "E5.9.8.0", {"center": v(-4.81, 9.65) * mm, "radius": 0.25 * mm});
            skCircle(sketch, "E5.9.9.0", {"center": v(-4.81, 10.65) * mm, "radius": 0.25 * mm});
            skCircle(sketch, "E5.9.10.0", {"center": v(-4.81, 11.65) * mm, "radius": 0.25 * mm});
            skCircle(sketch, "E5.9.11.0", {"center": v(-4.81, 12.65) * mm, "radius": 0.25 * mm});
            skCircle(sketch, "E5.9.12.0", {"center": v(-4.81, 13.65) * mm, "radius": 0.25 * mm});
            skCircle(sketch, "E5.9.13.0", {"center": v(-4.81, 14.65) * mm, "radius": 0.25 * mm});
            skCircle(sketch, "E5.9.14.0", {"center": v(-4.81, 15.65) * mm, "radius": 0.25 * mm});
            skCircle(sketch, "E5.9.15.0", {"center": v(-4.81, 16.65) * mm, "radius": 0.25 * mm});
            skCircle(sketch, "E5.9.16.0", {"center": v(-4.81, 17.65) * mm, "radius": 0.25 * mm});
            skCircle(sketch, "E5.9.17.0", {"center": v(-4.81, 18.65) * mm, "radius": 0.25 * mm});
            skCircle(sketch, "E5.9.18.0", {"center": v(-4.81, 19.65) * mm, "radius": 0.25 * mm});
            skCircle(sketch, "E5.9.19.0", {"center": v(-4.81, 20.65) * mm, "radius": 0.25 * mm});
            skCircle(sketch, "E5.9.20.0", {"center": v(-4.81, 21.65) * mm, "radius": 0.25 * mm});
            skCircle(sketch, "E5.9.21.0", {"center": v(-4.81, 22.65) * mm, "radius": 0.25 * mm});
            skCircle(sketch, "E5.9.22.0", {"center": v(-4.81, 23.65) * mm, "radius": 0.25 * mm});
            skCircle(sketch, "E5.9.23.0", {"center": v(-4.81, 24.65) * mm, "radius": 0.25 * mm});
            skCircle(sketch, "E5.9.24.0", {"center": v(-4.81, 25.65) * mm, "radius": 0.25 * mm});
            skCircle(sketch, "E5.9.25.0", {"center": v(-4.81, 26.65) * mm, "radius": 0.25 * mm});
            skCircle(sketch, "E5.9.26.0", {"center": v(-4.81, 27.65) * mm, "radius": 0.25 * mm});
            skCircle(sketch, "E5.9.27.0", {"center": v(-4.81, 28.65) * mm, "radius": 0.25 * mm});
            skCircle(sketch, "E5.9.28.0", {"center": v(-4.81, 29.65) * mm, "radius": 0.25 * mm});
            skCircle(sketch, "E5.10.0.0", {"center": v(-3.81, 1.65) * mm, "radius": 0.25 * mm});
            skCircle(sketch, "E5.10.1.0", {"center": v(-3.81, 2.65) * mm, "radius": 0.25 * mm});
            skCircle(sketch, "E5.10.2.0", {"center": v(-3.81, 3.65) * mm, "radius": 0.25 * mm});
            skCircle(sketch, "E5.10.3.0", {"center": v(-3.81, 4.65) * mm, "radius": 0.25 * mm});
            skCircle(sketch, "E5.10.4.0", {"center": v(-3.81, 5.65) * mm, "radius": 0.25 * mm});
            skCircle(sketch, "E5.10.5.0", {"center": v(-3.81, 6.65) * mm, "radius": 0.25 * mm});
            skCircle(sketch, "E5.10.6.0", {"center": v(-3.81, 7.65) * mm, "radius": 0.25 * mm});
            skCircle(sketch, "E5.10.7.0", {"center": v(-3.81, 8.65) * mm, "radius": 0.25 * mm});
            skCircle(sketch, "E5.10.8.0", {"center": v(-3.81, 9.65) * mm, "radius": 0.25 * mm});
            skCircle(sketch, "E5.10.9.0", {"center": v(-3.81, 10.65) * mm, "radius": 0.25 * mm});
            skCircle(sketch, "E5.10.10.0", {"center": v(-3.81, 11.65) * mm, "radius": 0.25 * mm});
            skCircle(sketch, "E5.10.11.0", {"center": v(-3.81, 12.65) * mm, "radius": 0.25 * mm});
            skCircle(sketch, "E5.10.12.0", {"center": v(-3.81, 13.65) * mm, "radius": 0.25 * mm});
            skCircle(sketch, "E5.10.13.0", {"center": v(-3.81, 14.65) * mm, "radius": 0.25 * mm});
            skCircle(sketch, "E5.10.14.0", {"center": v(-3.81, 15.65) * mm, "radius": 0.25 * mm});
            skCircle(sketch, "E5.10.15.0", {"center": v(-3.81, 16.65) * mm, "radius": 0.25 * mm});
            skCircle(sketch, "E5.10.16.0", {"center": v(-3.81, 17.65) * mm, "radius": 0.25 * mm});
            skCircle(sketch, "E5.10.17.0", {"center": v(-3.81, 18.65) * mm, "radius": 0.25 * mm});
            skCircle(sketch, "E5.10.18.0", {"center": v(-3.81, 19.65) * mm, "radius": 0.25 * mm});
            skCircle(sketch, "E5.10.19.0", {"center": v(-3.81, 20.65) * mm, "radius": 0.25 * mm});
            skCircle(sketch, "E5.10.20.0", {"center": v(-3.81, 21.65) * mm, "radius": 0.25 * mm});
            skCircle(sketch, "E5.10.21.0", {"center": v(-3.81, 22.65) * mm, "radius": 0.25 * mm});
            skCircle(sketch, "E5.10.22.0", {"center": v(-3.81, 23.65) * mm, "radius": 0.25 * mm});
            skCircle(sketch, "E5.10.23.0", {"center": v(-3.81, 24.65) * mm, "radius": 0.25 * mm});
            skCircle(sketch, "E5.10.24.0", {"center": v(-3.81, 25.65) * mm, "radius": 0.25 * mm});
            skCircle(sketch, "E5.10.25.0", {"center": v(-3.81, 26.65) * mm, "radius": 0.25 * mm});
            skCircle(sketch, "E5.10.26.0", {"center": v(-3.81, 27.65) * mm, "radius": 0.25 * mm});
            skCircle(sketch, "E5.10.27.0", {"center": v(-3.81, 28.65) * mm, "radius": 0.25 * mm});
            skCircle(sketch, "E5.10.28.0", {"center": v(-3.81, 29.65) * mm, "radius": 0.25 * mm});
            skCircle(sketch, "E5.11.0.0", {"center": v(-2.81, 1.65) * mm, "radius": 0.25 * mm});
            skCircle(sketch, "E5.11.1.0", {"center": v(-2.81, 2.65) * mm, "radius": 0.25 * mm});
            skCircle(sketch, "E5.11.2.0", {"center": v(-2.81, 3.65) * mm, "radius": 0.25 * mm});
            skCircle(sketch, "E5.11.3.0", {"center": v(-2.81, 4.65) * mm, "radius": 0.25 * mm});
            skCircle(sketch, "E5.11.4.0", {"center": v(-2.81, 5.65) * mm, "radius": 0.25 * mm});
            skCircle(sketch, "E5.11.5.0", {"center": v(-2.81, 6.65) * mm, "radius": 0.25 * mm});
            skCircle(sketch, "E5.11.6.0", {"center": v(-2.81, 7.65) * mm, "radius": 0.25 * mm});
            skCircle(sketch, "E5.11.7.0", {"center": v(-2.81, 8.65) * mm, "radius": 0.25 * mm});
            skCircle(sketch, "E5.11.8.0", {"center": v(-2.81, 9.65) * mm, "radius": 0.25 * mm});
            skCircle(sketch, "E5.11.9.0", {"center": v(-2.81, 10.65) * mm, "radius": 0.25 * mm});
            skCircle(sketch, "E5.11.10.0", {"center": v(-2.81, 11.65) * mm, "radius": 0.25 * mm});
            skCircle(sketch, "E5.11.11.0", {"center": v(-2.81, 12.65) * mm, "radius": 0.25 * mm});
            skCircle(sketch, "E5.11.12.0", {"center": v(-2.81, 13.65) * mm, "radius": 0.25 * mm});
            skCircle(sketch, "E5.11.13.0", {"center": v(-2.81, 14.65) * mm, "radius": 0.25 * mm});
            skCircle(sketch, "E5.11.14.0", {"center": v(-2.81, 15.65) * mm, "radius": 0.25 * mm});
            skCircle(sketch, "E5.11.15.0", {"center": v(-2.81, 16.65) * mm, "radius": 0.25 * mm});
            skCircle(sketch, "E5.11.16.0", {"center": v(-2.81, 17.65) * mm, "radius": 0.25 * mm});
            skCircle(sketch, "E5.11.17.0", {"center": v(-2.81, 18.65) * mm, "radius": 0.25 * mm});
            skCircle(sketch, "E5.11.18.0", {"center": v(-2.81, 19.65) * mm, "radius": 0.25 * mm});
            skCircle(sketch, "E5.11.19.0", {"center": v(-2.81, 20.65) * mm, "radius": 0.25 * mm});
            skCircle(sketch, "E5.11.20.0", {"center": v(-2.81, 21.65) * mm, "radius": 0.25 * mm});
            skCircle(sketch, "E5.11.21.0", {"center": v(-2.81, 22.65) * mm, "radius": 0.25 * mm});
            skCircle(sketch, "E5.11.22.0", {"center": v(-2.81, 23.65) * mm, "radius": 0.25 * mm});
            skCircle(sketch, "E5.11.23.0", {"center": v(-2.81, 24.65) * mm, "radius": 0.25 * mm});
            skCircle(sketch, "E5.11.24.0", {"center": v(-2.81, 25.65) * mm, "radius": 0.25 * mm});
            skCircle(sketch, "E5.11.25.0", {"center": v(-2.81, 26.65) * mm, "radius": 0.25 * mm});
            skCircle(sketch, "E5.11.26.0", {"center": v(-2.81, 27.65) * mm, "radius": 0.25 * mm});
            skCircle(sketch, "E5.11.27.0", {"center": v(-2.81, 28.65) * mm, "radius": 0.25 * mm});
            skCircle(sketch, "E5.11.28.0", {"center": v(-2.81, 29.65) * mm, "radius": 0.25 * mm});
            skCircle(sketch, "E5.12.0.0", {"center": v(-1.81, 1.65) * mm, "radius": 0.25 * mm});
            skCircle(sketch, "E5.12.1.0", {"center": v(-1.81, 2.65) * mm, "radius": 0.25 * mm});
            skCircle(sketch, "E5.12.2.0", {"center": v(-1.81, 3.65) * mm, "radius": 0.25 * mm});
            skCircle(sketch, "E5.12.3.0", {"center": v(-1.81, 4.65) * mm, "radius": 0.25 * mm});
            skCircle(sketch, "E5.12.4.0", {"center": v(-1.81, 5.65) * mm, "radius": 0.25 * mm});
            skCircle(sketch, "E5.12.5.0", {"center": v(-1.81, 6.65) * mm, "radius": 0.25 * mm});
            skCircle(sketch, "E5.12.6.0", {"center": v(-1.81, 7.65) * mm, "radius": 0.25 * mm});
            skCircle(sketch, "E5.12.7.0", {"center": v(-1.81, 8.65) * mm, "radius": 0.25 * mm});
            skCircle(sketch, "E5.12.8.0", {"center": v(-1.81, 9.65) * mm, "radius": 0.25 * mm});
            skCircle(sketch, "E5.12.9.0", {"center": v(-1.81, 10.65) * mm, "radius": 0.25 * mm});
            skCircle(sketch, "E5.12.10.0", {"center": v(-1.81, 11.65) * mm, "radius": 0.25 * mm});
            skCircle(sketch, "E5.12.11.0", {"center": v(-1.81, 12.65) * mm, "radius": 0.25 * mm});
            skCircle(sketch, "E5.12.12.0", {"center": v(-1.81, 13.65) * mm, "radius": 0.25 * mm});
            skCircle(sketch, "E5.12.13.0", {"center": v(-1.81, 14.65) * mm, "radius": 0.25 * mm});
            skCircle(sketch, "E5.12.14.0", {"center": v(-1.81, 15.65) * mm, "radius": 0.25 * mm});
            skCircle(sketch, "E5.12.15.0", {"center": v(-1.81, 16.65) * mm, "radius": 0.25 * mm});
            skCircle(sketch, "E5.12.16.0", {"center": v(-1.81, 17.65) * mm, "radius": 0.25 * mm});
            skCircle(sketch, "E5.12.17.0", {"center": v(-1.81, 18.65) * mm, "radius": 0.25 * mm});
            skCircle(sketch, "E5.12.18.0", {"center": v(-1.81, 19.65) * mm, "radius": 0.25 * mm});
            skCircle(sketch, "E5.12.19.0", {"center": v(-1.81, 20.65) * mm, "radius": 0.25 * mm});
            skCircle(sketch, "E5.12.20.0", {"center": v(-1.81, 21.65) * mm, "radius": 0.25 * mm});
            skCircle(sketch, "E5.12.21.0", {"center": v(-1.81, 22.65) * mm, "radius": 0.25 * mm});
            skCircle(sketch, "E5.12.22.0", {"center": v(-1.81, 23.65) * mm, "radius": 0.25 * mm});
            skCircle(sketch, "E5.12.23.0", {"center": v(-1.81, 24.65) * mm, "radius": 0.25 * mm});
            skCircle(sketch, "E5.12.24.0", {"center": v(-1.81, 25.65) * mm, "radius": 0.25 * mm});
            skCircle(sketch, "E5.12.25.0", {"center": v(-1.81, 26.65) * mm, "radius": 0.25 * mm});
            skCircle(sketch, "E5.12.26.0", {"center": v(-1.81, 27.65) * mm, "radius": 0.25 * mm});
            skCircle(sketch, "E5.12.27.0", {"center": v(-1.81, 28.65) * mm, "radius": 0.25 * mm});
            skCircle(sketch, "E5.12.28.0", {"center": v(-1.81, 29.65) * mm, "radius": 0.25 * mm});
            skCircle(sketch, "E5.13.0.0", {"center": v(-0.81, 1.65) * mm, "radius": 0.25 * mm});
            skCircle(sketch, "E5.13.1.0", {"center": v(-0.81, 2.65) * mm, "radius": 0.25 * mm});
            skCircle(sketch, "E5.13.2.0", {"center": v(-0.81, 3.65) * mm, "radius": 0.25 * mm});
            skCircle(sketch, "E5.13.3.0", {"center": v(-0.81, 4.65) * mm, "radius": 0.25 * mm});
            skCircle(sketch, "E5.13.4.0", {"center": v(-0.81, 5.65) * mm, "radius": 0.25 * mm});
            skCircle(sketch, "E5.13.5.0", {"center": v(-0.81, 6.65) * mm, "radius": 0.25 * mm});
            skCircle(sketch, "E5.13.6.0", {"center": v(-0.81, 7.65) * mm, "radius": 0.25 * mm});
            skCircle(sketch, "E5.13.7.0", {"center": v(-0.81, 8.65) * mm, "radius": 0.25 * mm});
            skCircle(sketch, "E5.13.8.0", {"center": v(-0.81, 9.65) * mm, "radius": 0.25 * mm});
            skCircle(sketch, "E5.13.9.0", {"center": v(-0.81, 10.65) * mm, "radius": 0.25 * mm});
            skCircle(sketch, "E5.13.10.0", {"center": v(-0.81, 11.65) * mm, "radius": 0.25 * mm});
            skCircle(sketch, "E5.13.11.0", {"center": v(-0.81, 12.65) * mm, "radius": 0.25 * mm});
            skCircle(sketch, "E5.13.12.0", {"center": v(-0.81, 13.65) * mm, "radius": 0.25 * mm});
            skCircle(sketch, "E5.13.13.0", {"center": v(-0.81, 14.65) * mm, "radius": 0.25 * mm});
            skCircle(sketch, "E5.13.14.0", {"center": v(-0.81, 15.65) * mm, "radius": 0.25 * mm});
            skCircle(sketch, "E5.13.15.0", {"center": v(-0.81, 16.65) * mm, "radius": 0.25 * mm});
            skCircle(sketch, "E5.13.16.0", {"center": v(-0.81, 17.65) * mm, "radius": 0.25 * mm});
            skCircle(sketch, "E5.13.17.0", {"center": v(-0.81, 18.65) * mm, "radius": 0.25 * mm});
            skCircle(sketch, "E5.13.18.0", {"center": v(-0.81, 19.65) * mm, "radius": 0.25 * mm});
            skCircle(sketch, "E5.13.19.0", {"center": v(-0.81, 20.65) * mm, "radius": 0.25 * mm});
            skCircle(sketch, "E5.13.20.0", {"center": v(-0.81, 21.65) * mm, "radius": 0.25 * mm});
            skCircle(sketch, "E5.13.21.0", {"center": v(-0.81, 22.65) * mm, "radius": 0.25 * mm});
            skCircle(sketch, "E5.13.22.0", {"center": v(-0.81, 23.65) * mm, "radius": 0.25 * mm});
            skCircle(sketch, "E5.13.23.0", {"center": v(-0.81, 24.65) * mm, "radius": 0.25 * mm});
            skCircle(sketch, "E5.13.24.0", {"center": v(-0.81, 25.65) * mm, "radius": 0.25 * mm});
            skCircle(sketch, "E5.13.25.0", {"center": v(-0.81, 26.65) * mm, "radius": 0.25 * mm});
            skCircle(sketch, "E5.13.26.0", {"center": v(-0.81, 27.65) * mm, "radius": 0.25 * mm});
            skCircle(sketch, "E5.13.27.0", {"center": v(-0.81, 28.65) * mm, "radius": 0.25 * mm});
            skCircle(sketch, "E5.13.28.0", {"center": v(-0.81, 29.65) * mm, "radius": 0.25 * mm});
            skCircle(sketch, "E5.14.0.0", {"center": v(0.19, 1.65) * mm, "radius": 0.25 * mm});
            skCircle(sketch, "E5.14.1.0", {"center": v(0.19, 2.65) * mm, "radius": 0.25 * mm});
            skCircle(sketch, "E5.14.2.0", {"center": v(0.19, 3.65) * mm, "radius": 0.25 * mm});
            skCircle(sketch, "E5.14.3.0", {"center": v(0.19, 4.65) * mm, "radius": 0.25 * mm});
            skCircle(sketch, "E5.14.4.0", {"center": v(0.19, 5.65) * mm, "radius": 0.25 * mm});
            skCircle(sketch, "E5.14.5.0", {"center": v(0.19, 6.65) * mm, "radius": 0.25 * mm});
            skCircle(sketch, "E5.14.6.0", {"center": v(0.19, 7.65) * mm, "radius": 0.25 * mm});
            skCircle(sketch, "E5.14.7.0", {"center": v(0.19, 8.65) * mm, "radius": 0.25 * mm});
            skCircle(sketch, "E5.14.8.0", {"center": v(0.19, 9.65) * mm, "radius": 0.25 * mm});
            skCircle(sketch, "E5.14.9.0", {"center": v(0.19, 10.65) * mm, "radius": 0.25 * mm});
            skCircle(sketch, "E5.14.10.0", {"center": v(0.19, 11.65) * mm, "radius": 0.25 * mm});
            skCircle(sketch, "E5.14.11.0", {"center": v(0.19, 12.65) * mm, "radius": 0.25 * mm});
            skCircle(sketch, "E5.14.12.0", {"center": v(0.19, 13.65) * mm, "radius": 0.25 * mm});
            skCircle(sketch, "E5.14.13.0", {"center": v(0.19, 14.65) * mm, "radius": 0.25 * mm});
            skCircle(sketch, "E5.14.14.0", {"center": v(0.19, 15.65) * mm, "radius": 0.25 * mm});
            skCircle(sketch, "E5.14.15.0", {"center": v(0.19, 16.65) * mm, "radius": 0.25 * mm});
            skCircle(sketch, "E5.14.16.0", {"center": v(0.19, 17.65) * mm, "radius": 0.25 * mm});
            skCircle(sketch, "E5.14.17.0", {"center": v(0.19, 18.65) * mm, "radius": 0.25 * mm});
            skCircle(sketch, "E5.14.18.0", {"center": v(0.19, 19.65) * mm, "radius": 0.25 * mm});
            skCircle(sketch, "E5.14.19.0", {"center": v(0.19, 20.65) * mm, "radius": 0.25 * mm});
            skCircle(sketch, "E5.14.20.0", {"center": v(0.19, 21.65) * mm, "radius": 0.25 * mm});
            skCircle(sketch, "E5.14.21.0", {"center": v(0.19, 22.65) * mm, "radius": 0.25 * mm});
            skCircle(sketch, "E5.14.22.0", {"center": v(0.19, 23.65) * mm, "radius": 0.25 * mm});
            skCircle(sketch, "E5.14.23.0", {"center": v(0.19, 24.65) * mm, "radius": 0.25 * mm});
            skCircle(sketch, "E5.14.24.0", {"center": v(0.19, 25.65) * mm, "radius": 0.25 * mm});
            skCircle(sketch, "E5.14.25.0", {"center": v(0.19, 26.65) * mm, "radius": 0.25 * mm});
            skCircle(sketch, "E5.14.26.0", {"center": v(0.19, 27.65) * mm, "radius": 0.25 * mm});
            skCircle(sketch, "E5.14.27.0", {"center": v(0.19, 28.65) * mm, "radius": 0.25 * mm});
            skCircle(sketch, "E5.14.28.0", {"center": v(0.19, 29.65) * mm, "radius": 0.25 * mm});
            skCircle(sketch, "E5.15.0.0", {"center": v(1.19, 1.65) * mm, "radius": 0.25 * mm});
            skCircle(sketch, "E5.15.1.0", {"center": v(1.19, 2.65) * mm, "radius": 0.25 * mm});
            skCircle(sketch, "E5.15.2.0", {"center": v(1.19, 3.65) * mm, "radius": 0.25 * mm});
            skCircle(sketch, "E5.15.3.0", {"center": v(1.19, 4.65) * mm, "radius": 0.25 * mm});
            skCircle(sketch, "E5.15.4.0", {"center": v(1.19, 5.65) * mm, "radius": 0.25 * mm});
            skCircle(sketch, "E5.15.5.0", {"center": v(1.19, 6.65) * mm, "radius": 0.25 * mm});
            skCircle(sketch, "E5.15.6.0", {"center": v(1.19, 7.65) * mm, "radius": 0.25 * mm});
            skCircle(sketch, "E5.15.7.0", {"center": v(1.19, 8.65) * mm, "radius": 0.25 * mm});
            skCircle(sketch, "E5.15.8.0", {"center": v(1.19, 9.65) * mm, "radius": 0.25 * mm});
            skCircle(sketch, "E5.15.9.0", {"center": v(1.19, 10.65) * mm, "radius": 0.25 * mm});
            skCircle(sketch, "E5.15.10.0", {"center": v(1.19, 11.65) * mm, "radius": 0.25 * mm});
            skCircle(sketch, "E5.15.11.0", {"center": v(1.19, 12.65) * mm, "radius": 0.25 * mm});
            skCircle(sketch, "E5.15.12.0", {"center": v(1.19, 13.65) * mm, "radius": 0.25 * mm});
            skCircle(sketch, "E5.15.13.0", {"center": v(1.19, 14.65) * mm, "radius": 0.25 * mm});
            skCircle(sketch, "E5.15.14.0", {"center": v(1.19, 15.65) * mm, "radius": 0.25 * mm});
            skCircle(sketch, "E5.15.15.0", {"center": v(1.19, 16.65) * mm, "radius": 0.25 * mm});
            skCircle(sketch, "E5.15.16.0", {"center": v(1.19, 17.65) * mm, "radius": 0.25 * mm});
            skCircle(sketch, "E5.15.17.0", {"center": v(1.19, 18.65) * mm, "radius": 0.25 * mm});
            skCircle(sketch, "E5.15.18.0", {"center": v(1.19, 19.65) * mm, "radius": 0.25 * mm});
            skCircle(sketch, "E5.15.19.0", {"center": v(1.19, 20.65) * mm, "radius": 0.25 * mm});
            skCircle(sketch, "E5.15.20.0", {"center": v(1.19, 21.65) * mm, "radius": 0.25 * mm});
            skCircle(sketch, "E5.15.21.0", {"center": v(1.19, 22.65) * mm, "radius": 0.25 * mm});
            skCircle(sketch, "E5.15.22.0", {"center": v(1.19, 23.65) * mm, "radius": 0.25 * mm});
            skCircle(sketch, "E5.15.23.0", {"center": v(1.19, 24.65) * mm, "radius": 0.25 * mm});
            skCircle(sketch, "E5.15.24.0", {"center": v(1.19, 25.65) * mm, "radius": 0.25 * mm});
            skCircle(sketch, "E5.15.25.0", {"center": v(1.19, 26.65) * mm, "radius": 0.25 * mm});
            skCircle(sketch, "E5.15.26.0", {"center": v(1.19, 27.65) * mm, "radius": 0.25 * mm});
            skCircle(sketch, "E5.15.27.0", {"center": v(1.19, 28.65) * mm, "radius": 0.25 * mm});
            skCircle(sketch, "E5.15.28.0", {"center": v(1.19, 29.65) * mm, "radius": 0.25 * mm});
            skCircle(sketch, "E5.16.0.0", {"center": v(2.19, 1.65) * mm, "radius": 0.25 * mm});
            skCircle(sketch, "E5.16.1.0", {"center": v(2.19, 2.65) * mm, "radius": 0.25 * mm});
            skCircle(sketch, "E5.16.2.0", {"center": v(2.19, 3.65) * mm, "radius": 0.25 * mm});
            skCircle(sketch, "E5.16.3.0", {"center": v(2.19, 4.65) * mm, "radius": 0.25 * mm});
            skCircle(sketch, "E5.16.4.0", {"center": v(2.19, 5.65) * mm, "radius": 0.25 * mm});
            skCircle(sketch, "E5.16.5.0", {"center": v(2.19, 6.65) * mm, "radius": 0.25 * mm});
            skCircle(sketch, "E5.16.6.0", {"center": v(2.19, 7.65) * mm, "radius": 0.25 * mm});
            skCircle(sketch, "E5.16.7.0", {"center": v(2.19, 8.65) * mm, "radius": 0.25 * mm});
            skCircle(sketch, "E5.16.8.0", {"center": v(2.19, 9.65) * mm, "radius": 0.25 * mm});
            skCircle(sketch, "E5.16.9.0", {"center": v(2.19, 10.65) * mm, "radius": 0.25 * mm});
            skCircle(sketch, "E5.16.10.0", {"center": v(2.19, 11.65) * mm, "radius": 0.25 * mm});
            skCircle(sketch, "E5.16.11.0", {"center": v(2.19, 12.65) * mm, "radius": 0.25 * mm});
            skCircle(sketch, "E5.16.12.0", {"center": v(2.19, 13.65) * mm, "radius": 0.25 * mm});
            skCircle(sketch, "E5.16.13.0", {"center": v(2.19, 14.65) * mm, "radius": 0.25 * mm});
            skCircle(sketch, "E5.16.14.0", {"center": v(2.19, 15.65) * mm, "radius": 0.25 * mm});
            skCircle(sketch, "E5.16.15.0", {"center": v(2.19, 16.65) * mm, "radius": 0.25 * mm});
            skCircle(sketch, "E5.16.16.0", {"center": v(2.19, 17.65) * mm, "radius": 0.25 * mm});
            skCircle(sketch, "E5.16.17.0", {"center": v(2.19, 18.65) * mm, "radius": 0.25 * mm});
            skCircle(sketch, "E5.16.18.0", {"center": v(2.19, 19.65) * mm, "radius": 0.25 * mm});
            skCircle(sketch, "E5.16.19.0", {"center": v(2.19, 20.65) * mm, "radius": 0.25 * mm});
            skCircle(sketch, "E5.16.20.0", {"center": v(2.19, 21.65) * mm, "radius": 0.25 * mm});
            skCircle(sketch, "E5.16.21.0", {"center": v(2.19, 22.65) * mm, "radius": 0.25 * mm});
            skCircle(sketch, "E5.16.22.0", {"center": v(2.19, 23.65) * mm, "radius": 0.25 * mm});
            skCircle(sketch, "E5.16.23.0", {"center": v(2.19, 24.65) * mm, "radius": 0.25 * mm});
            skCircle(sketch, "E5.16.24.0", {"center": v(2.19, 25.65) * mm, "radius": 0.25 * mm});
            skCircle(sketch, "E5.16.25.0", {"center": v(2.19, 26.65) * mm, "radius": 0.25 * mm});
            skCircle(sketch, "E5.16.26.0", {"center": v(2.19, 27.65) * mm, "radius": 0.25 * mm});
            skCircle(sketch, "E5.16.27.0", {"center": v(2.19, 28.65) * mm, "radius": 0.25 * mm});
            skCircle(sketch, "E5.16.28.0", {"center": v(2.19, 29.65) * mm, "radius": 0.25 * mm});
            skCircle(sketch, "E5.17.0.0", {"center": v(3.19, 1.65) * mm, "radius": 0.25 * mm});
            skCircle(sketch, "E5.17.1.0", {"center": v(3.19, 2.65) * mm, "radius": 0.25 * mm});
            skCircle(sketch, "E5.17.2.0", {"center": v(3.19, 3.65) * mm, "radius": 0.25 * mm});
            skCircle(sketch, "E5.17.3.0", {"center": v(3.19, 4.65) * mm, "radius": 0.25 * mm});
            skCircle(sketch, "E5.17.4.0", {"center": v(3.19, 5.65) * mm, "radius": 0.25 * mm});
            skCircle(sketch, "E5.17.5.0", {"center": v(3.19, 6.65) * mm, "radius": 0.25 * mm});
            skCircle(sketch, "E5.17.6.0", {"center": v(3.19, 7.65) * mm, "radius": 0.25 * mm});
            skCircle(sketch, "E5.17.7.0", {"center": v(3.19, 8.65) * mm, "radius": 0.25 * mm});
            skCircle(sketch, "E5.17.8.0", {"center": v(3.19, 9.65) * mm, "radius": 0.25 * mm});
            skCircle(sketch, "E5.17.9.0", {"center": v(3.19, 10.65) * mm, "radius": 0.25 * mm});
            skCircle(sketch, "E5.17.10.0", {"center": v(3.19, 11.65) * mm, "radius": 0.25 * mm});
            skCircle(sketch, "E5.17.11.0", {"center": v(3.19, 12.65) * mm, "radius": 0.25 * mm});
            skCircle(sketch, "E5.17.12.0", {"center": v(3.19, 13.65) * mm, "radius": 0.25 * mm});
            skCircle(sketch, "E5.17.13.0", {"center": v(3.19, 14.65) * mm, "radius": 0.25 * mm});
            skCircle(sketch, "E5.17.14.0", {"center": v(3.19, 15.65) * mm, "radius": 0.25 * mm});
            skCircle(sketch, "E5.17.15.0", {"center": v(3.19, 16.65) * mm, "radius": 0.25 * mm});
            skCircle(sketch, "E5.17.16.0", {"center": v(3.19, 17.65) * mm, "radius": 0.25 * mm});
            skCircle(sketch, "E5.17.17.0", {"center": v(3.19, 18.65) * mm, "radius": 0.25 * mm});
            skCircle(sketch, "E5.17.18.0", {"center": v(3.19, 19.65) * mm, "radius": 0.25 * mm});
            skCircle(sketch, "E5.17.19.0", {"center": v(3.19, 20.65) * mm, "radius": 0.25 * mm});
            skCircle(sketch, "E5.17.20.0", {"center": v(3.19, 21.65) * mm, "radius": 0.25 * mm});
            skCircle(sketch, "E5.17.21.0", {"center": v(3.19, 22.65) * mm, "radius": 0.25 * mm});
            skCircle(sketch, "E5.17.22.0", {"center": v(3.19, 23.65) * mm, "radius": 0.25 * mm});
            skCircle(sketch, "E5.17.23.0", {"center": v(3.19, 24.65) * mm, "radius": 0.25 * mm});
            skCircle(sketch, "E5.17.24.0", {"center": v(3.19, 25.65) * mm, "radius": 0.25 * mm});
            skCircle(sketch, "E5.17.25.0", {"center": v(3.19, 26.65) * mm, "radius": 0.25 * mm});
            skCircle(sketch, "E5.17.26.0", {"center": v(3.19, 27.65) * mm, "radius": 0.25 * mm});
            skCircle(sketch, "E5.17.27.0", {"center": v(3.19, 28.65) * mm, "radius": 0.25 * mm});
            skCircle(sketch, "E5.17.28.0", {"center": v(3.19, 29.65) * mm, "radius": 0.25 * mm});
            skCircle(sketch, "E5.18.0.0", {"center": v(4.19, 1.65) * mm, "radius": 0.25 * mm});
            skCircle(sketch, "E5.18.1.0", {"center": v(4.19, 2.65) * mm, "radius": 0.25 * mm});
            skCircle(sketch, "E5.18.2.0", {"center": v(4.19, 3.65) * mm, "radius": 0.25 * mm});
            skCircle(sketch, "E5.18.3.0", {"center": v(4.19, 4.65) * mm, "radius": 0.25 * mm});
            skCircle(sketch, "E5.18.4.0", {"center": v(4.19, 5.65) * mm, "radius": 0.25 * mm});
            skCircle(sketch, "E5.18.5.0", {"center": v(4.19, 6.65) * mm, "radius": 0.25 * mm});
            skCircle(sketch, "E5.18.6.0", {"center": v(4.19, 7.65) * mm, "radius": 0.25 * mm});
            skCircle(sketch, "E5.18.7.0", {"center": v(4.19, 8.65) * mm, "radius": 0.25 * mm});
            skCircle(sketch, "E5.18.8.0", {"center": v(4.19, 9.65) * mm, "radius": 0.25 * mm});
            skCircle(sketch, "E5.18.9.0", {"center": v(4.19, 10.65) * mm, "radius": 0.25 * mm});
            skCircle(sketch, "E5.18.10.0", {"center": v(4.19, 11.65) * mm, "radius": 0.25 * mm});
            skCircle(sketch, "E5.18.11.0", {"center": v(4.19, 12.65) * mm, "radius": 0.25 * mm});
            skCircle(sketch, "E5.18.12.0", {"center": v(4.19, 13.65) * mm, "radius": 0.25 * mm});
            skCircle(sketch, "E5.18.13.0", {"center": v(4.19, 14.65) * mm, "radius": 0.25 * mm});
            skCircle(sketch, "E5.18.14.0", {"center": v(4.19, 15.65) * mm, "radius": 0.25 * mm});
            skCircle(sketch, "E5.18.15.0", {"center": v(4.19, 16.65) * mm, "radius": 0.25 * mm});
            skCircle(sketch, "E5.18.16.0", {"center": v(4.19, 17.65) * mm, "radius": 0.25 * mm});
            skCircle(sketch, "E5.18.17.0", {"center": v(4.19, 18.65) * mm, "radius": 0.25 * mm});
            skCircle(sketch, "E5.18.18.0", {"center": v(4.19, 19.65) * mm, "radius": 0.25 * mm});
            skCircle(sketch, "E5.18.19.0", {"center": v(4.19, 20.65) * mm, "radius": 0.25 * mm});
            skCircle(sketch, "E5.18.20.0", {"center": v(4.19, 21.65) * mm, "radius": 0.25 * mm});
            skCircle(sketch, "E5.18.21.0", {"center": v(4.19, 22.65) * mm, "radius": 0.25 * mm});
            skCircle(sketch, "E5.18.22.0", {"center": v(4.19, 23.65) * mm, "radius": 0.25 * mm});
            skCircle(sketch, "E5.18.23.0", {"center": v(4.19, 24.65) * mm, "radius": 0.25 * mm});
            skCircle(sketch, "E5.18.24.0", {"center": v(4.19, 25.65) * mm, "radius": 0.25 * mm});
            skCircle(sketch, "E5.18.25.0", {"center": v(4.19, 26.65) * mm, "radius": 0.25 * mm});
            skCircle(sketch, "E5.18.26.0", {"center": v(4.19, 27.65) * mm, "radius": 0.25 * mm});
            skCircle(sketch, "E5.18.27.0", {"center": v(4.19, 28.65) * mm, "radius": 0.25 * mm});
            skCircle(sketch, "E5.18.28.0", {"center": v(4.19, 29.65) * mm, "radius": 0.25 * mm});
            skCircle(sketch, "E5.19.0.0", {"center": v(5.19, 1.65) * mm, "radius": 0.25 * mm});
            skCircle(sketch, "E5.19.1.0", {"center": v(5.19, 2.65) * mm, "radius": 0.25 * mm});
            skCircle(sketch, "E5.19.2.0", {"center": v(5.19, 3.65) * mm, "radius": 0.25 * mm});
            skCircle(sketch, "E5.19.3.0", {"center": v(5.19, 4.65) * mm, "radius": 0.25 * mm});
            skCircle(sketch, "E5.19.4.0", {"center": v(5.19, 5.65) * mm, "radius": 0.25 * mm});
            skCircle(sketch, "E5.19.5.0", {"center": v(5.19, 6.65) * mm, "radius": 0.25 * mm});
            skCircle(sketch, "E5.19.6.0", {"center": v(5.19, 7.65) * mm, "radius": 0.25 * mm});
            skCircle(sketch, "E5.19.7.0", {"center": v(5.19, 8.65) * mm, "radius": 0.25 * mm});
            skCircle(sketch, "E5.19.8.0", {"center": v(5.19, 9.65) * mm, "radius": 0.25 * mm});
            skCircle(sketch, "E5.19.9.0", {"center": v(5.19, 10.65) * mm, "radius": 0.25 * mm});
            skCircle(sketch, "E5.19.10.0", {"center": v(5.19, 11.65) * mm, "radius": 0.25 * mm});
            skCircle(sketch, "E5.19.11.0", {"center": v(5.19, 12.65) * mm, "radius": 0.25 * mm});
            skCircle(sketch, "E5.19.12.0", {"center": v(5.19, 13.65) * mm, "radius": 0.25 * mm});
            skCircle(sketch, "E5.19.13.0", {"center": v(5.19, 14.65) * mm, "radius": 0.25 * mm});
            skCircle(sketch, "E5.19.14.0", {"center": v(5.19, 15.65) * mm, "radius": 0.25 * mm});
            skCircle(sketch, "E5.19.15.0", {"center": v(5.19, 16.65) * mm, "radius": 0.25 * mm});
            skCircle(sketch, "E5.19.16.0", {"center": v(5.19, 17.65) * mm, "radius": 0.25 * mm});
            skCircle(sketch, "E5.19.17.0", {"center": v(5.19, 18.65) * mm, "radius": 0.25 * mm});
            skCircle(sketch, "E5.19.18.0", {"center": v(5.19, 19.65) * mm, "radius": 0.25 * mm});
            skCircle(sketch, "E5.19.19.0", {"center": v(5.19, 20.65) * mm, "radius": 0.25 * mm});
            skCircle(sketch, "E5.19.20.0", {"center": v(5.19, 21.65) * mm, "radius": 0.25 * mm});
            skCircle(sketch, "E5.19.21.0", {"center": v(5.19, 22.65) * mm, "radius": 0.25 * mm});
            skCircle(sketch, "E5.19.22.0", {"center": v(5.19, 23.65) * mm, "radius": 0.25 * mm});
            skCircle(sketch, "E5.19.23.0", {"center": v(5.19, 24.65) * mm, "radius": 0.25 * mm});
            skCircle(sketch, "E5.19.24.0", {"center": v(5.19, 25.65) * mm, "radius": 0.25 * mm});
            skCircle(sketch, "E5.19.25.0", {"center": v(5.19, 26.65) * mm, "radius": 0.25 * mm});
            skCircle(sketch, "E5.19.26.0", {"center": v(5.19, 27.65) * mm, "radius": 0.25 * mm});
            skCircle(sketch, "E5.19.27.0", {"center": v(5.19, 28.65) * mm, "radius": 0.25 * mm});
            skCircle(sketch, "E5.19.28.0", {"center": v(5.19, 29.65) * mm, "radius": 0.25 * mm});
            skCircle(sketch, "E5.20.0.0", {"center": v(6.19, 1.65) * mm, "radius": 0.25 * mm});
            skCircle(sketch, "E5.20.1.0", {"center": v(6.19, 2.65) * mm, "radius": 0.25 * mm});
            skCircle(sketch, "E5.20.2.0", {"center": v(6.19, 3.65) * mm, "radius": 0.25 * mm});
            skCircle(sketch, "E5.20.3.0", {"center": v(6.19, 4.65) * mm, "radius": 0.25 * mm});
            skCircle(sketch, "E5.20.4.0", {"center": v(6.19, 5.65) * mm, "radius": 0.25 * mm});
            skCircle(sketch, "E5.20.5.0", {"center": v(6.19, 6.65) * mm, "radius": 0.25 * mm});
            skCircle(sketch, "E5.20.6.0", {"center": v(6.19, 7.65) * mm, "radius": 0.25 * mm});
            skCircle(sketch, "E5.20.7.0", {"center": v(6.19, 8.65) * mm, "radius": 0.25 * mm});
            skCircle(sketch, "E5.20.8.0", {"center": v(6.19, 9.65) * mm, "radius": 0.25 * mm});
            skCircle(sketch, "E5.20.9.0", {"center": v(6.19, 10.65) * mm, "radius": 0.25 * mm});
            skCircle(sketch, "E5.20.10.0", {"center": v(6.19, 11.65) * mm, "radius": 0.25 * mm});
            skCircle(sketch, "E5.20.11.0", {"center": v(6.19, 12.65) * mm, "radius": 0.25 * mm});
            skCircle(sketch, "E5.20.12.0", {"center": v(6.19, 13.65) * mm, "radius": 0.25 * mm});
            skCircle(sketch, "E5.20.13.0", {"center": v(6.19, 14.65) * mm, "radius": 0.25 * mm});
            skCircle(sketch, "E5.20.14.0", {"center": v(6.19, 15.65) * mm, "radius": 0.25 * mm});
            skCircle(sketch, "E5.20.15.0", {"center": v(6.19, 16.65) * mm, "radius": 0.25 * mm});
            skCircle(sketch, "E5.20.16.0", {"center": v(6.19, 17.65) * mm, "radius": 0.25 * mm});
            skCircle(sketch, "E5.20.17.0", {"center": v(6.19, 18.65) * mm, "radius": 0.25 * mm});
            skCircle(sketch, "E5.20.18.0", {"center": v(6.19, 19.65) * mm, "radius": 0.25 * mm});
            skCircle(sketch, "E5.20.19.0", {"center": v(6.19, 20.65) * mm, "radius": 0.25 * mm});
            skCircle(sketch, "E5.20.20.0", {"center": v(6.19, 21.65) * mm, "radius": 0.25 * mm});
            skCircle(sketch, "E5.20.21.0", {"center": v(6.19, 22.65) * mm, "radius": 0.25 * mm});
            skCircle(sketch, "E5.20.22.0", {"center": v(6.19, 23.65) * mm, "radius": 0.25 * mm});
            skCircle(sketch, "E5.20.23.0", {"center": v(6.19, 24.65) * mm, "radius": 0.25 * mm});
            skCircle(sketch, "E5.20.24.0", {"center": v(6.19, 25.65) * mm, "radius": 0.25 * mm});
            skCircle(sketch, "E5.20.25.0", {"center": v(6.19, 26.65) * mm, "radius": 0.25 * mm});
            skCircle(sketch, "E5.20.26.0", {"center": v(6.19, 27.65) * mm, "radius": 0.25 * mm});
            skCircle(sketch, "E5.20.27.0", {"center": v(6.19, 28.65) * mm, "radius": 0.25 * mm});
            skCircle(sketch, "E5.20.28.0", {"center": v(6.19, 29.65) * mm, "radius": 0.25 * mm});
            skCircle(sketch, "E5.21.0.0", {"center": v(7.19, 1.65) * mm, "radius": 0.25 * mm});
            skCircle(sketch, "E5.21.1.0", {"center": v(7.19, 2.65) * mm, "radius": 0.25 * mm});
            skCircle(sketch, "E5.21.2.0", {"center": v(7.19, 3.65) * mm, "radius": 0.25 * mm});
            skCircle(sketch, "E5.21.3.0", {"center": v(7.19, 4.65) * mm, "radius": 0.25 * mm});
            skCircle(sketch, "E5.21.4.0", {"center": v(7.19, 5.65) * mm, "radius": 0.25 * mm});
            skCircle(sketch, "E5.21.5.0", {"center": v(7.19, 6.65) * mm, "radius": 0.25 * mm});
            skCircle(sketch, "E5.21.6.0", {"center": v(7.19, 7.65) * mm, "radius": 0.25 * mm});
            skCircle(sketch, "E5.21.7.0", {"center": v(7.19, 8.65) * mm, "radius": 0.25 * mm});
            skCircle(sketch, "E5.21.8.0", {"center": v(7.19, 9.65) * mm, "radius": 0.25 * mm});
            skCircle(sketch, "E5.21.9.0", {"center": v(7.19, 10.65) * mm, "radius": 0.25 * mm});
            skCircle(sketch, "E5.21.10.0", {"center": v(7.19, 11.65) * mm, "radius": 0.25 * mm});
            skCircle(sketch, "E5.21.11.0", {"center": v(7.19, 12.65) * mm, "radius": 0.25 * mm});
            skCircle(sketch, "E5.21.12.0", {"center": v(7.19, 13.65) * mm, "radius": 0.25 * mm});
            skCircle(sketch, "E5.21.13.0", {"center": v(7.19, 14.65) * mm, "radius": 0.25 * mm});
            skCircle(sketch, "E5.21.14.0", {"center": v(7.19, 15.65) * mm, "radius": 0.25 * mm});
            skCircle(sketch, "E5.21.15.0", {"center": v(7.19, 16.65) * mm, "radius": 0.25 * mm});
            skCircle(sketch, "E5.21.16.0", {"center": v(7.19, 17.65) * mm, "radius": 0.25 * mm});
            skCircle(sketch, "E5.21.17.0", {"center": v(7.19, 18.65) * mm, "radius": 0.25 * mm});
            skCircle(sketch, "E5.21.18.0", {"center": v(7.19, 19.65) * mm, "radius": 0.25 * mm});
            skCircle(sketch, "E5.21.19.0", {"center": v(7.19, 20.65) * mm, "radius": 0.25 * mm});
            skCircle(sketch, "E5.21.20.0", {"center": v(7.19, 21.65) * mm, "radius": 0.25 * mm});
            skCircle(sketch, "E5.21.21.0", {"center": v(7.19, 22.65) * mm, "radius": 0.25 * mm});
            skCircle(sketch, "E5.21.22.0", {"center": v(7.19, 23.65) * mm, "radius": 0.25 * mm});
            skCircle(sketch, "E5.21.23.0", {"center": v(7.19, 24.65) * mm, "radius": 0.25 * mm});
            skCircle(sketch, "E5.21.24.0", {"center": v(7.19, 25.65) * mm, "radius": 0.25 * mm});
            skCircle(sketch, "E5.21.25.0", {"center": v(7.19, 26.65) * mm, "radius": 0.25 * mm});
            skCircle(sketch, "E5.21.26.0", {"center": v(7.19, 27.65) * mm, "radius": 0.25 * mm});
            skCircle(sketch, "E5.21.27.0", {"center": v(7.19, 28.65) * mm, "radius": 0.25 * mm});
            skCircle(sketch, "E5.21.28.0", {"center": v(7.19, 29.65) * mm, "radius": 0.25 * mm});
            skCircle(sketch, "E5.22.0.0", {"center": v(8.19, 1.65) * mm, "radius": 0.25 * mm});
            skCircle(sketch, "E5.22.1.0", {"center": v(8.19, 2.65) * mm, "radius": 0.25 * mm});
            skCircle(sketch, "E5.22.2.0", {"center": v(8.19, 3.65) * mm, "radius": 0.25 * mm});
            skCircle(sketch, "E5.22.3.0", {"center": v(8.19, 4.65) * mm, "radius": 0.25 * mm});
            skCircle(sketch, "E5.22.4.0", {"center": v(8.19, 5.65) * mm, "radius": 0.25 * mm});
            skCircle(sketch, "E5.22.5.0", {"center": v(8.19, 6.65) * mm, "radius": 0.25 * mm});
            skCircle(sketch, "E5.22.6.0", {"center": v(8.19, 7.65) * mm, "radius": 0.25 * mm});
            skCircle(sketch, "E5.22.7.0", {"center": v(8.19, 8.65) * mm, "radius": 0.25 * mm});
            skCircle(sketch, "E5.22.8.0", {"center": v(8.19, 9.65) * mm, "radius": 0.25 * mm});
            skCircle(sketch, "E5.22.9.0", {"center": v(8.19, 10.65) * mm, "radius": 0.25 * mm});
            skCircle(sketch, "E5.22.10.0", {"center": v(8.19, 11.65) * mm, "radius": 0.25 * mm});
            skCircle(sketch, "E5.22.11.0", {"center": v(8.19, 12.65) * mm, "radius": 0.25 * mm});
            skCircle(sketch, "E5.22.12.0", {"center": v(8.19, 13.65) * mm, "radius": 0.25 * mm});
            skCircle(sketch, "E5.22.13.0", {"center": v(8.19, 14.65) * mm, "radius": 0.25 * mm});
            skCircle(sketch, "E5.22.14.0", {"center": v(8.19, 15.65) * mm, "radius": 0.25 * mm});
            skCircle(sketch, "E5.22.15.0", {"center": v(8.19, 16.65) * mm, "radius": 0.25 * mm});
            skCircle(sketch, "E5.22.16.0", {"center": v(8.19, 17.65) * mm, "radius": 0.25 * mm});
            skCircle(sketch, "E5.22.17.0", {"center": v(8.19, 18.65) * mm, "radius": 0.25 * mm});
            skCircle(sketch, "E5.22.18.0", {"center": v(8.19, 19.65) * mm, "radius": 0.25 * mm});
            skCircle(sketch, "E5.22.19.0", {"center": v(8.19, 20.65) * mm, "radius": 0.25 * mm});
            skCircle(sketch, "E5.22.20.0", {"center": v(8.19, 21.65) * mm, "radius": 0.25 * mm});
            skCircle(sketch, "E5.22.21.0", {"center": v(8.19, 22.65) * mm, "radius": 0.25 * mm});
            skCircle(sketch, "E5.22.22.0", {"center": v(8.19, 23.65) * mm, "radius": 0.25 * mm});
            skCircle(sketch, "E5.22.23.0", {"center": v(8.19, 24.65) * mm, "radius": 0.25 * mm});
            skCircle(sketch, "E5.22.24.0", {"center": v(8.19, 25.65) * mm, "radius": 0.25 * mm});
            skCircle(sketch, "E5.22.25.0", {"center": v(8.19, 26.65) * mm, "radius": 0.25 * mm});
            skCircle(sketch, "E5.22.26.0", {"center": v(8.19, 27.65) * mm, "radius": 0.25 * mm});
            skCircle(sketch, "E5.22.27.0", {"center": v(8.19, 28.65) * mm, "radius": 0.25 * mm});
            skCircle(sketch, "E5.22.28.0", {"center": v(8.19, 29.65) * mm, "radius": 0.25 * mm});
            skCircle(sketch, "E5.23.0.0", {"center": v(9.19, 1.65) * mm, "radius": 0.25 * mm});
            skCircle(sketch, "E5.23.1.0", {"center": v(9.19, 2.65) * mm, "radius": 0.25 * mm});
            skCircle(sketch, "E5.23.2.0", {"center": v(9.19, 3.65) * mm, "radius": 0.25 * mm});
            skCircle(sketch, "E5.23.3.0", {"center": v(9.19, 4.65) * mm, "radius": 0.25 * mm});
            skCircle(sketch, "E5.23.4.0", {"center": v(9.19, 5.65) * mm, "radius": 0.25 * mm});
            skCircle(sketch, "E5.23.5.0", {"center": v(9.19, 6.65) * mm, "radius": 0.25 * mm});
            skCircle(sketch, "E5.23.6.0", {"center": v(9.19, 7.65) * mm, "radius": 0.25 * mm});
            skCircle(sketch, "E5.23.7.0", {"center": v(9.19, 8.65) * mm, "radius": 0.25 * mm});
            skCircle(sketch, "E5.23.8.0", {"center": v(9.19, 9.65) * mm, "radius": 0.25 * mm});
            skCircle(sketch, "E5.23.9.0", {"center": v(9.19, 10.65) * mm, "radius": 0.25 * mm});
            skCircle(sketch, "E5.23.10.0", {"center": v(9.19, 11.65) * mm, "radius": 0.25 * mm});
            skCircle(sketch, "E5.23.11.0", {"center": v(9.19, 12.65) * mm, "radius": 0.25 * mm});
            skCircle(sketch, "E5.23.12.0", {"center": v(9.19, 13.65) * mm, "radius": 0.25 * mm});
            skCircle(sketch, "E5.23.13.0", {"center": v(9.19, 14.65) * mm, "radius": 0.25 * mm});
            skCircle(sketch, "E5.23.14.0", {"center": v(9.19, 15.65) * mm, "radius": 0.25 * mm});
            skCircle(sketch, "E5.23.15.0", {"center": v(9.19, 16.65) * mm, "radius": 0.25 * mm});
            skCircle(sketch, "E5.23.16.0", {"center": v(9.19, 17.65) * mm, "radius": 0.25 * mm});
            skCircle(sketch, "E5.23.17.0", {"center": v(9.19, 18.65) * mm, "radius": 0.25 * mm});
            skCircle(sketch, "E5.23.18.0", {"center": v(9.19, 19.65) * mm, "radius": 0.25 * mm});
            skCircle(sketch, "E5.23.19.0", {"center": v(9.19, 20.65) * mm, "radius": 0.25 * mm});
            skCircle(sketch, "E5.23.20.0", {"center": v(9.19, 21.65) * mm, "radius": 0.25 * mm});
            skCircle(sketch, "E5.23.21.0", {"center": v(9.19, 22.65) * mm, "radius": 0.25 * mm});
            skCircle(sketch, "E5.23.22.0", {"center": v(9.19, 23.65) * mm, "radius": 0.25 * mm});
            skCircle(sketch, "E5.23.23.0", {"center": v(9.19, 24.65) * mm, "radius": 0.25 * mm});
            skCircle(sketch, "E5.23.24.0", {"center": v(9.19, 25.65) * mm, "radius": 0.25 * mm});
            skCircle(sketch, "E5.23.25.0", {"center": v(9.19, 26.65) * mm, "radius": 0.25 * mm});
            skCircle(sketch, "E5.23.26.0", {"center": v(9.19, 27.65) * mm, "radius": 0.25 * mm});
            skCircle(sketch, "E5.23.27.0", {"center": v(9.19, 28.65) * mm, "radius": 0.25 * mm});
            skCircle(sketch, "E5.23.28.0", {"center": v(9.19, 29.65) * mm, "radius": 0.25 * mm});
            skCircle(sketch, "E5.24.0.0", {"center": v(10.19, 1.65) * mm, "radius": 0.25 * mm});
            skCircle(sketch, "E5.24.1.0", {"center": v(10.19, 2.65) * mm, "radius": 0.25 * mm});
            skCircle(sketch, "E5.24.2.0", {"center": v(10.19, 3.65) * mm, "radius": 0.25 * mm});
            skCircle(sketch, "E5.24.3.0", {"center": v(10.19, 4.65) * mm, "radius": 0.25 * mm});
            skCircle(sketch, "E5.24.4.0", {"center": v(10.19, 5.65) * mm, "radius": 0.25 * mm});
            skCircle(sketch, "E5.24.5.0", {"center": v(10.19, 6.65) * mm, "radius": 0.25 * mm});
            skCircle(sketch, "E5.24.6.0", {"center": v(10.19, 7.65) * mm, "radius": 0.25 * mm});
            skCircle(sketch, "E5.24.7.0", {"center": v(10.19, 8.65) * mm, "radius": 0.25 * mm});
            skCircle(sketch, "E5.24.8.0", {"center": v(10.19, 9.65) * mm, "radius": 0.25 * mm});
            skCircle(sketch, "E5.24.9.0", {"center": v(10.19, 10.65) * mm, "radius": 0.25 * mm});
            skCircle(sketch, "E5.24.10.0", {"center": v(10.19, 11.65) * mm, "radius": 0.25 * mm});
            skCircle(sketch, "E5.24.11.0", {"center": v(10.19, 12.65) * mm, "radius": 0.25 * mm});
            skCircle(sketch, "E5.24.12.0", {"center": v(10.19, 13.65) * mm, "radius": 0.25 * mm});
            skCircle(sketch, "E5.24.13.0", {"center": v(10.19, 14.65) * mm, "radius": 0.25 * mm});
            skCircle(sketch, "E5.24.14.0", {"center": v(10.19, 15.65) * mm, "radius": 0.25 * mm});
            skCircle(sketch, "E5.24.15.0", {"center": v(10.19, 16.65) * mm, "radius": 0.25 * mm});
            skCircle(sketch, "E5.24.16.0", {"center": v(10.19, 17.65) * mm, "radius": 0.25 * mm});
            skCircle(sketch, "E5.24.17.0", {"center": v(10.19, 18.65) * mm, "radius": 0.25 * mm});
            skCircle(sketch, "E5.24.18.0", {"center": v(10.19, 19.65) * mm, "radius": 0.25 * mm});
            skCircle(sketch, "E5.24.19.0", {"center": v(10.19, 20.65) * mm, "radius": 0.25 * mm});
            skCircle(sketch, "E5.24.20.0", {"center": v(10.19, 21.65) * mm, "radius": 0.25 * mm});
            skCircle(sketch, "E5.24.21.0", {"center": v(10.19, 22.65) * mm, "radius": 0.25 * mm});
            skCircle(sketch, "E5.24.22.0", {"center": v(10.19, 23.65) * mm, "radius": 0.25 * mm});
            skCircle(sketch, "E5.24.23.0", {"center": v(10.19, 24.65) * mm, "radius": 0.25 * mm});
            skCircle(sketch, "E5.24.24.0", {"center": v(10.19, 25.65) * mm, "radius": 0.25 * mm});
            skCircle(sketch, "E5.24.25.0", {"center": v(10.19, 26.65) * mm, "radius": 0.25 * mm});
            skCircle(sketch, "E5.24.26.0", {"center": v(10.19, 27.65) * mm, "radius": 0.25 * mm});
            skCircle(sketch, "E5.24.27.0", {"center": v(10.19, 28.65) * mm, "radius": 0.25 * mm});
            skCircle(sketch, "E5.24.28.0", {"center": v(10.19, 29.65) * mm, "radius": 0.25 * mm});
            skCircle(sketch, "E5.25.0.0", {"center": v(11.19, 1.65) * mm, "radius": 0.25 * mm});
            skCircle(sketch, "E5.25.1.0", {"center": v(11.19, 2.65) * mm, "radius": 0.25 * mm});
            skCircle(sketch, "E5.25.2.0", {"center": v(11.19, 3.65) * mm, "radius": 0.25 * mm});
            skCircle(sketch, "E5.25.3.0", {"center": v(11.19, 4.65) * mm, "radius": 0.25 * mm});
            skCircle(sketch, "E5.25.4.0", {"center": v(11.19, 5.65) * mm, "radius": 0.25 * mm});
            skCircle(sketch, "E5.25.5.0", {"center": v(11.19, 6.65) * mm, "radius": 0.25 * mm});
            skCircle(sketch, "E5.25.6.0", {"center": v(11.19, 7.65) * mm, "radius": 0.25 * mm});
            skCircle(sketch, "E5.25.7.0", {"center": v(11.19, 8.65) * mm, "radius": 0.25 * mm});
            skCircle(sketch, "E5.25.8.0", {"center": v(11.19, 9.65) * mm, "radius": 0.25 * mm});
            skCircle(sketch, "E5.25.9.0", {"center": v(11.19, 10.65) * mm, "radius": 0.25 * mm});
            skCircle(sketch, "E5.25.10.0", {"center": v(11.19, 11.65) * mm, "radius": 0.25 * mm});
            skCircle(sketch, "E5.25.11.0", {"center": v(11.19, 12.65) * mm, "radius": 0.25 * mm});
            skCircle(sketch, "E5.25.12.0", {"center": v(11.19, 13.65) * mm, "radius": 0.25 * mm});
            skCircle(sketch, "E5.25.13.0", {"center": v(11.19, 14.65) * mm, "radius": 0.25 * mm});
            skCircle(sketch, "E5.25.14.0", {"center": v(11.19, 15.65) * mm, "radius": 0.25 * mm});
            skCircle(sketch, "E5.25.15.0", {"center": v(11.19, 16.65) * mm, "radius": 0.25 * mm});
            skCircle(sketch, "E5.25.16.0", {"center": v(11.19, 17.65) * mm, "radius": 0.25 * mm});
            skCircle(sketch, "E5.25.17.0", {"center": v(11.19, 18.65) * mm, "radius": 0.25 * mm});
            skCircle(sketch, "E5.25.18.0", {"center": v(11.19, 19.65) * mm, "radius": 0.25 * mm});
            skCircle(sketch, "E5.25.19.0", {"center": v(11.19, 20.65) * mm, "radius": 0.25 * mm});
            skCircle(sketch, "E5.25.20.0", {"center": v(11.19, 21.65) * mm, "radius": 0.25 * mm});
            skCircle(sketch, "E5.25.21.0", {"center": v(11.19, 22.65) * mm, "radius": 0.25 * mm});
            skCircle(sketch, "E5.25.22.0", {"center": v(11.19, 23.65) * mm, "radius": 0.25 * mm});
            skCircle(sketch, "E5.25.23.0", {"center": v(11.19, 24.65) * mm, "radius": 0.25 * mm});
            skCircle(sketch, "E5.25.24.0", {"center": v(11.19, 25.65) * mm, "radius": 0.25 * mm});
            skCircle(sketch, "E5.25.25.0", {"center": v(11.19, 26.65) * mm, "radius": 0.25 * mm});
            skCircle(sketch, "E5.25.26.0", {"center": v(11.19, 27.65) * mm, "radius": 0.25 * mm});
            skCircle(sketch, "E5.25.27.0", {"center": v(11.19, 28.65) * mm, "radius": 0.25 * mm});
            skCircle(sketch, "E5.25.28.0", {"center": v(11.19, 29.65) * mm, "radius": 0.25 * mm});
            skCircle(sketch, "E5.26.0.0", {"center": v(12.19, 1.65) * mm, "radius": 0.25 * mm});
            skCircle(sketch, "E5.26.1.0", {"center": v(12.19, 2.65) * mm, "radius": 0.25 * mm});
            skCircle(sketch, "E5.26.2.0", {"center": v(12.19, 3.65) * mm, "radius": 0.25 * mm});
            skCircle(sketch, "E5.26.3.0", {"center": v(12.19, 4.65) * mm, "radius": 0.25 * mm});
            skCircle(sketch, "E5.26.4.0", {"center": v(12.19, 5.65) * mm, "radius": 0.25 * mm});
            skCircle(sketch, "E5.26.5.0", {"center": v(12.19, 6.65) * mm, "radius": 0.25 * mm});
            skCircle(sketch, "E5.26.6.0", {"center": v(12.19, 7.65) * mm, "radius": 0.25 * mm});
            skCircle(sketch, "E5.26.7.0", {"center": v(12.19, 8.65) * mm, "radius": 0.25 * mm});
            skCircle(sketch, "E5.26.8.0", {"center": v(12.19, 9.65) * mm, "radius": 0.25 * mm});
            skCircle(sketch, "E5.26.9.0", {"center": v(12.19, 10.65) * mm, "radius": 0.25 * mm});
            skCircle(sketch, "E5.26.10.0", {"center": v(12.19, 11.65) * mm, "radius": 0.25 * mm});
            skCircle(sketch, "E5.26.11.0", {"center": v(12.19, 12.65) * mm, "radius": 0.25 * mm});
            skCircle(sketch, "E5.26.12.0", {"center": v(12.19, 13.65) * mm, "radius": 0.25 * mm});
            skCircle(sketch, "E5.26.13.0", {"center": v(12.19, 14.65) * mm, "radius": 0.25 * mm});
            skCircle(sketch, "E5.26.14.0", {"center": v(12.19, 15.65) * mm, "radius": 0.25 * mm});
            skCircle(sketch, "E5.26.15.0", {"center": v(12.19, 16.65) * mm, "radius": 0.25 * mm});
            skCircle(sketch, "E5.26.16.0", {"center": v(12.19, 17.65) * mm, "radius": 0.25 * mm});
            skCircle(sketch, "E5.26.17.0", {"center": v(12.19, 18.65) * mm, "radius": 0.25 * mm});
            skCircle(sketch, "E5.26.18.0", {"center": v(12.19, 19.65) * mm, "radius": 0.25 * mm});
            skCircle(sketch, "E5.26.19.0", {"center": v(12.19, 20.65) * mm, "radius": 0.25 * mm});
            skCircle(sketch, "E5.26.20.0", {"center": v(12.19, 21.65) * mm, "radius": 0.25 * mm});
            skCircle(sketch, "E5.26.21.0", {"center": v(12.19, 22.65) * mm, "radius": 0.25 * mm});
            skCircle(sketch, "E5.26.22.0", {"center": v(12.19, 23.65) * mm, "radius": 0.25 * mm});
            skCircle(sketch, "E5.26.23.0", {"center": v(12.19, 24.65) * mm, "radius": 0.25 * mm});
            skCircle(sketch, "E5.26.24.0", {"center": v(12.19, 25.65) * mm, "radius": 0.25 * mm});
            skCircle(sketch, "E5.26.25.0", {"center": v(12.19, 26.65) * mm, "radius": 0.25 * mm});
            skCircle(sketch, "E5.26.26.0", {"center": v(12.19, 27.65) * mm, "radius": 0.25 * mm});
            skCircle(sketch, "E5.26.27.0", {"center": v(12.19, 28.65) * mm, "radius": 0.25 * mm});
            skCircle(sketch, "E5.26.28.0", {"center": v(12.19, 29.65) * mm, "radius": 0.25 * mm});
            skCircle(sketch, "E5.27.0.0", {"center": v(13.19, 1.65) * mm, "radius": 0.25 * mm});
            skCircle(sketch, "E5.27.1.0", {"center": v(13.19, 2.65) * mm, "radius": 0.25 * mm});
            skCircle(sketch, "E5.27.2.0", {"center": v(13.19, 3.65) * mm, "radius": 0.25 * mm});
            skCircle(sketch, "E5.27.3.0", {"center": v(13.19, 4.65) * mm, "radius": 0.25 * mm});
            skCircle(sketch, "E5.27.4.0", {"center": v(13.19, 5.65) * mm, "radius": 0.25 * mm});
            skCircle(sketch, "E5.27.5.0", {"center": v(13.19, 6.65) * mm, "radius": 0.25 * mm});
            skCircle(sketch, "E5.27.6.0", {"center": v(13.19, 7.65) * mm, "radius": 0.25 * mm});
            skCircle(sketch, "E5.27.7.0", {"center": v(13.19, 8.65) * mm, "radius": 0.25 * mm});
            skCircle(sketch, "E5.27.8.0", {"center": v(13.19, 9.65) * mm, "radius": 0.25 * mm});
            skCircle(sketch, "E5.27.9.0", {"center": v(13.19, 10.65) * mm, "radius": 0.25 * mm});
            skCircle(sketch, "E5.27.10.0", {"center": v(13.19, 11.65) * mm, "radius": 0.25 * mm});
            skCircle(sketch, "E5.27.11.0", {"center": v(13.19, 12.65) * mm, "radius": 0.25 * mm});
            skCircle(sketch, "E5.27.12.0", {"center": v(13.19, 13.65) * mm, "radius": 0.25 * mm});
            skCircle(sketch, "E5.27.13.0", {"center": v(13.19, 14.65) * mm, "radius": 0.25 * mm});
            skCircle(sketch, "E5.27.14.0", {"center": v(13.19, 15.65) * mm, "radius": 0.25 * mm});
            skCircle(sketch, "E5.27.15.0", {"center": v(13.19, 16.65) * mm, "radius": 0.25 * mm});
            skCircle(sketch, "E5.27.16.0", {"center": v(13.19, 17.65) * mm, "radius": 0.25 * mm});
            skCircle(sketch, "E5.27.17.0", {"center": v(13.19, 18.65) * mm, "radius": 0.25 * mm});
            skCircle(sketch, "E5.27.18.0", {"center": v(13.19, 19.65) * mm, "radius": 0.25 * mm});
            skCircle(sketch, "E5.27.19.0", {"center": v(13.19, 20.65) * mm, "radius": 0.25 * mm});
            skCircle(sketch, "E5.27.20.0", {"center": v(13.19, 21.65) * mm, "radius": 0.25 * mm});
            skCircle(sketch, "E5.27.21.0", {"center": v(13.19, 22.65) * mm, "radius": 0.25 * mm});
            skCircle(sketch, "E5.27.22.0", {"center": v(13.19, 23.65) * mm, "radius": 0.25 * mm});
            skCircle(sketch, "E5.27.23.0", {"center": v(13.19, 24.65) * mm, "radius": 0.25 * mm});
            skCircle(sketch, "E5.27.24.0", {"center": v(13.19, 25.65) * mm, "radius": 0.25 * mm});
            skCircle(sketch, "E5.27.25.0", {"center": v(13.19, 26.65) * mm, "radius": 0.25 * mm});
            skCircle(sketch, "E5.27.26.0", {"center": v(13.19, 27.65) * mm, "radius": 0.25 * mm});
            skCircle(sketch, "E5.27.27.0", {"center": v(13.19, 28.65) * mm, "radius": 0.25 * mm});
            skCircle(sketch, "E5.27.28.0", {"center": v(13.19, 29.65) * mm, "radius": 0.25 * mm});
            skLineSegment(sketch, "E5.direction1", {"start": v(-13.81, 1.65) * mm, "end": v(-12.81, 1.65) * mm, "construction": true});
            skLineSegment(sketch, "E5.direction2", {"start": v(-13.81, 1.65) * mm, "end": v(-13.81, 2.65) * mm, "construction": true});
            skSolve(sketch);
        }
        {
            var Q0;
            Q0 = qSketchRegion(id + "F6", true);
            extrude(context, id + "F7", {"entities" : qUnion([Q0]), "operationType" : NewBodyOperationType.REMOVE, "oppositeDirection" : true, "depth" : 45 * mm});
        }
    });
